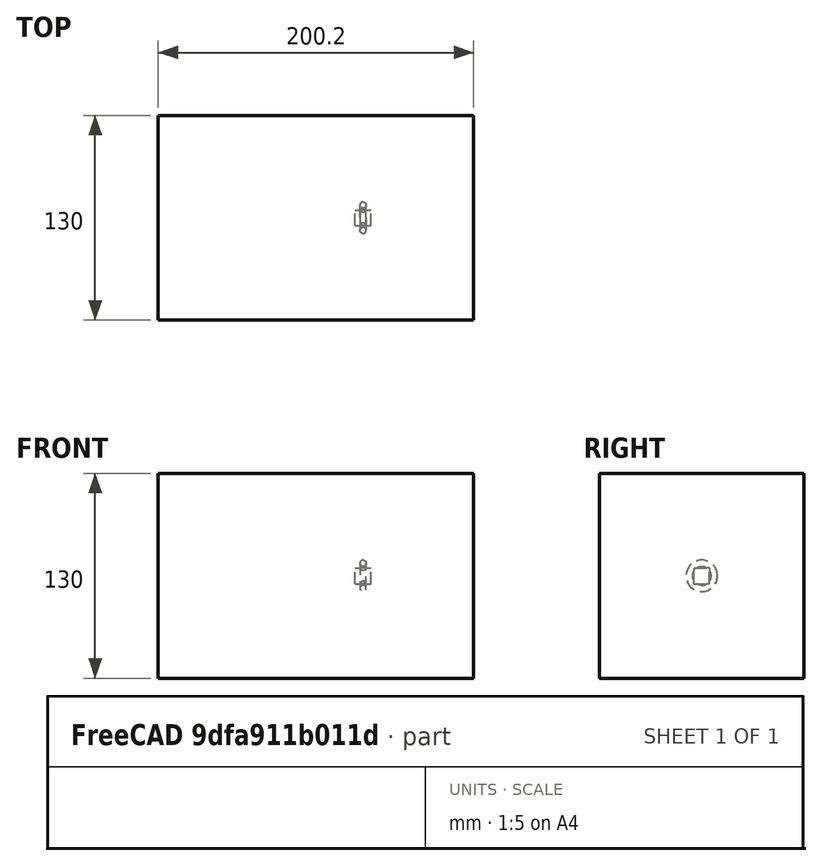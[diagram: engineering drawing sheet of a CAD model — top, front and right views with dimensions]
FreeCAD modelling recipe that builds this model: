
FCSTD DOCUMENT  (FreeCAD 1.0R39109 (Git))
Label: polarArray-7-array-rotated
License: All rights reserved
objects: App::DocumentObjectGroupPython×1251, Part::FeaturePython×4, App::Part×2, Part::MultiFuse×1
note: 4 computed .brp shape members not serialized (recipe doc carries the construction recipe); baked Part::Feature solids carry a one-line shape summary decoded from their .brp

FEATURE [App::DocumentObjectGroupPython] HALFPI  # scripted group (container) (typed FeaturePython)
  name = HALFPI
  value = pi/2.
FEATURE [App::DocumentObjectGroupPython] PI  # scripted group (container) (typed FeaturePython)
  name = PI
  value = 1.*pi
FEATURE [App::DocumentObjectGroupPython] TWOPI  # scripted group (container) (typed FeaturePython)
  name = TWOPI
  value = 2.*pi
FEATURE [App::DocumentObjectGroupPython] Constants  # scripted group (container) (typed FeaturePython)
  Group = -> [HALFPI,PI,TWOPI]
FEATURE [App::DocumentObjectGroupPython] Variables  # scripted group (container) (typed FeaturePython)
FEATURE [App::DocumentObjectGroupPython] Quantities  # scripted group (container) (typed FeaturePython)
FEATURE [App::DocumentObjectGroupPython] Isotopes  # scripted group (container) (typed FeaturePython)
FEATURE [App::DocumentObjectGroupPython] Elements  # scripted group (container) (typed FeaturePython)
FEATURE [App::DocumentObjectGroupPython] Matrix  # scripted group (container) (typed FeaturePython)
FEATURE [App::DocumentObjectGroupPython] Surfaces  # scripted group (container) (typed FeaturePython)
FEATURE [App::DocumentObjectGroupPython] Opticals  # scripted group (container) (typed FeaturePython)
  Group = -> [Matrix,Surfaces]
FEATURE [App::DocumentObjectGroupPython] G4Isotopes  # scripted group (container) (typed FeaturePython)
FEATURE [App::DocumentObjectGroupPython] H_element  # scripted group (container) (typed FeaturePython)
  Z = 1
  atom_value = 1.008
  formula = H
  name = H_element
FEATURE [App::DocumentObjectGroupPython] He_element  # scripted group (container) (typed FeaturePython)
  Z = 2
  atom_value = 4.0026
  formula = He
  name = He_element
FEATURE [App::DocumentObjectGroupPython] Li_element  # scripted group (container) (typed FeaturePython)
  Z = 3
  atom_value = 6.94
  formula = Li
  name = Li_element
FEATURE [App::DocumentObjectGroupPython] Be_element  # scripted group (container) (typed FeaturePython)
  Z = 4
  atom_value = 9.01218
  formula = Be
  name = Be_element
FEATURE [App::DocumentObjectGroupPython] B_element  # scripted group (container) (typed FeaturePython)
  Z = 5
  atom_value = 10.81
  formula = B
  name = B_element
FEATURE [App::DocumentObjectGroupPython] C_element  # scripted group (container) (typed FeaturePython)
  Z = 6
  atom_value = 12.011
  formula = C
  name = C_element
FEATURE [App::DocumentObjectGroupPython] N_element  # scripted group (container) (typed FeaturePython)
  Z = 7
  atom_value = 14.007
  formula = N
  name = N_element
FEATURE [App::DocumentObjectGroupPython] O_element  # scripted group (container) (typed FeaturePython)
  Z = 8
  atom_value = 15.999
  formula = O
  name = O_element
FEATURE [App::DocumentObjectGroupPython] F_element  # scripted group (container) (typed FeaturePython)
  Z = 9
  atom_value = 18.9984
  formula = F
  name = F_element
FEATURE [App::DocumentObjectGroupPython] Ne_element  # scripted group (container) (typed FeaturePython)
  Z = 10
  atom_value = 20.1797
  formula = Ne
  name = Ne_element
FEATURE [App::DocumentObjectGroupPython] Na_element  # scripted group (container) (typed FeaturePython)
  Z = 11
  atom_value = 22.9898
  formula = Na
  name = Na_element
FEATURE [App::DocumentObjectGroupPython] Mg_element  # scripted group (container) (typed FeaturePython)
  Z = 12
  atom_value = 24.305
  formula = Mg
  name = Mg_element
FEATURE [App::DocumentObjectGroupPython] Al_element  # scripted group (container) (typed FeaturePython)
  Z = 13
  atom_value = 26.9815
  formula = Al
  name = Al_element
FEATURE [App::DocumentObjectGroupPython] Si_element  # scripted group (container) (typed FeaturePython)
  Z = 14
  atom_value = 28.085
  formula = Si
  name = Si_element
FEATURE [App::DocumentObjectGroupPython] P_element  # scripted group (container) (typed FeaturePython)
  Z = 15
  atom_value = 30.9738
  formula = P
  name = P_element
FEATURE [App::DocumentObjectGroupPython] S_element  # scripted group (container) (typed FeaturePython)
  Z = 16
  atom_value = 32.06
  formula = S
  name = S_element
FEATURE [App::DocumentObjectGroupPython] Cl_element  # scripted group (container) (typed FeaturePython)
  Z = 17
  atom_value = 35.45
  formula = Cl
  name = Cl_element
FEATURE [App::DocumentObjectGroupPython] Ar_element  # scripted group (container) (typed FeaturePython)
  Z = 18
  atom_value = 39.95
  formula = Ar
  name = Ar_element
FEATURE [App::DocumentObjectGroupPython] K_element  # scripted group (container) (typed FeaturePython)
  Z = 19
  atom_value = 39.0983
  formula = K
  name = K_element
FEATURE [App::DocumentObjectGroupPython] Ca_element  # scripted group (container) (typed FeaturePython)
  Z = 20
  atom_value = 40.078
  formula = Ca
  name = Ca_element
FEATURE [App::DocumentObjectGroupPython] Sc_element  # scripted group (container) (typed FeaturePython)
  Z = 21
  atom_value = 44.9559
  formula = Sc
  name = Sc_element
FEATURE [App::DocumentObjectGroupPython] Ti_element  # scripted group (container) (typed FeaturePython)
  Z = 22
  atom_value = 47.867
  formula = Ti
  name = Ti_element
FEATURE [App::DocumentObjectGroupPython] V_element  # scripted group (container) (typed FeaturePython)
  Z = 23
  atom_value = 50.9415
  formula = V
  name = V_element
FEATURE [App::DocumentObjectGroupPython] Cr_element  # scripted group (container) (typed FeaturePython)
  Z = 24
  atom_value = 51.9961
  formula = Cr
  name = Cr_element
FEATURE [App::DocumentObjectGroupPython] Mn_element  # scripted group (container) (typed FeaturePython)
  Z = 25
  atom_value = 54.938
  formula = Mn
  name = Mn_element
FEATURE [App::DocumentObjectGroupPython] Fe_element  # scripted group (container) (typed FeaturePython)
  Z = 26
  atom_value = 55.845
  formula = Fe
  name = Fe_element
FEATURE [App::DocumentObjectGroupPython] Co_element  # scripted group (container) (typed FeaturePython)
  Z = 27
  atom_value = 58.9332
  formula = Co
  name = Co_element
FEATURE [App::DocumentObjectGroupPython] Ni_element  # scripted group (container) (typed FeaturePython)
  Z = 28
  atom_value = 58.6934
  formula = Ni
  name = Ni_element
FEATURE [App::DocumentObjectGroupPython] Cu_element  # scripted group (container) (typed FeaturePython)
  Z = 29
  atom_value = 63.546
  formula = Cu
  name = Cu_element
FEATURE [App::DocumentObjectGroupPython] Zn_element  # scripted group (container) (typed FeaturePython)
  Z = 30
  atom_value = 65.38
  formula = Zn
  name = Zn_element
FEATURE [App::DocumentObjectGroupPython] Ga_element  # scripted group (container) (typed FeaturePython)
  Z = 31
  atom_value = 69.723
  formula = Ga
  name = Ga_element
FEATURE [App::DocumentObjectGroupPython] Ge_element  # scripted group (container) (typed FeaturePython)
  Z = 32
  atom_value = 72.63
  formula = Ge
  name = Ge_element
FEATURE [App::DocumentObjectGroupPython] As_element  # scripted group (container) (typed FeaturePython)
  Z = 33
  atom_value = 74.9216
  formula = As
  name = As_element
FEATURE [App::DocumentObjectGroupPython] Se_element  # scripted group (container) (typed FeaturePython)
  Z = 34
  atom_value = 78.971
  formula = Se
  name = Se_element
FEATURE [App::DocumentObjectGroupPython] Br_element  # scripted group (container) (typed FeaturePython)
  Z = 35
  atom_value = 79.904
  formula = Br
  name = Br_element
FEATURE [App::DocumentObjectGroupPython] Kr_element  # scripted group (container) (typed FeaturePython)
  Z = 36
  atom_value = 83.798
  formula = Kr
  name = Kr_element
FEATURE [App::DocumentObjectGroupPython] Rb_element  # scripted group (container) (typed FeaturePython)
  Z = 37
  atom_value = 85.4678
  formula = Rb
  name = Rb_element
FEATURE [App::DocumentObjectGroupPython] Sr_element  # scripted group (container) (typed FeaturePython)
  Z = 38
  atom_value = 87.62
  formula = Sr
  name = Sr_element
FEATURE [App::DocumentObjectGroupPython] Y_element  # scripted group (container) (typed FeaturePython)
  Z = 39
  atom_value = 88.9058
  formula = Y
  name = Y_element
FEATURE [App::DocumentObjectGroupPython] Zr_element  # scripted group (container) (typed FeaturePython)
  Z = 40
  atom_value = 91.224
  formula = Zr
  name = Zr_element
FEATURE [App::DocumentObjectGroupPython] Nb_element  # scripted group (container) (typed FeaturePython)
  Z = 41
  atom_value = 92.9064
  formula = Nb
  name = Nb_element
FEATURE [App::DocumentObjectGroupPython] Mo_element  # scripted group (container) (typed FeaturePython)
  Z = 42
  atom_value = 95.95
  formula = Mo
  name = Mo_element
FEATURE [App::DocumentObjectGroupPython] Tc_element  # scripted group (container) (typed FeaturePython)
  Z = 43
  atom_value = 97
  formula = Tc
  name = Tc_element
FEATURE [App::DocumentObjectGroupPython] Ru_element  # scripted group (container) (typed FeaturePython)
  Z = 44
  atom_value = 101.07
  formula = Ru
  name = Ru_element
FEATURE [App::DocumentObjectGroupPython] Rh_element  # scripted group (container) (typed FeaturePython)
  Z = 45
  atom_value = 102.905
  formula = Rh
  name = Rh_element
FEATURE [App::DocumentObjectGroupPython] Pd_element  # scripted group (container) (typed FeaturePython)
  Z = 46
  atom_value = 106.42
  formula = Pd
  name = Pd_element
FEATURE [App::DocumentObjectGroupPython] Ag_element  # scripted group (container) (typed FeaturePython)
  Z = 47
  atom_value = 107.868
  formula = Ag
  name = Ag_element
FEATURE [App::DocumentObjectGroupPython] Cd_element  # scripted group (container) (typed FeaturePython)
  Z = 48
  atom_value = 112.414
  formula = Cd
  name = Cd_element
FEATURE [App::DocumentObjectGroupPython] In_element  # scripted group (container) (typed FeaturePython)
  Z = 49
  atom_value = 114.818
  formula = In
  name = In_element
FEATURE [App::DocumentObjectGroupPython] Sn_element  # scripted group (container) (typed FeaturePython)
  Z = 50
  atom_value = 118.71
  formula = Sn
  name = Sn_element
FEATURE [App::DocumentObjectGroupPython] Sb_element  # scripted group (container) (typed FeaturePython)
  Z = 51
  atom_value = 121.76
  formula = Sb
  name = Sb_element
FEATURE [App::DocumentObjectGroupPython] Te_element  # scripted group (container) (typed FeaturePython)
  Z = 52
  atom_value = 127.6
  formula = Te
  name = Te_element
FEATURE [App::DocumentObjectGroupPython] I_element  # scripted group (container) (typed FeaturePython)
  Z = 53
  atom_value = 126.904
  formula = I
  name = I_element
FEATURE [App::DocumentObjectGroupPython] Xe_element  # scripted group (container) (typed FeaturePython)
  Z = 54
  atom_value = 131.293
  formula = Xe
  name = Xe_element
FEATURE [App::DocumentObjectGroupPython] Cs_element  # scripted group (container) (typed FeaturePython)
  Z = 55
  atom_value = 132.905
  formula = Cs
  name = Cs_element
FEATURE [App::DocumentObjectGroupPython] Ba_element  # scripted group (container) (typed FeaturePython)
  Z = 56
  atom_value = 137.327
  formula = Ba
  name = Ba_element
FEATURE [App::DocumentObjectGroupPython] La_element  # scripted group (container) (typed FeaturePython)
  Z = 57
  atom_value = 138.905
  formula = La
  name = La_element
FEATURE [App::DocumentObjectGroupPython] Ce_element  # scripted group (container) (typed FeaturePython)
  Z = 58
  atom_value = 140.116
  formula = Ce
  name = Ce_element
FEATURE [App::DocumentObjectGroupPython] Pr_element  # scripted group (container) (typed FeaturePython)
  Z = 59
  atom_value = 140.908
  formula = Pr
  name = Pr_element
FEATURE [App::DocumentObjectGroupPython] Nd_element  # scripted group (container) (typed FeaturePython)
  Z = 60
  atom_value = 144.242
  formula = Nd
  name = Nd_element
FEATURE [App::DocumentObjectGroupPython] Pm_element  # scripted group (container) (typed FeaturePython)
  Z = 61
  atom_value = 145
  formula = Pm
  name = Pm_element
FEATURE [App::DocumentObjectGroupPython] Sm_element  # scripted group (container) (typed FeaturePython)
  Z = 62
  atom_value = 150.36
  formula = Sm
  name = Sm_element
FEATURE [App::DocumentObjectGroupPython] Eu_element  # scripted group (container) (typed FeaturePython)
  Z = 63
  atom_value = 151.964
  formula = Eu
  name = Eu_element
FEATURE [App::DocumentObjectGroupPython] Gd_element  # scripted group (container) (typed FeaturePython)
  Z = 64
  atom_value = 157.25
  formula = Gd
  name = Gd_element
FEATURE [App::DocumentObjectGroupPython] Tb_element  # scripted group (container) (typed FeaturePython)
  Z = 65
  atom_value = 158.925
  formula = Tb
  name = Tb_element
FEATURE [App::DocumentObjectGroupPython] Dy_element  # scripted group (container) (typed FeaturePython)
  Z = 66
  atom_value = 162.5
  formula = Dy
  name = Dy_element
FEATURE [App::DocumentObjectGroupPython] Ho_element  # scripted group (container) (typed FeaturePython)
  Z = 67
  atom_value = 164.93
  formula = Ho
  name = Ho_element
FEATURE [App::DocumentObjectGroupPython] Er_element  # scripted group (container) (typed FeaturePython)
  Z = 68
  atom_value = 167.259
  formula = Er
  name = Er_element
FEATURE [App::DocumentObjectGroupPython] Tm_element  # scripted group (container) (typed FeaturePython)
  Z = 69
  atom_value = 168.934
  formula = Tm
  name = Tm_element
FEATURE [App::DocumentObjectGroupPython] Yb_element  # scripted group (container) (typed FeaturePython)
  Z = 70
  atom_value = 173.045
  formula = Yb
  name = Yb_element
FEATURE [App::DocumentObjectGroupPython] Lu_element  # scripted group (container) (typed FeaturePython)
  Z = 71
  atom_value = 174.967
  formula = Lu
  name = Lu_element
FEATURE [App::DocumentObjectGroupPython] Hf_element  # scripted group (container) (typed FeaturePython)
  Z = 72
  atom_value = 178.49
  formula = Hf
  name = Hf_element
FEATURE [App::DocumentObjectGroupPython] Ta_element  # scripted group (container) (typed FeaturePython)
  Z = 73
  atom_value = 180.948
  formula = Ta
  name = Ta_element
FEATURE [App::DocumentObjectGroupPython] W_element  # scripted group (container) (typed FeaturePython)
  Z = 74
  atom_value = 183.84
  formula = W
  name = W_element
FEATURE [App::DocumentObjectGroupPython] Re_element  # scripted group (container) (typed FeaturePython)
  Z = 75
  atom_value = 186.207
  formula = Re
  name = Re_element
FEATURE [App::DocumentObjectGroupPython] Os_element  # scripted group (container) (typed FeaturePython)
  Z = 76
  atom_value = 190.23
  formula = Os
  name = Os_element
FEATURE [App::DocumentObjectGroupPython] Ir_element  # scripted group (container) (typed FeaturePython)
  Z = 77
  atom_value = 192.217
  formula = Ir
  name = Ir_element
FEATURE [App::DocumentObjectGroupPython] Pt_element  # scripted group (container) (typed FeaturePython)
  Z = 78
  atom_value = 195.084
  formula = Pt
  name = Pt_element
FEATURE [App::DocumentObjectGroupPython] Au_element  # scripted group (container) (typed FeaturePython)
  Z = 79
  atom_value = 196.967
  formula = Au
  name = Au_element
FEATURE [App::DocumentObjectGroupPython] Hg_element  # scripted group (container) (typed FeaturePython)
  Z = 80
  atom_value = 200.592
  formula = Hg
  name = Hg_element
FEATURE [App::DocumentObjectGroupPython] Tl_element  # scripted group (container) (typed FeaturePython)
  Z = 81
  atom_value = 204.38
  formula = Tl
  name = Tl_element
FEATURE [App::DocumentObjectGroupPython] Pb_element  # scripted group (container) (typed FeaturePython)
  Z = 82
  atom_value = 207.2
  formula = Pb
  name = Pb_element
FEATURE [App::DocumentObjectGroupPython] Bi_element  # scripted group (container) (typed FeaturePython)
  Z = 83
  atom_value = 208.98
  formula = Bi
  name = Bi_element
FEATURE [App::DocumentObjectGroupPython] Po_element  # scripted group (container) (typed FeaturePython)
  Z = 84
  atom_value = 209
  formula = Po
  name = Po_element
FEATURE [App::DocumentObjectGroupPython] At_element  # scripted group (container) (typed FeaturePython)
  Z = 85
  atom_value = 210
  formula = At
  name = At_element
FEATURE [App::DocumentObjectGroupPython] Rn_element  # scripted group (container) (typed FeaturePython)
  Z = 86
  atom_value = 222
  formula = Rn
  name = Rn_element
FEATURE [App::DocumentObjectGroupPython] Fr_element  # scripted group (container) (typed FeaturePython)
  Z = 87
  atom_value = 223
  formula = Fr
  name = Fr_element
FEATURE [App::DocumentObjectGroupPython] Ra_element  # scripted group (container) (typed FeaturePython)
  Z = 88
  atom_value = 226
  formula = Ra
  name = Ra_element
FEATURE [App::DocumentObjectGroupPython] Ac_element  # scripted group (container) (typed FeaturePython)
  Z = 89
  atom_value = 227
  formula = Ac
  name = Ac_element
FEATURE [App::DocumentObjectGroupPython] Th_element  # scripted group (container) (typed FeaturePython)
  Z = 90
  atom_value = 232.038
  formula = Th
  name = Th_element
FEATURE [App::DocumentObjectGroupPython] Pa_element  # scripted group (container) (typed FeaturePython)
  Z = 91
  atom_value = 231.036
  formula = Pa
  name = Pa_element
FEATURE [App::DocumentObjectGroupPython] U_element  # scripted group (container) (typed FeaturePython)
  Z = 92
  atom_value = 238.029
  formula = U
  name = U_element
FEATURE [App::DocumentObjectGroupPython] Np_element  # scripted group (container) (typed FeaturePython)
  Z = 93
  atom_value = 237
  formula = Np
  name = Np_element
FEATURE [App::DocumentObjectGroupPython] Pu_element  # scripted group (container) (typed FeaturePython)
  Z = 94
  atom_value = 244
  formula = Pu
  name = Pu_element
FEATURE [App::DocumentObjectGroupPython] Am_element  # scripted group (container) (typed FeaturePython)
  Z = 95
  atom_value = 243
  formula = Am
  name = Am_element
FEATURE [App::DocumentObjectGroupPython] Cm_element  # scripted group (container) (typed FeaturePython)
  Z = 96
  atom_value = 247
  formula = Cm
  name = Cm_element
FEATURE [App::DocumentObjectGroupPython] Bk_element  # scripted group (container) (typed FeaturePython)
  Z = 97
  atom_value = 247
  formula = Bk
  name = Bk_element
FEATURE [App::DocumentObjectGroupPython] Cf_element  # scripted group (container) (typed FeaturePython)
  Z = 98
  atom_value = 251
  formula = Cf
  name = Cf_element
FEATURE [App::DocumentObjectGroupPython] G4Elements  # scripted group (container) (typed FeaturePython)
  Group = -> [H_element,He_element,Li_element,Be_element,B_element,C_element,N_element,O_element,F_element,Ne_element,Na_element,Mg_element,Al_element,Si_element,P_element,S_element,Cl_element,Ar_element,K_element,Ca_element,Sc_element,Ti_element,V_element,Cr_element,Mn_element,Fe_element,Co_element,Ni_element,Cu_element,Zn_element,Ga_element,Ge_element,As_element,Se_element,Br_element,Kr_element,Rb_element,+61 more]
FEATURE [App::DocumentObjectGroupPython] H_element001  label="H_element : 0.101"  # scripted group (container) (typed FeaturePython)
  n = 0.101327
FEATURE [App::DocumentObjectGroupPython] C_element001  label="C_element : 0.775"  # scripted group (container) (typed FeaturePython)
  n = 0.7755
FEATURE [App::DocumentObjectGroupPython] N_element001  label="N_element : 0.035"  # scripted group (container) (typed FeaturePython)
  n = 0.035057
FEATURE [App::DocumentObjectGroupPython] O_element001  label="O_element : 0.052"  # scripted group (container) (typed FeaturePython)
  n = 0.0523159
FEATURE [App::DocumentObjectGroupPython] F_element001  label="F_element : 0.017"  # scripted group (container) (typed FeaturePython)
  n = 0.017422
FEATURE [App::DocumentObjectGroupPython] Ca_element001  label="Ca_element : 0.018"  # scripted group (container) (typed FeaturePython)
  n = 0.018378
FEATURE [App::DocumentObjectGroupPython] G4_A_150_TISSUE  label="G4_A-150_TISSUE"  # scripted group (container) (typed FeaturePython)
  Dunit = g/cm3
  Dvalue = 1.127
  Group = -> [H_element001,C_element001,N_element001,O_element001,F_element001,Ca_element001]
  conduct = 2
  density = 1
  expand = 3
  formula = G4_A-150_TISSUE
  name = G4_A-150_TISSUE
  specific = 4
FEATURE [App::DocumentObjectGroupPython] C_element002  label="C_element : 3"  # scripted group (container) (typed FeaturePython)
  n = 3
  ref = C_element
FEATURE [App::DocumentObjectGroupPython] H_element002  label="H_element : 6"  # scripted group (container) (typed FeaturePython)
  n = 6
  ref = H_element
FEATURE [App::DocumentObjectGroupPython] O_element002  label="O_element : 1"  # scripted group (container) (typed FeaturePython)
  n = 1
  ref = O_element
FEATURE [App::DocumentObjectGroupPython] G4_ACETONE  # scripted group (container) (typed FeaturePython)
  Dunit = g/cm3
  Dvalue = 0.7899
  Group = -> [C_element002,H_element002,O_element002]
  conduct = 2
  density = 1
  expand = 3
  formula = G4_ACETONE
  name = G4_ACETONE
  specific = 4
FEATURE [App::DocumentObjectGroupPython] C_element003  label="C_element : 2"  # scripted group (container) (typed FeaturePython)
  n = 2
  ref = C_element
FEATURE [App::DocumentObjectGroupPython] H_element003  label="H_element : 2"  # scripted group (container) (typed FeaturePython)
  n = 2
  ref = H_element
FEATURE [App::DocumentObjectGroupPython] G4_ACETYLENE  # scripted group (container) (typed FeaturePython)
  Dunit = g/cm3
  Dvalue = 0.0010967
  Group = -> [C_element003,H_element003]
  conduct = 2
  density = 1
  expand = 3
  formula = G4_ACETYLENE
  name = G4_ACETYLENE
  specific = 4
FEATURE [App::DocumentObjectGroupPython] C_element004  label="C_element : 5"  # scripted group (container) (typed FeaturePython)
  n = 5
  ref = C_element
FEATURE [App::DocumentObjectGroupPython] H_element004  label="H_element : 5"  # scripted group (container) (typed FeaturePython)
  n = 5
  ref = H_element
FEATURE [App::DocumentObjectGroupPython] N_element002  label="N_element : 5"  # scripted group (container) (typed FeaturePython)
  n = 5
  ref = N_element
FEATURE [App::DocumentObjectGroupPython] G4_ADENINE  # scripted group (container) (typed FeaturePython)
  Dunit = g/cm3
  Dvalue = 1.6
  Group = -> [C_element004,H_element004,N_element002]
  conduct = 2
  density = 1
  expand = 3
  formula = G4_ADENINE
  name = G4_ADENINE
  specific = 4
FEATURE [App::DocumentObjectGroupPython] H_element005  label="H_element : 0.114"  # scripted group (container) (typed FeaturePython)
  n = 0.114
FEATURE [App::DocumentObjectGroupPython] C_element005  label="C_element : 0.598"  # scripted group (container) (typed FeaturePython)
  n = 0.598
FEATURE [App::DocumentObjectGroupPython] N_element003  label="N_element : 0.007"  # scripted group (container) (typed FeaturePython)
  n = 0.007
FEATURE [App::DocumentObjectGroupPython] O_element003  label="O_element : 0.278"  # scripted group (container) (typed FeaturePython)
  n = 0.278
FEATURE [App::DocumentObjectGroupPython] Na_element001  label="Na_element : 0.001"  # scripted group (container) (typed FeaturePython)
  n = 0.001
FEATURE [App::DocumentObjectGroupPython] S_element001  label="S_element : 0.001"  # scripted group (container) (typed FeaturePython)
  n = 0.001
FEATURE [App::DocumentObjectGroupPython] Cl_element001  label="Cl_element : 0.001"  # scripted group (container) (typed FeaturePython)
  n = 0.001
FEATURE [App::DocumentObjectGroupPython] G4_ADIPOSE_TISSUE_ICRP  # scripted group (container) (typed FeaturePython)
  Dunit = g/cm3
  Dvalue = 0.95
  Group = -> [H_element005,C_element005,N_element003,O_element003,Na_element001,S_element001,Cl_element001]
  conduct = 2
  density = 1
  expand = 3
  formula = G4_ADIPOSE_TISSUE_ICRP
  name = G4_ADIPOSE_TISSUE_ICRP
  specific = 4
FEATURE [App::DocumentObjectGroupPython] C_element006  label="C_element : 0.000"  # scripted group (container) (typed FeaturePython)
  n = 0.000124
FEATURE [App::DocumentObjectGroupPython] N_element004  label="N_element : 0.755"  # scripted group (container) (typed FeaturePython)
  n = 0.755268
FEATURE [App::DocumentObjectGroupPython] O_element004  label="O_element : 0.232"  # scripted group (container) (typed FeaturePython)
  n = 0.231781
FEATURE [App::DocumentObjectGroupPython] Ar_element001  label="Ar_element : 0.013"  # scripted group (container) (typed FeaturePython)
  n = 0.012827
FEATURE [App::DocumentObjectGroupPython] G4_AIR  # scripted group (container) (typed FeaturePython)
  Dunit = g/cm3
  Dvalue = 0.00120479
  Group = -> [C_element006,N_element004,O_element004,Ar_element001]
  conduct = 2
  density = 1
  expand = 3
  formula = G4_AIR
  name = G4_AIR
  specific = 4
FEATURE [App::DocumentObjectGroupPython] C_element007  label="C_element : 006"  # scripted group (container) (typed FeaturePython)
  n = 3
  ref = C_element
FEATURE [App::DocumentObjectGroupPython] H_element006  label="H_element : 7"  # scripted group (container) (typed FeaturePython)
  n = 7
  ref = H_element
FEATURE [App::DocumentObjectGroupPython] N_element005  label="N_element : 1"  # scripted group (container) (typed FeaturePython)
  n = 1
  ref = N_element
FEATURE [App::DocumentObjectGroupPython] O_element005  label="O_element : 2"  # scripted group (container) (typed FeaturePython)
  n = 2
  ref = O_element
FEATURE [App::DocumentObjectGroupPython] G4_ALANINE  # scripted group (container) (typed FeaturePython)
  Dunit = g/cm3
  Dvalue = 1.42
  Group = -> [C_element007,H_element006,N_element005,O_element005]
  conduct = 2
  density = 1
  expand = 3
  formula = G4_ALANINE
  name = G4_ALANINE
  specific = 4
FEATURE [App::DocumentObjectGroupPython] Al_element001  label="Al_element : 2"  # scripted group (container) (typed FeaturePython)
  n = 2
  ref = Al_element
FEATURE [App::DocumentObjectGroupPython] O_element006  label="O_element : 3"  # scripted group (container) (typed FeaturePython)
  n = 3
  ref = O_element
FEATURE [App::DocumentObjectGroupPython] G4_ALUMINUM_OXIDE  # scripted group (container) (typed FeaturePython)
  Dunit = g/cm3
  Dvalue = 3.97
  Group = -> [Al_element001,O_element006]
  conduct = 2
  density = 1
  expand = 3
  formula = G4_ALUMINUM_OXIDE
  name = G4_ALUMINUM_OXIDE
  specific = 4
FEATURE [App::DocumentObjectGroupPython] H_element007  label="H_element : 0.106"  # scripted group (container) (typed FeaturePython)
  n = 0.10593
FEATURE [App::DocumentObjectGroupPython] C_element008  label="C_element : 0.789"  # scripted group (container) (typed FeaturePython)
  n = 0.788974
FEATURE [App::DocumentObjectGroupPython] O_element007  label="O_element : 0.105"  # scripted group (container) (typed FeaturePython)
  n = 0.105096
FEATURE [App::DocumentObjectGroupPython] G4_AMBER  # scripted group (container) (typed FeaturePython)
  Dunit = g/cm3
  Dvalue = 1.1
  Group = -> [H_element007,C_element008,O_element007]
  conduct = 2
  density = 1
  expand = 3
  formula = G4_AMBER
  name = G4_AMBER
  specific = 4
FEATURE [App::DocumentObjectGroupPython] N_element006  label="N_element : 006"  # scripted group (container) (typed FeaturePython)
  n = 1
  ref = N_element
FEATURE [App::DocumentObjectGroupPython] H_element008  label="H_element : 3"  # scripted group (container) (typed FeaturePython)
  n = 3
  ref = H_element
FEATURE [App::DocumentObjectGroupPython] G4_AMMONIA  # scripted group (container) (typed FeaturePython)
  Dunit = g/cm3
  Dvalue = 0.000826019
  Group = -> [N_element006,H_element008]
  conduct = 2
  density = 1
  expand = 3
  formula = G4_AMMONIA
  name = G4_AMMONIA
  specific = 4
FEATURE [App::DocumentObjectGroupPython] C_element009  label="C_element : 6"  # scripted group (container) (typed FeaturePython)
  n = 6
  ref = C_element
FEATURE [App::DocumentObjectGroupPython] H_element009  label="H_element : 008"  # scripted group (container) (typed FeaturePython)
  n = 7
  ref = H_element
FEATURE [App::DocumentObjectGroupPython] N_element007  label="N_element : 007"  # scripted group (container) (typed FeaturePython)
  n = 1
  ref = N_element
FEATURE [App::DocumentObjectGroupPython] G4_ANILINE  # scripted group (container) (typed FeaturePython)
  Dunit = g/cm3
  Dvalue = 1.0235
  Group = -> [C_element009,H_element009,N_element007]
  conduct = 2
  density = 1
  expand = 3
  formula = G4_ANILINE
  name = G4_ANILINE
  specific = 4
FEATURE [App::DocumentObjectGroupPython] C_element010  label="C_element : 14"  # scripted group (container) (typed FeaturePython)
  n = 14
  ref = C_element
FEATURE [App::DocumentObjectGroupPython] H_element010  label="H_element : 10"  # scripted group (container) (typed FeaturePython)
  n = 10
  ref = H_element
FEATURE [App::DocumentObjectGroupPython] G4_ANTHRACENE  # scripted group (container) (typed FeaturePython)
  Dunit = g/cm3
  Dvalue = 1.283
  Group = -> [C_element010,H_element010]
  conduct = 2
  density = 1
  expand = 3
  formula = G4_ANTHRACENE
  name = G4_ANTHRACENE
  specific = 4
FEATURE [App::DocumentObjectGroupPython] H_element011  label="H_element : 0.065"  # scripted group (container) (typed FeaturePython)
  n = 0.0654709
FEATURE [App::DocumentObjectGroupPython] C_element011  label="C_element : 0.537"  # scripted group (container) (typed FeaturePython)
  n = 0.536944
FEATURE [App::DocumentObjectGroupPython] N_element008  label="N_element : 0.021"  # scripted group (container) (typed FeaturePython)
  n = 0.0215
FEATURE [App::DocumentObjectGroupPython] O_element008  label="O_element : 0.032"  # scripted group (container) (typed FeaturePython)
  n = 0.032085
FEATURE [App::DocumentObjectGroupPython] F_element002  label="F_element : 0.167"  # scripted group (container) (typed FeaturePython)
  n = 0.167411
FEATURE [App::DocumentObjectGroupPython] Ca_element002  label="Ca_element : 0.177"  # scripted group (container) (typed FeaturePython)
  n = 0.176589
FEATURE [App::DocumentObjectGroupPython] G4_B_100_BONE  label="G4_B-100_BONE"  # scripted group (container) (typed FeaturePython)
  Dunit = g/cm3
  Dvalue = 1.45
  Group = -> [H_element011,C_element011,N_element008,O_element008,F_element002,Ca_element002]
  conduct = 2
  density = 1
  expand = 3
  formula = G4_B-100_BONE
  name = G4_B-100_BONE
  specific = 4
FEATURE [App::DocumentObjectGroupPython] H_element012  label="H_element : 0.057"  # scripted group (container) (typed FeaturePython)
  n = 0.057441
FEATURE [App::DocumentObjectGroupPython] C_element012  label="C_element : 0.790"  # scripted group (container) (typed FeaturePython)
  n = 0.774591
FEATURE [App::DocumentObjectGroupPython] O_element009  label="O_element : 0.168"  # scripted group (container) (typed FeaturePython)
  n = 0.167968
FEATURE [App::DocumentObjectGroupPython] G4_BAKELITE  # scripted group (container) (typed FeaturePython)
  Dunit = g/cm3
  Dvalue = 1.25
  Group = -> [H_element012,C_element012,O_element009]
  conduct = 2
  density = 1
  expand = 3
  formula = G4_BAKELITE
  name = G4_BAKELITE
  specific = 4
FEATURE [App::DocumentObjectGroupPython] Ba_element001  label="Ba_element : 1"  # scripted group (container) (typed FeaturePython)
  n = 1
  ref = Ba_element
FEATURE [App::DocumentObjectGroupPython] F_element003  label="F_element : 2"  # scripted group (container) (typed FeaturePython)
  n = 2
  ref = F_element
FEATURE [App::DocumentObjectGroupPython] G4_BARIUM_FLUORIDE  # scripted group (container) (typed FeaturePython)
  Dunit = g/cm3
  Dvalue = 4.89
  Group = -> [Ba_element001,F_element003]
  conduct = 2
  density = 1
  expand = 3
  formula = G4_BARIUM_FLUORIDE
  name = G4_BARIUM_FLUORIDE
  specific = 4
FEATURE [App::DocumentObjectGroupPython] Ba_element002  label="Ba_element : 002"  # scripted group (container) (typed FeaturePython)
  n = 1
  ref = Ba_element
FEATURE [App::DocumentObjectGroupPython] S_element002  label="S_element : 1"  # scripted group (container) (typed FeaturePython)
  n = 1
  ref = S_element
FEATURE [App::DocumentObjectGroupPython] O_element010  label="O_element : 4"  # scripted group (container) (typed FeaturePython)
  n = 4
  ref = O_element
FEATURE [App::DocumentObjectGroupPython] G4_BARIUM_SULFATE  # scripted group (container) (typed FeaturePython)
  Dunit = g/cm3
  Dvalue = 4.5
  Group = -> [Ba_element002,S_element002,O_element010]
  conduct = 2
  density = 1
  expand = 3
  formula = G4_BARIUM_SULFATE
  name = G4_BARIUM_SULFATE
  specific = 4
FEATURE [App::DocumentObjectGroupPython] C_element013  label="C_element : 007"  # scripted group (container) (typed FeaturePython)
  n = 6
  ref = C_element
FEATURE [App::DocumentObjectGroupPython] H_element013  label="H_element : 009"  # scripted group (container) (typed FeaturePython)
  n = 6
  ref = H_element
FEATURE [App::DocumentObjectGroupPython] G4_BENZENE  # scripted group (container) (typed FeaturePython)
  Dunit = g/cm3
  Dvalue = 0.87865
  Group = -> [C_element013,H_element013]
  conduct = 2
  density = 1
  expand = 3
  formula = G4_BENZENE
  name = G4_BENZENE
  specific = 4
FEATURE [App::DocumentObjectGroupPython] Be_element001  label="Be_element : 1"  # scripted group (container) (typed FeaturePython)
  n = 1
  ref = Be_element
FEATURE [App::DocumentObjectGroupPython] O_element011  label="O_element : 005"  # scripted group (container) (typed FeaturePython)
  n = 1
  ref = O_element
FEATURE [App::DocumentObjectGroupPython] G4_BERYLLIUM_OXIDE  # scripted group (container) (typed FeaturePython)
  Dunit = g/cm3
  Dvalue = 3.01
  Group = -> [Be_element001,O_element011]
  conduct = 2
  density = 1
  expand = 3
  formula = G4_BERYLLIUM_OXIDE
  name = G4_BERYLLIUM_OXIDE
  specific = 4
FEATURE [App::DocumentObjectGroupPython] Bi_element001  label="Bi_element : 4"  # scripted group (container) (typed FeaturePython)
  n = 4
  ref = Bi_element
FEATURE [App::DocumentObjectGroupPython] Ge_element001  label="Ge_element : 3"  # scripted group (container) (typed FeaturePython)
  n = 3
  ref = Ge_element
FEATURE [App::DocumentObjectGroupPython] O_element012  label="O_element : 12"  # scripted group (container) (typed FeaturePython)
  n = 12
  ref = O_element
FEATURE [App::DocumentObjectGroupPython] G4_BGO  # scripted group (container) (typed FeaturePython)
  Dunit = g/cm3
  Dvalue = 7.13
  Group = -> [Bi_element001,Ge_element001,O_element012]
  conduct = 2
  density = 1
  expand = 3
  formula = G4_BGO
  name = G4_BGO
  specific = 4
FEATURE [App::DocumentObjectGroupPython] H_element014  label="H_element : 0.102"  # scripted group (container) (typed FeaturePython)
  n = 0.102
FEATURE [App::DocumentObjectGroupPython] C_element014  label="C_element : 0.110"  # scripted group (container) (typed FeaturePython)
  n = 0.11
FEATURE [App::DocumentObjectGroupPython] N_element009  label="N_element : 0.033"  # scripted group (container) (typed FeaturePython)
  n = 0.033
FEATURE [App::DocumentObjectGroupPython] O_element013  label="O_element : 0.745"  # scripted group (container) (typed FeaturePython)
  n = 0.745
FEATURE [App::DocumentObjectGroupPython] Na_element002  label="Na_element : 0.002"  # scripted group (container) (typed FeaturePython)
  n = 0.001
FEATURE [App::DocumentObjectGroupPython] P_element001  label="P_element : 0.001"  # scripted group (container) (typed FeaturePython)
  n = 0.001
FEATURE [App::DocumentObjectGroupPython] S_element003  label="S_element : 0.002"  # scripted group (container) (typed FeaturePython)
  n = 0.002
FEATURE [App::DocumentObjectGroupPython] Cl_element002  label="Cl_element : 0.003"  # scripted group (container) (typed FeaturePython)
  n = 0.003
FEATURE [App::DocumentObjectGroupPython] K_element001  label="K_element : 0.002"  # scripted group (container) (typed FeaturePython)
  n = 0.002
FEATURE [App::DocumentObjectGroupPython] Fe_element001  label="Fe_element : 0.001"  # scripted group (container) (typed FeaturePython)
  n = 0.001
FEATURE [App::DocumentObjectGroupPython] G4_BLOOD_ICRP  # scripted group (container) (typed FeaturePython)
  Dunit = g/cm3
  Dvalue = 1.06
  Group = -> [H_element014,C_element014,N_element009,O_element013,Na_element002,P_element001,S_element003,Cl_element002,K_element001,Fe_element001]
  conduct = 2
  density = 1
  expand = 3
  formula = G4_BLOOD_ICRP
  name = G4_BLOOD_ICRP
  specific = 4
FEATURE [App::DocumentObjectGroupPython] H_element015  label="H_element : 0.064"  # scripted group (container) (typed FeaturePython)
  n = 0.064
FEATURE [App::DocumentObjectGroupPython] C_element015  label="C_element : 0.278"  # scripted group (container) (typed FeaturePython)
  n = 0.278
FEATURE [App::DocumentObjectGroupPython] N_element010  label="N_element : 0.027"  # scripted group (container) (typed FeaturePython)
  n = 0.027
FEATURE [App::DocumentObjectGroupPython] O_element014  label="O_element : 0.410"  # scripted group (container) (typed FeaturePython)
  n = 0.41
FEATURE [App::DocumentObjectGroupPython] Mg_element001  label="Mg_element : 0.002"  # scripted group (container) (typed FeaturePython)
  n = 0.002
FEATURE [App::DocumentObjectGroupPython] P_element002  label="P_element : 0.070"  # scripted group (container) (typed FeaturePython)
  n = 0.07
FEATURE [App::DocumentObjectGroupPython] S_element004  label="S_element : 0.003"  # scripted group (container) (typed FeaturePython)
  n = 0.002
FEATURE [App::DocumentObjectGroupPython] Ca_element003  label="Ca_element : 0.147"  # scripted group (container) (typed FeaturePython)
  n = 0.147
FEATURE [App::DocumentObjectGroupPython] G4_BONE_COMPACT_ICRU  # scripted group (container) (typed FeaturePython)
  Dunit = g/cm3
  Dvalue = 1.85
  Group = -> [H_element015,C_element015,N_element010,O_element014,Mg_element001,P_element002,S_element004,Ca_element003]
  conduct = 2
  density = 1
  expand = 3
  formula = G4_BONE_COMPACT_ICRU
  name = G4_BONE_COMPACT_ICRU
  specific = 4
FEATURE [App::DocumentObjectGroupPython] H_element016  label="H_element : 0.034"  # scripted group (container) (typed FeaturePython)
  n = 0.034
FEATURE [App::DocumentObjectGroupPython] C_element016  label="C_element : 0.155"  # scripted group (container) (typed FeaturePython)
  n = 0.155
FEATURE [App::DocumentObjectGroupPython] N_element011  label="N_element : 0.042"  # scripted group (container) (typed FeaturePython)
  n = 0.042
FEATURE [App::DocumentObjectGroupPython] O_element015  label="O_element : 0.435"  # scripted group (container) (typed FeaturePython)
  n = 0.435
FEATURE [App::DocumentObjectGroupPython] Na_element003  label="Na_element : 0.003"  # scripted group (container) (typed FeaturePython)
  n = 0.001
FEATURE [App::DocumentObjectGroupPython] Mg_element002  label="Mg_element : 0.003"  # scripted group (container) (typed FeaturePython)
  n = 0.002
FEATURE [App::DocumentObjectGroupPython] P_element003  label="P_element : 0.103"  # scripted group (container) (typed FeaturePython)
  n = 0.103
FEATURE [App::DocumentObjectGroupPython] S_element005  label="S_element : 0.004"  # scripted group (container) (typed FeaturePython)
  n = 0.003
FEATURE [App::DocumentObjectGroupPython] Ca_element004  label="Ca_element : 0.225"  # scripted group (container) (typed FeaturePython)
  n = 0.225
FEATURE [App::DocumentObjectGroupPython] G4_BONE_CORTICAL_ICRP  # scripted group (container) (typed FeaturePython)
  Dunit = g/cm3
  Dvalue = 1.92
  Group = -> [H_element016,C_element016,N_element011,O_element015,Na_element003,Mg_element002,P_element003,S_element005,Ca_element004]
  conduct = 2
  density = 1
  expand = 3
  formula = G4_BONE_CORTICAL_ICRP
  name = G4_BONE_CORTICAL_ICRP
  specific = 4
FEATURE [App::DocumentObjectGroupPython] B_element001  label="B_element : 4"  # scripted group (container) (typed FeaturePython)
  n = 4
  ref = B_element
FEATURE [App::DocumentObjectGroupPython] C_element017  label="C_element : 1"  # scripted group (container) (typed FeaturePython)
  n = 1
  ref = C_element
FEATURE [App::DocumentObjectGroupPython] G4_BORON_CARBIDE  # scripted group (container) (typed FeaturePython)
  Dunit = g/cm3
  Dvalue = 2.52
  Group = -> [B_element001,C_element017]
  conduct = 2
  density = 1
  expand = 3
  formula = G4_BORON_CARBIDE
  name = G4_BORON_CARBIDE
  specific = 4
FEATURE [App::DocumentObjectGroupPython] B_element002  label="B_element : 2"  # scripted group (container) (typed FeaturePython)
  n = 2
  ref = B_element
FEATURE [App::DocumentObjectGroupPython] O_element016  label="O_element : 006"  # scripted group (container) (typed FeaturePython)
  n = 3
  ref = O_element
FEATURE [App::DocumentObjectGroupPython] G4_BORON_OXIDE  # scripted group (container) (typed FeaturePython)
  Dunit = g/cm3
  Dvalue = 1.812
  Group = -> [B_element002,O_element016]
  conduct = 2
  density = 1
  expand = 3
  formula = G4_BORON_OXIDE
  name = G4_BORON_OXIDE
  specific = 4
FEATURE [App::DocumentObjectGroupPython] H_element017  label="H_element : 0.107"  # scripted group (container) (typed FeaturePython)
  n = 0.107
FEATURE [App::DocumentObjectGroupPython] C_element018  label="C_element : 0.145"  # scripted group (container) (typed FeaturePython)
  n = 0.145
FEATURE [App::DocumentObjectGroupPython] N_element012  label="N_element : 0.022"  # scripted group (container) (typed FeaturePython)
  n = 0.022
FEATURE [App::DocumentObjectGroupPython] O_element017  label="O_element : 0.712"  # scripted group (container) (typed FeaturePython)
  n = 0.712
FEATURE [App::DocumentObjectGroupPython] Na_element004  label="Na_element : 0.004"  # scripted group (container) (typed FeaturePython)
  n = 0.002
FEATURE [App::DocumentObjectGroupPython] P_element004  label="P_element : 0.004"  # scripted group (container) (typed FeaturePython)
  n = 0.004
FEATURE [App::DocumentObjectGroupPython] S_element006  label="S_element : 0.005"  # scripted group (container) (typed FeaturePython)
  n = 0.002
FEATURE [App::DocumentObjectGroupPython] Cl_element003  label="Cl_element : 0.004"  # scripted group (container) (typed FeaturePython)
  n = 0.003
FEATURE [App::DocumentObjectGroupPython] K_element002  label="K_element : 0.003"  # scripted group (container) (typed FeaturePython)
  n = 0.003
FEATURE [App::DocumentObjectGroupPython] G4_BRAIN_ICRP  # scripted group (container) (typed FeaturePython)
  Dunit = g/cm3
  Dvalue = 1.04
  Group = -> [H_element017,C_element018,N_element012,O_element017,Na_element004,P_element004,S_element006,Cl_element003,K_element002]
  conduct = 2
  density = 1
  expand = 3
  formula = G4_BRAIN_ICRP
  name = G4_BRAIN_ICRP
  specific = 4
FEATURE [App::DocumentObjectGroupPython] C_element019  label="C_element : 4"  # scripted group (container) (typed FeaturePython)
  n = 4
  ref = C_element
FEATURE [App::DocumentObjectGroupPython] H_element018  label="H_element : 010"  # scripted group (container) (typed FeaturePython)
  n = 10
  ref = H_element
FEATURE [App::DocumentObjectGroupPython] G4_BUTANE  # scripted group (container) (typed FeaturePython)
  Dunit = g/cm3
  Dvalue = 0.00249343
  Group = -> [C_element019,H_element018]
  conduct = 2
  density = 1
  expand = 3
  formula = G4_BUTANE
  name = G4_BUTANE
  specific = 4
FEATURE [App::DocumentObjectGroupPython] C_element020  label="C_element : 008"  # scripted group (container) (typed FeaturePython)
  n = 4
  ref = C_element
FEATURE [App::DocumentObjectGroupPython] H_element019  label="H_element : 011"  # scripted group (container) (typed FeaturePython)
  n = 10
  ref = H_element
FEATURE [App::DocumentObjectGroupPython] O_element018  label="O_element : 007"  # scripted group (container) (typed FeaturePython)
  n = 1
  ref = O_element
FEATURE [App::DocumentObjectGroupPython] G4_N_BUTYL_ALCOHOL  label="G4_N-BUTYL_ALCOHOL"  # scripted group (container) (typed FeaturePython)
  Dunit = g/cm3
  Dvalue = 0.8098
  Group = -> [C_element020,H_element019,O_element018]
  conduct = 2
  density = 1
  expand = 3
  formula = G4_N-BUTYL_ALCOHOL
  name = G4_N-BUTYL_ALCOHOL
  specific = 4
FEATURE [App::DocumentObjectGroupPython] H_element020  label="H_element : 0.025"  # scripted group (container) (typed FeaturePython)
  n = 0.02468
FEATURE [App::DocumentObjectGroupPython] C_element021  label="C_element : 0.502"  # scripted group (container) (typed FeaturePython)
  n = 0.501611
FEATURE [App::DocumentObjectGroupPython] O_element019  label="O_element : 0.005"  # scripted group (container) (typed FeaturePython)
  n = 0.004527
FEATURE [App::DocumentObjectGroupPython] F_element004  label="F_element : 0.465"  # scripted group (container) (typed FeaturePython)
  n = 0.465209
FEATURE [App::DocumentObjectGroupPython] Si_element001  label="Si_element : 0.004"  # scripted group (container) (typed FeaturePython)
  n = 0.003973
FEATURE [App::DocumentObjectGroupPython] G4_C_552  label="G4_C-552"  # scripted group (container) (typed FeaturePython)
  Dunit = g/cm3
  Dvalue = 1.76
  Group = -> [H_element020,C_element021,O_element019,F_element004,Si_element001]
  conduct = 2
  density = 1
  expand = 3
  formula = G4_C-552
  name = G4_C-552
  specific = 4
FEATURE [App::DocumentObjectGroupPython] Cd_element001  label="Cd_element : 1"  # scripted group (container) (typed FeaturePython)
  n = 1
  ref = Cd_element
FEATURE [App::DocumentObjectGroupPython] Te_element001  label="Te_element : 1"  # scripted group (container) (typed FeaturePython)
  n = 1
  ref = Te_element
FEATURE [App::DocumentObjectGroupPython] G4_CADMIUM_TELLURIDE  # scripted group (container) (typed FeaturePython)
  Dunit = g/cm3
  Dvalue = 6.2
  Group = -> [Cd_element001,Te_element001]
  conduct = 2
  density = 1
  expand = 3
  formula = G4_CADMIUM_TELLURIDE
  name = G4_CADMIUM_TELLURIDE
  specific = 4
FEATURE [App::DocumentObjectGroupPython] Cd_element002  label="Cd_element : 002"  # scripted group (container) (typed FeaturePython)
  n = 1
  ref = Cd_element
FEATURE [App::DocumentObjectGroupPython] W_element001  label="W_element : 1"  # scripted group (container) (typed FeaturePython)
  n = 1
  ref = W_element
FEATURE [App::DocumentObjectGroupPython] O_element020  label="O_element : 008"  # scripted group (container) (typed FeaturePython)
  n = 4
  ref = O_element
FEATURE [App::DocumentObjectGroupPython] G4_CADMIUM_TUNGSTATE  # scripted group (container) (typed FeaturePython)
  Dunit = g/cm3
  Dvalue = 7.9
  Group = -> [Cd_element002,W_element001,O_element020]
  conduct = 2
  density = 1
  expand = 3
  formula = G4_CADMIUM_TUNGSTATE
  name = G4_CADMIUM_TUNGSTATE
  specific = 4
FEATURE [App::DocumentObjectGroupPython] Ca_element005  label="Ca_element : 1"  # scripted group (container) (typed FeaturePython)
  n = 1
  ref = Ca_element
FEATURE [App::DocumentObjectGroupPython] C_element022  label="C_element : 009"  # scripted group (container) (typed FeaturePython)
  n = 1
  ref = C_element
FEATURE [App::DocumentObjectGroupPython] O_element021  label="O_element : 009"  # scripted group (container) (typed FeaturePython)
  n = 3
  ref = O_element
FEATURE [App::DocumentObjectGroupPython] G4_CALCIUM_CARBONATE  # scripted group (container) (typed FeaturePython)
  Dunit = g/cm3
  Dvalue = 2.8
  Group = -> [Ca_element005,C_element022,O_element021]
  conduct = 2
  density = 1
  expand = 3
  formula = G4_CALCIUM_CARBONATE
  name = G4_CALCIUM_CARBONATE
  specific = 4
FEATURE [App::DocumentObjectGroupPython] Ca_element006  label="Ca_element : 002"  # scripted group (container) (typed FeaturePython)
  n = 1
  ref = Ca_element
FEATURE [App::DocumentObjectGroupPython] F_element005  label="F_element : 003"  # scripted group (container) (typed FeaturePython)
  n = 2
  ref = F_element
FEATURE [App::DocumentObjectGroupPython] G4_CALCIUM_FLUORIDE  # scripted group (container) (typed FeaturePython)
  Dunit = g/cm3
  Dvalue = 3.18
  Group = -> [Ca_element006,F_element005]
  conduct = 2
  density = 1
  expand = 3
  formula = G4_CALCIUM_FLUORIDE
  name = G4_CALCIUM_FLUORIDE
  specific = 4
FEATURE [App::DocumentObjectGroupPython] Ca_element007  label="Ca_element : 003"  # scripted group (container) (typed FeaturePython)
  n = 1
  ref = Ca_element
FEATURE [App::DocumentObjectGroupPython] O_element022  label="O_element : 010"  # scripted group (container) (typed FeaturePython)
  n = 1
  ref = O_element
FEATURE [App::DocumentObjectGroupPython] G4_CALCIUM_OXIDE  # scripted group (container) (typed FeaturePython)
  Dunit = g/cm3
  Dvalue = 3.3
  Group = -> [Ca_element007,O_element022]
  conduct = 2
  density = 1
  expand = 3
  formula = G4_CALCIUM_OXIDE
  name = G4_CALCIUM_OXIDE
  specific = 4
FEATURE [App::DocumentObjectGroupPython] Ca_element008  label="Ca_element : 004"  # scripted group (container) (typed FeaturePython)
  n = 1
  ref = Ca_element
FEATURE [App::DocumentObjectGroupPython] S_element007  label="S_element : 002"  # scripted group (container) (typed FeaturePython)
  n = 1
  ref = S_element
FEATURE [App::DocumentObjectGroupPython] O_element023  label="O_element : 011"  # scripted group (container) (typed FeaturePython)
  n = 4
  ref = O_element
FEATURE [App::DocumentObjectGroupPython] G4_CALCIUM_SULFATE  # scripted group (container) (typed FeaturePython)
  Dunit = g/cm3
  Dvalue = 2.96
  Group = -> [Ca_element008,S_element007,O_element023]
  conduct = 2
  density = 1
  expand = 3
  formula = G4_CALCIUM_SULFATE
  name = G4_CALCIUM_SULFATE
  specific = 4
FEATURE [App::DocumentObjectGroupPython] Ca_element009  label="Ca_element : 005"  # scripted group (container) (typed FeaturePython)
  n = 1
  ref = Ca_element
FEATURE [App::DocumentObjectGroupPython] W_element002  label="W_element : 002"  # scripted group (container) (typed FeaturePython)
  n = 1
  ref = W_element
FEATURE [App::DocumentObjectGroupPython] O_element024  label="O_element : 012"  # scripted group (container) (typed FeaturePython)
  n = 4
  ref = O_element
FEATURE [App::DocumentObjectGroupPython] G4_CALCIUM_TUNGSTATE  # scripted group (container) (typed FeaturePython)
  Dunit = g/cm3
  Dvalue = 6.062
  Group = -> [Ca_element009,W_element002,O_element024]
  conduct = 2
  density = 1
  expand = 3
  formula = G4_CALCIUM_TUNGSTATE
  name = G4_CALCIUM_TUNGSTATE
  specific = 4
FEATURE [App::DocumentObjectGroupPython] C_element023  label="C_element : 010"  # scripted group (container) (typed FeaturePython)
  n = 1
  ref = C_element
FEATURE [App::DocumentObjectGroupPython] O_element025  label="O_element : 013"  # scripted group (container) (typed FeaturePython)
  n = 2
  ref = O_element
FEATURE [App::DocumentObjectGroupPython] G4_CARBON_DIOXIDE  # scripted group (container) (typed FeaturePython)
  Dunit = g/cm3
  Dvalue = 0.00184212
  Group = -> [C_element023,O_element025]
  conduct = 2
  density = 1
  expand = 3
  formula = G4_CARBON_DIOXIDE
  name = G4_CARBON_DIOXIDE
  specific = 4
FEATURE [App::DocumentObjectGroupPython] C_element024  label="C_element : 011"  # scripted group (container) (typed FeaturePython)
  n = 1
  ref = C_element
FEATURE [App::DocumentObjectGroupPython] Cl_element004  label="Cl_element : 4"  # scripted group (container) (typed FeaturePython)
  n = 4
  ref = Cl_element
FEATURE [App::DocumentObjectGroupPython] G4_CARBON_TETRACHLORIDE  # scripted group (container) (typed FeaturePython)
  Dunit = g/cm3
  Dvalue = 1.594
  Group = -> [C_element024,Cl_element004]
  conduct = 2
  density = 1
  expand = 3
  formula = G4_CARBON_TETRACHLORIDE
  name = G4_CARBON_TETRACHLORIDE
  specific = 4
FEATURE [App::DocumentObjectGroupPython] C_element025  label="C_element : 012"  # scripted group (container) (typed FeaturePython)
  n = 6
  ref = C_element
FEATURE [App::DocumentObjectGroupPython] H_element021  label="H_element : 012"  # scripted group (container) (typed FeaturePython)
  n = 10
  ref = H_element
FEATURE [App::DocumentObjectGroupPython] O_element026  label="O_element : 5"  # scripted group (container) (typed FeaturePython)
  n = 5
  ref = O_element
FEATURE [App::DocumentObjectGroupPython] G4_CELLULOSE_CELLOPHANE  # scripted group (container) (typed FeaturePython)
  Dunit = g/cm3
  Dvalue = 1.42
  Group = -> [C_element025,H_element021,O_element026]
  conduct = 2
  density = 1
  expand = 3
  formula = G4_CELLULOSE_CELLOPHANE
  name = G4_CELLULOSE_CELLOPHANE
  specific = 4
FEATURE [App::DocumentObjectGroupPython] H_element022  label="H_element : 0.067"  # scripted group (container) (typed FeaturePython)
  n = 0.067125
FEATURE [App::DocumentObjectGroupPython] C_element026  label="C_element : 0.545"  # scripted group (container) (typed FeaturePython)
  n = 0.545403
FEATURE [App::DocumentObjectGroupPython] O_element027  label="O_element : 0.387"  # scripted group (container) (typed FeaturePython)
  n = 0.387472
FEATURE [App::DocumentObjectGroupPython] G4_CELLULOSE_BUTYRATE  # scripted group (container) (typed FeaturePython)
  Dunit = g/cm3
  Dvalue = 1.2
  Group = -> [H_element022,C_element026,O_element027]
  conduct = 2
  density = 1
  expand = 3
  formula = G4_CELLULOSE_BUTYRATE
  name = G4_CELLULOSE_BUTYRATE
  specific = 4
FEATURE [App::DocumentObjectGroupPython] H_element023  label="H_element : 0.029"  # scripted group (container) (typed FeaturePython)
  n = 0.029216
FEATURE [App::DocumentObjectGroupPython] C_element027  label="C_element : 0.271"  # scripted group (container) (typed FeaturePython)
  n = 0.271296
FEATURE [App::DocumentObjectGroupPython] N_element013  label="N_element : 0.121"  # scripted group (container) (typed FeaturePython)
  n = 0.121276
FEATURE [App::DocumentObjectGroupPython] O_element028  label="O_element : 0.578"  # scripted group (container) (typed FeaturePython)
  n = 0.578212
FEATURE [App::DocumentObjectGroupPython] G4_CELLULOSE_NITRATE  # scripted group (container) (typed FeaturePython)
  Dunit = g/cm3
  Dvalue = 1.49
  Group = -> [H_element023,C_element027,N_element013,O_element028]
  conduct = 2
  density = 1
  expand = 3
  formula = G4_CELLULOSE_NITRATE
  name = G4_CELLULOSE_NITRATE
  specific = 4
FEATURE [App::DocumentObjectGroupPython] H_element024  label="H_element : 0.108"  # scripted group (container) (typed FeaturePython)
  n = 0.107596
FEATURE [App::DocumentObjectGroupPython] N_element014  label="N_element : 0.001"  # scripted group (container) (typed FeaturePython)
  n = 0.0008
FEATURE [App::DocumentObjectGroupPython] O_element029  label="O_element : 0.875"  # scripted group (container) (typed FeaturePython)
  n = 0.874976
FEATURE [App::DocumentObjectGroupPython] S_element008  label="S_element : 0.015"  # scripted group (container) (typed FeaturePython)
  n = 0.014627
FEATURE [App::DocumentObjectGroupPython] Ce_element001  label="Ce_element : 0.002"  # scripted group (container) (typed FeaturePython)
  n = 0.002001
FEATURE [App::DocumentObjectGroupPython] G4_CERIC_SULFATE  # scripted group (container) (typed FeaturePython)
  Dunit = g/cm3
  Dvalue = 1.03
  Group = -> [H_element024,N_element014,O_element029,S_element008,Ce_element001]
  conduct = 2
  density = 1
  expand = 3
  formula = G4_CERIC_SULFATE
  name = G4_CERIC_SULFATE
  specific = 4
FEATURE [App::DocumentObjectGroupPython] Cs_element001  label="Cs_element : 1"  # scripted group (container) (typed FeaturePython)
  n = 1
  ref = Cs_element
FEATURE [App::DocumentObjectGroupPython] F_element006  label="F_element : 1"  # scripted group (container) (typed FeaturePython)
  n = 1
  ref = F_element
FEATURE [App::DocumentObjectGroupPython] G4_CESIUM_FLUORIDE  # scripted group (container) (typed FeaturePython)
  Dunit = g/cm3
  Dvalue = 4.115
  Group = -> [Cs_element001,F_element006]
  conduct = 2
  density = 1
  expand = 3
  formula = G4_CESIUM_FLUORIDE
  name = G4_CESIUM_FLUORIDE
  specific = 4
FEATURE [App::DocumentObjectGroupPython] Cs_element002  label="Cs_element : 002"  # scripted group (container) (typed FeaturePython)
  n = 1
  ref = Cs_element
FEATURE [App::DocumentObjectGroupPython] I_element001  label="I_element : 1"  # scripted group (container) (typed FeaturePython)
  n = 1
  ref = I_element
FEATURE [App::DocumentObjectGroupPython] G4_CESIUM_IODIDE  # scripted group (container) (typed FeaturePython)
  Dunit = g/cm3
  Dvalue = 4.51
  Group = -> [Cs_element002,I_element001]
  conduct = 2
  density = 1
  expand = 3
  formula = G4_CESIUM_IODIDE
  name = G4_CESIUM_IODIDE
  specific = 4
FEATURE [App::DocumentObjectGroupPython] C_element028  label="C_element : 013"  # scripted group (container) (typed FeaturePython)
  n = 6
  ref = C_element
FEATURE [App::DocumentObjectGroupPython] H_element025  label="H_element : 013"  # scripted group (container) (typed FeaturePython)
  n = 5
  ref = H_element
FEATURE [App::DocumentObjectGroupPython] Cl_element005  label="Cl_element : 1"  # scripted group (container) (typed FeaturePython)
  n = 1
  ref = Cl_element
FEATURE [App::DocumentObjectGroupPython] G4_CHLOROBENZENE  # scripted group (container) (typed FeaturePython)
  Dunit = g/cm3
  Dvalue = 1.1058
  Group = -> [C_element028,H_element025,Cl_element005]
  conduct = 2
  density = 1
  expand = 3
  formula = G4_CHLOROBENZENE
  name = G4_CHLOROBENZENE
  specific = 4
FEATURE [App::DocumentObjectGroupPython] C_element029  label="C_element : 014"  # scripted group (container) (typed FeaturePython)
  n = 1
  ref = C_element
FEATURE [App::DocumentObjectGroupPython] H_element026  label="H_element : 1"  # scripted group (container) (typed FeaturePython)
  n = 1
  ref = H_element
FEATURE [App::DocumentObjectGroupPython] Cl_element006  label="Cl_element : 3"  # scripted group (container) (typed FeaturePython)
  n = 3
  ref = Cl_element
FEATURE [App::DocumentObjectGroupPython] G4_CHLOROFORM  # scripted group (container) (typed FeaturePython)
  Dunit = g/cm3
  Dvalue = 1.4832
  Group = -> [C_element029,H_element026,Cl_element006]
  conduct = 2
  density = 1
  expand = 3
  formula = G4_CHLOROFORM
  name = G4_CHLOROFORM
  specific = 4
FEATURE [App::DocumentObjectGroupPython] H_element027  label="H_element : 0.010"  # scripted group (container) (typed FeaturePython)
  n = 0.01
FEATURE [App::DocumentObjectGroupPython] C_element030  label="C_element : 0.001"  # scripted group (container) (typed FeaturePython)
  n = 0.001
FEATURE [App::DocumentObjectGroupPython] O_element030  label="O_element : 0.529"  # scripted group (container) (typed FeaturePython)
  n = 0.529107
FEATURE [App::DocumentObjectGroupPython] Na_element005  label="Na_element : 0.016"  # scripted group (container) (typed FeaturePython)
  n = 0.016
FEATURE [App::DocumentObjectGroupPython] Mg_element003  label="Mg_element : 0.004"  # scripted group (container) (typed FeaturePython)
  n = 0.002
FEATURE [App::DocumentObjectGroupPython] Al_element002  label="Al_element : 0.034"  # scripted group (container) (typed FeaturePython)
  n = 0.033872
FEATURE [App::DocumentObjectGroupPython] Si_element002  label="Si_element : 0.337"  # scripted group (container) (typed FeaturePython)
  n = 0.337021
FEATURE [App::DocumentObjectGroupPython] K_element003  label="K_element : 0.013"  # scripted group (container) (typed FeaturePython)
  n = 0.013
FEATURE [App::DocumentObjectGroupPython] Ca_element010  label="Ca_element : 0.044"  # scripted group (container) (typed FeaturePython)
  n = 0.044
FEATURE [App::DocumentObjectGroupPython] Fe_element002  label="Fe_element : 0.014"  # scripted group (container) (typed FeaturePython)
  n = 0.014
FEATURE [App::DocumentObjectGroupPython] G4_CONCRETE  # scripted group (container) (typed FeaturePython)
  Dunit = g/cm3
  Dvalue = 2.3
  Group = -> [H_element027,C_element030,O_element030,Na_element005,Mg_element003,Al_element002,Si_element002,K_element003,Ca_element010,Fe_element002]
  conduct = 2
  density = 1
  expand = 3
  formula = G4_CONCRETE
  name = G4_CONCRETE
  specific = 4
FEATURE [App::DocumentObjectGroupPython] C_element031  label="C_element : 015"  # scripted group (container) (typed FeaturePython)
  n = 6
  ref = C_element
FEATURE [App::DocumentObjectGroupPython] H_element028  label="H_element : 12"  # scripted group (container) (typed FeaturePython)
  n = 12
  ref = H_element
FEATURE [App::DocumentObjectGroupPython] G4_CYCLOHEXANE  # scripted group (container) (typed FeaturePython)
  Dunit = g/cm3
  Dvalue = 0.779
  Group = -> [C_element031,H_element028]
  conduct = 2
  density = 1
  expand = 3
  formula = G4_CYCLOHEXANE
  name = G4_CYCLOHEXANE
  specific = 4
FEATURE [App::DocumentObjectGroupPython] C_element032  label="C_element : 016"  # scripted group (container) (typed FeaturePython)
  n = 6
  ref = C_element
FEATURE [App::DocumentObjectGroupPython] H_element029  label="H_element : 4"  # scripted group (container) (typed FeaturePython)
  n = 4
  ref = H_element
FEATURE [App::DocumentObjectGroupPython] Cl_element007  label="Cl_element : 2"  # scripted group (container) (typed FeaturePython)
  n = 2
  ref = Cl_element
FEATURE [App::DocumentObjectGroupPython] G4_1_2_DICHLOROBENZENE  label="G4_1.2-DICHLOROBENZENE"  # scripted group (container) (typed FeaturePython)
  Dunit = g/cm3
  Dvalue = 1.3048
  Group = -> [C_element032,H_element029,Cl_element007]
  conduct = 2
  density = 1
  expand = 3
  formula = G4_1.2-DICHLOROBENZENE
  name = G4_1.2-DICHLOROBENZENE
  specific = 4
FEATURE [App::DocumentObjectGroupPython] C_element033  label="C_element : 017"  # scripted group (container) (typed FeaturePython)
  n = 4
  ref = C_element
FEATURE [App::DocumentObjectGroupPython] H_element030  label="H_element : 8"  # scripted group (container) (typed FeaturePython)
  n = 8
  ref = H_element
FEATURE [App::DocumentObjectGroupPython] O_element031  label="O_element : 014"  # scripted group (container) (typed FeaturePython)
  n = 1
  ref = O_element
FEATURE [App::DocumentObjectGroupPython] Cl_element008  label="Cl_element : 005"  # scripted group (container) (typed FeaturePython)
  n = 2
  ref = Cl_element
FEATURE [App::DocumentObjectGroupPython] G4_DICHLORODIETHYL_ETHER  # scripted group (container) (typed FeaturePython)
  Dunit = g/cm3
  Dvalue = 1.2199
  Group = -> [C_element033,H_element030,O_element031,Cl_element008]
  conduct = 2
  density = 1
  expand = 3
  formula = G4_DICHLORODIETHYL_ETHER
  name = G4_DICHLORODIETHYL_ETHER
  specific = 4
FEATURE [App::DocumentObjectGroupPython] C_element034  label="C_element : 018"  # scripted group (container) (typed FeaturePython)
  n = 2
  ref = C_element
FEATURE [App::DocumentObjectGroupPython] H_element031  label="H_element : 014"  # scripted group (container) (typed FeaturePython)
  n = 4
  ref = H_element
FEATURE [App::DocumentObjectGroupPython] Cl_element009  label="Cl_element : 006"  # scripted group (container) (typed FeaturePython)
  n = 2
  ref = Cl_element
FEATURE [App::DocumentObjectGroupPython] G4_1_2_DICHLOROETHANE  label="G4_1.2-DICHLOROETHANE"  # scripted group (container) (typed FeaturePython)
  Dunit = g/cm3
  Dvalue = 1.2351
  Group = -> [C_element034,H_element031,Cl_element009]
  conduct = 2
  density = 1
  expand = 3
  formula = G4_1.2-DICHLOROETHANE
  name = G4_1.2-DICHLOROETHANE
  specific = 4
FEATURE [App::DocumentObjectGroupPython] C_element035  label="C_element : 019"  # scripted group (container) (typed FeaturePython)
  n = 4
  ref = C_element
FEATURE [App::DocumentObjectGroupPython] H_element032  label="H_element : 015"  # scripted group (container) (typed FeaturePython)
  n = 10
  ref = H_element
FEATURE [App::DocumentObjectGroupPython] O_element032  label="O_element : 015"  # scripted group (container) (typed FeaturePython)
  n = 1
  ref = O_element
FEATURE [App::DocumentObjectGroupPython] G4_DIETHYL_ETHER  # scripted group (container) (typed FeaturePython)
  Dunit = g/cm3
  Dvalue = 0.71378
  Group = -> [C_element035,H_element032,O_element032]
  conduct = 2
  density = 1
  expand = 3
  formula = G4_DIETHYL_ETHER
  name = G4_DIETHYL_ETHER
  specific = 4
FEATURE [App::DocumentObjectGroupPython] C_element036  label="C_element : 020"  # scripted group (container) (typed FeaturePython)
  n = 3
  ref = C_element
FEATURE [App::DocumentObjectGroupPython] H_element033  label="H_element : 016"  # scripted group (container) (typed FeaturePython)
  n = 7
  ref = H_element
FEATURE [App::DocumentObjectGroupPython] N_element015  label="N_element : 008"  # scripted group (container) (typed FeaturePython)
  n = 1
  ref = N_element
FEATURE [App::DocumentObjectGroupPython] O_element033  label="O_element : 016"  # scripted group (container) (typed FeaturePython)
  n = 1
  ref = O_element
FEATURE [App::DocumentObjectGroupPython] G4_N_N_DIMETHYL_FORMAMIDE  label="G4_N.N-DIMETHYL_FORMAMIDE"  # scripted group (container) (typed FeaturePython)
  Dunit = g/cm3
  Dvalue = 0.9487
  Group = -> [C_element036,H_element033,N_element015,O_element033]
  conduct = 2
  density = 1
  expand = 3
  formula = G4_N.N-DIMETHYL_FORMAMIDE
  name = G4_N.N-DIMETHYL_FORMAMIDE
  specific = 4
FEATURE [App::DocumentObjectGroupPython] C_element037  label="C_element : 021"  # scripted group (container) (typed FeaturePython)
  n = 2
  ref = C_element
FEATURE [App::DocumentObjectGroupPython] H_element034  label="H_element : 017"  # scripted group (container) (typed FeaturePython)
  n = 6
  ref = H_element
FEATURE [App::DocumentObjectGroupPython] O_element034  label="O_element : 017"  # scripted group (container) (typed FeaturePython)
  n = 1
  ref = O_element
FEATURE [App::DocumentObjectGroupPython] S_element009  label="S_element : 003"  # scripted group (container) (typed FeaturePython)
  n = 1
  ref = S_element
FEATURE [App::DocumentObjectGroupPython] G4_DIMETHYL_SULFOXIDE  # scripted group (container) (typed FeaturePython)
  Dunit = g/cm3
  Dvalue = 1.1014
  Group = -> [C_element037,H_element034,O_element034,S_element009]
  conduct = 2
  density = 1
  expand = 3
  formula = G4_DIMETHYL_SULFOXIDE
  name = G4_DIMETHYL_SULFOXIDE
  specific = 4
FEATURE [App::DocumentObjectGroupPython] C_element038  label="C_element : 022"  # scripted group (container) (typed FeaturePython)
  n = 2
  ref = C_element
FEATURE [App::DocumentObjectGroupPython] H_element035  label="H_element : 018"  # scripted group (container) (typed FeaturePython)
  n = 6
  ref = H_element
FEATURE [App::DocumentObjectGroupPython] G4_ETHANE  # scripted group (container) (typed FeaturePython)
  Dunit = g/cm3
  Dvalue = 0.00125324
  Group = -> [C_element038,H_element035]
  conduct = 2
  density = 1
  expand = 3
  formula = G4_ETHANE
  name = G4_ETHANE
  specific = 4
FEATURE [App::DocumentObjectGroupPython] C_element039  label="C_element : 023"  # scripted group (container) (typed FeaturePython)
  n = 2
  ref = C_element
FEATURE [App::DocumentObjectGroupPython] H_element036  label="H_element : 019"  # scripted group (container) (typed FeaturePython)
  n = 6
  ref = H_element
FEATURE [App::DocumentObjectGroupPython] O_element035  label="O_element : 018"  # scripted group (container) (typed FeaturePython)
  n = 1
  ref = O_element
FEATURE [App::DocumentObjectGroupPython] G4_ETHYL_ALCOHOL  # scripted group (container) (typed FeaturePython)
  Dunit = g/cm3
  Dvalue = 0.7893
  Group = -> [C_element039,H_element036,O_element035]
  conduct = 2
  density = 1
  expand = 3
  formula = G4_ETHYL_ALCOHOL
  name = G4_ETHYL_ALCOHOL
  specific = 4
FEATURE [App::DocumentObjectGroupPython] H_element037  label="H_element : 0.090"  # scripted group (container) (typed FeaturePython)
  n = 0.090027
FEATURE [App::DocumentObjectGroupPython] C_element040  label="C_element : 0.585"  # scripted group (container) (typed FeaturePython)
  n = 0.585182
FEATURE [App::DocumentObjectGroupPython] O_element036  label="O_element : 0.325"  # scripted group (container) (typed FeaturePython)
  n = 0.324791
FEATURE [App::DocumentObjectGroupPython] G4_ETHYL_CELLULOSE  # scripted group (container) (typed FeaturePython)
  Dunit = g/cm3
  Dvalue = 1.13
  Group = -> [H_element037,C_element040,O_element036]
  conduct = 2
  density = 1
  expand = 3
  formula = G4_ETHYL_CELLULOSE
  name = G4_ETHYL_CELLULOSE
  specific = 4
FEATURE [App::DocumentObjectGroupPython] C_element041  label="C_element : 024"  # scripted group (container) (typed FeaturePython)
  n = 2
  ref = C_element
FEATURE [App::DocumentObjectGroupPython] H_element038  label="H_element : 020"  # scripted group (container) (typed FeaturePython)
  n = 4
  ref = H_element
FEATURE [App::DocumentObjectGroupPython] G4_ETHYLENE  # scripted group (container) (typed FeaturePython)
  Dunit = g/cm3
  Dvalue = 0.00117497
  Group = -> [C_element041,H_element038]
  conduct = 2
  density = 1
  expand = 3
  formula = G4_ETHYLENE
  name = G4_ETHYLENE
  specific = 4
FEATURE [App::DocumentObjectGroupPython] H_element039  label="H_element : 0.096"  # scripted group (container) (typed FeaturePython)
  n = 0.096
FEATURE [App::DocumentObjectGroupPython] C_element042  label="C_element : 0.195"  # scripted group (container) (typed FeaturePython)
  n = 0.195
FEATURE [App::DocumentObjectGroupPython] N_element016  label="N_element : 0.057"  # scripted group (container) (typed FeaturePython)
  n = 0.057
FEATURE [App::DocumentObjectGroupPython] O_element037  label="O_element : 0.646"  # scripted group (container) (typed FeaturePython)
  n = 0.646
FEATURE [App::DocumentObjectGroupPython] Na_element006  label="Na_element : 0.017"  # scripted group (container) (typed FeaturePython)
  n = 0.001
FEATURE [App::DocumentObjectGroupPython] P_element005  label="P_element : 0.104"  # scripted group (container) (typed FeaturePython)
  n = 0.001
FEATURE [App::DocumentObjectGroupPython] S_element010  label="S_element : 0.016"  # scripted group (container) (typed FeaturePython)
  n = 0.003
FEATURE [App::DocumentObjectGroupPython] Cl_element010  label="Cl_element : 0.005"  # scripted group (container) (typed FeaturePython)
  n = 0.001
FEATURE [App::DocumentObjectGroupPython] G4_EYE_LENS_ICRP  # scripted group (container) (typed FeaturePython)
  Dunit = g/cm3
  Dvalue = 1.07
  Group = -> [H_element039,C_element042,N_element016,O_element037,Na_element006,P_element005,S_element010,Cl_element010]
  conduct = 2
  density = 1
  expand = 3
  formula = G4_EYE_LENS_ICRP
  name = G4_EYE_LENS_ICRP
  specific = 4
FEATURE [App::DocumentObjectGroupPython] Fe_element003  label="Fe_element : 2"  # scripted group (container) (typed FeaturePython)
  n = 2
  ref = Fe_element
FEATURE [App::DocumentObjectGroupPython] O_element038  label="O_element : 019"  # scripted group (container) (typed FeaturePython)
  n = 3
  ref = O_element
FEATURE [App::DocumentObjectGroupPython] G4_FERRIC_OXIDE  # scripted group (container) (typed FeaturePython)
  Dunit = g/cm3
  Dvalue = 5.2
  Group = -> [Fe_element003,O_element038]
  conduct = 2
  density = 1
  expand = 3
  formula = G4_FERRIC_OXIDE
  name = G4_FERRIC_OXIDE
  specific = 4
FEATURE [App::DocumentObjectGroupPython] Fe_element004  label="Fe_element : 1"  # scripted group (container) (typed FeaturePython)
  n = 1
  ref = Fe_element
FEATURE [App::DocumentObjectGroupPython] B_element003  label="B_element : 1"  # scripted group (container) (typed FeaturePython)
  n = 1
  ref = B_element
FEATURE [App::DocumentObjectGroupPython] G4_FERROBORIDE  # scripted group (container) (typed FeaturePython)
  Dunit = g/cm3
  Dvalue = 7.15
  Group = -> [Fe_element004,B_element003]
  conduct = 2
  density = 1
  expand = 3
  formula = G4_FERROBORIDE
  name = G4_FERROBORIDE
  specific = 4
FEATURE [App::DocumentObjectGroupPython] Fe_element005  label="Fe_element : 003"  # scripted group (container) (typed FeaturePython)
  n = 1
  ref = Fe_element
FEATURE [App::DocumentObjectGroupPython] O_element039  label="O_element : 020"  # scripted group (container) (typed FeaturePython)
  n = 1
  ref = O_element
FEATURE [App::DocumentObjectGroupPython] G4_FERROUS_OXIDE  # scripted group (container) (typed FeaturePython)
  Dunit = g/cm3
  Dvalue = 5.7
  Group = -> [Fe_element005,O_element039]
  conduct = 2
  density = 1
  expand = 3
  formula = G4_FERROUS_OXIDE
  name = G4_FERROUS_OXIDE
  specific = 4
FEATURE [App::DocumentObjectGroupPython] H_element040  label="H_element : 0.115"  # scripted group (container) (typed FeaturePython)
  n = 0.108259
FEATURE [App::DocumentObjectGroupPython] N_element017  label="N_element : 0.000"  # scripted group (container) (typed FeaturePython)
  n = 2.7e-05
FEATURE [App::DocumentObjectGroupPython] O_element040  label="O_element : 0.879"  # scripted group (container) (typed FeaturePython)
  n = 0.878636
FEATURE [App::DocumentObjectGroupPython] Na_element007  label="Na_element : 0.000"  # scripted group (container) (typed FeaturePython)
  n = 2.2e-05
FEATURE [App::DocumentObjectGroupPython] S_element011  label="S_element : 0.013"  # scripted group (container) (typed FeaturePython)
  n = 0.012968
FEATURE [App::DocumentObjectGroupPython] Cl_element011  label="Cl_element : 0.000"  # scripted group (container) (typed FeaturePython)
  n = 3.4e-05
FEATURE [App::DocumentObjectGroupPython] Fe_element006  label="Fe_element : 0.000"  # scripted group (container) (typed FeaturePython)
  n = 5.4e-05
FEATURE [App::DocumentObjectGroupPython] G4_FERROUS_SULFATE  # scripted group (container) (typed FeaturePython)
  Dunit = g/cm3
  Dvalue = 1.024
  Group = -> [H_element040,N_element017,O_element040,Na_element007,S_element011,Cl_element011,Fe_element006]
  conduct = 2
  density = 1
  expand = 3
  formula = G4_FERROUS_SULFATE
  name = G4_FERROUS_SULFATE
  specific = 4
FEATURE [App::DocumentObjectGroupPython] C_element043  label="C_element : 0.099"  # scripted group (container) (typed FeaturePython)
  n = 0.099335
FEATURE [App::DocumentObjectGroupPython] F_element007  label="F_element : 0.314"  # scripted group (container) (typed FeaturePython)
  n = 0.314247
FEATURE [App::DocumentObjectGroupPython] Cl_element012  label="Cl_element : 0.586"  # scripted group (container) (typed FeaturePython)
  n = 0.586418
FEATURE [App::DocumentObjectGroupPython] G4_FREON_12  label="G4_FREON-12"  # scripted group (container) (typed FeaturePython)
  Dunit = g/cm3
  Dvalue = 1.12
  Group = -> [C_element043,F_element007,Cl_element012]
  conduct = 2
  density = 1
  expand = 3
  formula = G4_FREON-12
  name = G4_FREON-12
  specific = 4
FEATURE [App::DocumentObjectGroupPython] C_element044  label="C_element : 0.057"  # scripted group (container) (typed FeaturePython)
  n = 0.057245
FEATURE [App::DocumentObjectGroupPython] F_element008  label="F_element : 0.181"  # scripted group (container) (typed FeaturePython)
  n = 0.181096
FEATURE [App::DocumentObjectGroupPython] Br_element001  label="Br_element : 0.762"  # scripted group (container) (typed FeaturePython)
  n = 0.761659
FEATURE [App::DocumentObjectGroupPython] G4_FREON_12B2  label="G4_FREON-12B2"  # scripted group (container) (typed FeaturePython)
  Dunit = g/cm3
  Dvalue = 1.8
  Group = -> [C_element044,F_element008,Br_element001]
  conduct = 2
  density = 1
  expand = 3
  formula = G4_FREON-12B2
  name = G4_FREON-12B2
  specific = 4
FEATURE [App::DocumentObjectGroupPython] C_element045  label="C_element : 0.115"  # scripted group (container) (typed FeaturePython)
  n = 0.114983
FEATURE [App::DocumentObjectGroupPython] F_element009  label="F_element : 0.546"  # scripted group (container) (typed FeaturePython)
  n = 0.545621
FEATURE [App::DocumentObjectGroupPython] Cl_element013  label="Cl_element : 0.339"  # scripted group (container) (typed FeaturePython)
  n = 0.339396
FEATURE [App::DocumentObjectGroupPython] G4_FREON_13  label="G4_FREON-13"  # scripted group (container) (typed FeaturePython)
  Dunit = g/cm3
  Dvalue = 0.95
  Group = -> [C_element045,F_element009,Cl_element013]
  conduct = 2
  density = 1
  expand = 3
  formula = G4_FREON-13
  name = G4_FREON-13
  specific = 4
FEATURE [App::DocumentObjectGroupPython] C_element046  label="C_element : 025"  # scripted group (container) (typed FeaturePython)
  n = 1
  ref = C_element
FEATURE [App::DocumentObjectGroupPython] F_element010  label="F_element : 3"  # scripted group (container) (typed FeaturePython)
  n = 3
  ref = F_element
FEATURE [App::DocumentObjectGroupPython] Br_element002  label="Br_element : 1"  # scripted group (container) (typed FeaturePython)
  n = 1
  ref = Br_element
FEATURE [App::DocumentObjectGroupPython] G4_FREON_13B1  label="G4_FREON-13B1"  # scripted group (container) (typed FeaturePython)
  Dunit = g/cm3
  Dvalue = 1.5
  Group = -> [C_element046,F_element010,Br_element002]
  conduct = 2
  density = 1
  expand = 3
  formula = G4_FREON-13B1
  name = G4_FREON-13B1
  specific = 4
FEATURE [App::DocumentObjectGroupPython] C_element047  label="C_element : 0.061"  # scripted group (container) (typed FeaturePython)
  n = 0.061309
FEATURE [App::DocumentObjectGroupPython] F_element011  label="F_element : 0.291"  # scripted group (container) (typed FeaturePython)
  n = 0.290924
FEATURE [App::DocumentObjectGroupPython] I_element002  label="I_element : 0.648"  # scripted group (container) (typed FeaturePython)
  n = 0.647767
FEATURE [App::DocumentObjectGroupPython] G4_FREON_13I1  label="G4_FREON-13I1"  # scripted group (container) (typed FeaturePython)
  Dunit = g/cm3
  Dvalue = 1.8
  Group = -> [C_element047,F_element011,I_element002]
  conduct = 2
  density = 1
  expand = 3
  formula = G4_FREON-13I1
  name = G4_FREON-13I1
  specific = 4
FEATURE [App::DocumentObjectGroupPython] Gd_element001  label="Gd_element : 2"  # scripted group (container) (typed FeaturePython)
  n = 2
  ref = Gd_element
FEATURE [App::DocumentObjectGroupPython] O_element041  label="O_element : 021"  # scripted group (container) (typed FeaturePython)
  n = 2
  ref = O_element
FEATURE [App::DocumentObjectGroupPython] S_element012  label="S_element : 004"  # scripted group (container) (typed FeaturePython)
  n = 1
  ref = S_element
FEATURE [App::DocumentObjectGroupPython] G4_GADOLINIUM_OXYSULFIDE  # scripted group (container) (typed FeaturePython)
  Dunit = g/cm3
  Dvalue = 7.44
  Group = -> [Gd_element001,O_element041,S_element012]
  conduct = 2
  density = 1
  expand = 3
  formula = G4_GADOLINIUM_OXYSULFIDE
  name = G4_GADOLINIUM_OXYSULFIDE
  specific = 4
FEATURE [App::DocumentObjectGroupPython] Ga_element001  label="Ga_element : 1"  # scripted group (container) (typed FeaturePython)
  n = 1
  ref = Ga_element
FEATURE [App::DocumentObjectGroupPython] As_element001  label="As_element : 1"  # scripted group (container) (typed FeaturePython)
  n = 1
  ref = As_element
FEATURE [App::DocumentObjectGroupPython] G4_GALLIUM_ARSENIDE  # scripted group (container) (typed FeaturePython)
  Dunit = g/cm3
  Dvalue = 5.31
  Group = -> [Ga_element001,As_element001]
  conduct = 2
  density = 1
  expand = 3
  formula = G4_GALLIUM_ARSENIDE
  name = G4_GALLIUM_ARSENIDE
  specific = 4
FEATURE [App::DocumentObjectGroupPython] H_element041  label="H_element : 0.081"  # scripted group (container) (typed FeaturePython)
  n = 0.08118
FEATURE [App::DocumentObjectGroupPython] C_element048  label="C_element : 0.416"  # scripted group (container) (typed FeaturePython)
  n = 0.41606
FEATURE [App::DocumentObjectGroupPython] N_element018  label="N_element : 0.111"  # scripted group (container) (typed FeaturePython)
  n = 0.11124
FEATURE [App::DocumentObjectGroupPython] O_element042  label="O_element : 0.381"  # scripted group (container) (typed FeaturePython)
  n = 0.38064
FEATURE [App::DocumentObjectGroupPython] S_element013  label="S_element : 0.011"  # scripted group (container) (typed FeaturePython)
  n = 0.01088
FEATURE [App::DocumentObjectGroupPython] G4_GEL_PHOTO_EMULSION  # scripted group (container) (typed FeaturePython)
  Dunit = g/cm3
  Dvalue = 1.2914
  Group = -> [H_element041,C_element048,N_element018,O_element042,S_element013]
  conduct = 2
  density = 1
  expand = 3
  formula = G4_GEL_PHOTO_EMULSION
  name = G4_GEL_PHOTO_EMULSION
  specific = 4
FEATURE [App::DocumentObjectGroupPython] B_element004  label="B_element : 0.040"  # scripted group (container) (typed FeaturePython)
  n = 0.0400639
FEATURE [App::DocumentObjectGroupPython] O_element043  label="O_element : 0.540"  # scripted group (container) (typed FeaturePython)
  n = 0.539561
FEATURE [App::DocumentObjectGroupPython] Na_element008  label="Na_element : 0.028"  # scripted group (container) (typed FeaturePython)
  n = 0.0281909
FEATURE [App::DocumentObjectGroupPython] Al_element003  label="Al_element : 0.012"  # scripted group (container) (typed FeaturePython)
  n = 0.011644
FEATURE [App::DocumentObjectGroupPython] Si_element003  label="Si_element : 0.377"  # scripted group (container) (typed FeaturePython)
  n = 0.377219
FEATURE [App::DocumentObjectGroupPython] K_element004  label="K_element : 0.014"  # scripted group (container) (typed FeaturePython)
  n = 0.00332099
FEATURE [App::DocumentObjectGroupPython] G4_Pyrex_Glass  # scripted group (container) (typed FeaturePython)
  Dunit = g/cm3
  Dvalue = 2.23
  Group = -> [B_element004,O_element043,Na_element008,Al_element003,Si_element003,K_element004]
  conduct = 2
  density = 1
  expand = 3
  formula = G4_Pyrex_Glass
  name = G4_Pyrex_Glass
  specific = 4
FEATURE [App::DocumentObjectGroupPython] O_element044  label="O_element : 0.156"  # scripted group (container) (typed FeaturePython)
  n = 0.156453
FEATURE [App::DocumentObjectGroupPython] Si_element004  label="Si_element : 0.081"  # scripted group (container) (typed FeaturePython)
  n = 0.080866
FEATURE [App::DocumentObjectGroupPython] Ti_element001  label="Ti_element : 0.008"  # scripted group (container) (typed FeaturePython)
  n = 0.008092
FEATURE [App::DocumentObjectGroupPython] As_element002  label="As_element : 0.003"  # scripted group (container) (typed FeaturePython)
  n = 0.002651
FEATURE [App::DocumentObjectGroupPython] Pb_element001  label="Pb_element : 0.752"  # scripted group (container) (typed FeaturePython)
  n = 0.751938
FEATURE [App::DocumentObjectGroupPython] G4_GLASS_LEAD  # scripted group (container) (typed FeaturePython)
  Dunit = g/cm3
  Dvalue = 6.22
  Group = -> [O_element044,Si_element004,Ti_element001,As_element002,Pb_element001]
  conduct = 2
  density = 1
  expand = 3
  formula = G4_GLASS_LEAD
  name = G4_GLASS_LEAD
  specific = 4
FEATURE [App::DocumentObjectGroupPython] O_element045  label="O_element : 0.460"  # scripted group (container) (typed FeaturePython)
  n = 0.4598
FEATURE [App::DocumentObjectGroupPython] Na_element009  label="Na_element : 0.096"  # scripted group (container) (typed FeaturePython)
  n = 0.0964411
FEATURE [App::DocumentObjectGroupPython] Si_element005  label="Si_element : 0.378"  # scripted group (container) (typed FeaturePython)
  n = 0.336553
FEATURE [App::DocumentObjectGroupPython] Ca_element011  label="Ca_element : 0.107"  # scripted group (container) (typed FeaturePython)
  n = 0.107205
FEATURE [App::DocumentObjectGroupPython] G4_GLASS_PLATE  # scripted group (container) (typed FeaturePython)
  Dunit = g/cm3
  Dvalue = 2.4
  Group = -> [O_element045,Na_element009,Si_element005,Ca_element011]
  conduct = 2
  density = 1
  expand = 3
  formula = G4_GLASS_PLATE
  name = G4_GLASS_PLATE
  specific = 4
FEATURE [App::DocumentObjectGroupPython] C_element049  label="C_element : 026"  # scripted group (container) (typed FeaturePython)
  n = 5
  ref = C_element
FEATURE [App::DocumentObjectGroupPython] H_element042  label="H_element : 021"  # scripted group (container) (typed FeaturePython)
  n = 10
  ref = H_element
FEATURE [App::DocumentObjectGroupPython] N_element019  label="N_element : 2"  # scripted group (container) (typed FeaturePython)
  n = 2
  ref = N_element
FEATURE [App::DocumentObjectGroupPython] O_element046  label="O_element : 022"  # scripted group (container) (typed FeaturePython)
  n = 3
  ref = O_element
FEATURE [App::DocumentObjectGroupPython] G4_GLUTAMINE  # scripted group (container) (typed FeaturePython)
  Dunit = g/cm3
  Dvalue = 1.46
  Group = -> [C_element049,H_element042,N_element019,O_element046]
  conduct = 2
  density = 1
  expand = 3
  formula = G4_GLUTAMINE
  name = G4_GLUTAMINE
  specific = 4
FEATURE [App::DocumentObjectGroupPython] C_element050  label="C_element : 027"  # scripted group (container) (typed FeaturePython)
  n = 3
  ref = C_element
FEATURE [App::DocumentObjectGroupPython] H_element043  label="H_element : 022"  # scripted group (container) (typed FeaturePython)
  n = 8
  ref = H_element
FEATURE [App::DocumentObjectGroupPython] O_element047  label="O_element : 023"  # scripted group (container) (typed FeaturePython)
  n = 3
  ref = O_element
FEATURE [App::DocumentObjectGroupPython] G4_GLYCEROL  # scripted group (container) (typed FeaturePython)
  Dunit = g/cm3
  Dvalue = 1.2613
  Group = -> [C_element050,H_element043,O_element047]
  conduct = 2
  density = 1
  expand = 3
  formula = G4_GLYCEROL
  name = G4_GLYCEROL
  specific = 4
FEATURE [App::DocumentObjectGroupPython] C_element051  label="C_element : 028"  # scripted group (container) (typed FeaturePython)
  n = 5
  ref = C_element
FEATURE [App::DocumentObjectGroupPython] H_element044  label="H_element : 023"  # scripted group (container) (typed FeaturePython)
  n = 5
  ref = H_element
FEATURE [App::DocumentObjectGroupPython] N_element020  label="N_element : 009"  # scripted group (container) (typed FeaturePython)
  n = 5
  ref = N_element
FEATURE [App::DocumentObjectGroupPython] O_element048  label="O_element : 024"  # scripted group (container) (typed FeaturePython)
  n = 1
  ref = O_element
FEATURE [App::DocumentObjectGroupPython] G4_GUANINE  # scripted group (container) (typed FeaturePython)
  Dunit = g/cm3
  Dvalue = 2.2
  Group = -> [C_element051,H_element044,N_element020,O_element048]
  conduct = 2
  density = 1
  expand = 3
  formula = G4_GUANINE
  name = G4_GUANINE
  specific = 4
FEATURE [App::DocumentObjectGroupPython] Ca_element012  label="Ca_element : 006"  # scripted group (container) (typed FeaturePython)
  n = 1
  ref = Ca_element
FEATURE [App::DocumentObjectGroupPython] S_element014  label="S_element : 005"  # scripted group (container) (typed FeaturePython)
  n = 1
  ref = S_element
FEATURE [App::DocumentObjectGroupPython] O_element049  label="O_element : 6"  # scripted group (container) (typed FeaturePython)
  n = 6
  ref = O_element
FEATURE [App::DocumentObjectGroupPython] H_element045  label="H_element : 024"  # scripted group (container) (typed FeaturePython)
  n = 4
  ref = H_element
FEATURE [App::DocumentObjectGroupPython] G4_GYPSUM  # scripted group (container) (typed FeaturePython)
  Dunit = g/cm3
  Dvalue = 2.32
  Group = -> [Ca_element012,S_element014,O_element049,H_element045]
  conduct = 2
  density = 1
  expand = 3
  formula = G4_GYPSUM
  name = G4_GYPSUM
  specific = 4
FEATURE [App::DocumentObjectGroupPython] C_element052  label="C_element : 7"  # scripted group (container) (typed FeaturePython)
  n = 7
  ref = C_element
FEATURE [App::DocumentObjectGroupPython] H_element046  label="H_element : 16"  # scripted group (container) (typed FeaturePython)
  n = 16
  ref = H_element
FEATURE [App::DocumentObjectGroupPython] G4_N_HEPTANE  label="G4_N-HEPTANE"  # scripted group (container) (typed FeaturePython)
  Dunit = g/cm3
  Dvalue = 0.68376
  Group = -> [C_element052,H_element046]
  conduct = 2
  density = 1
  expand = 3
  formula = G4_N-HEPTANE
  name = G4_N-HEPTANE
  specific = 4
FEATURE [App::DocumentObjectGroupPython] C_element053  label="C_element : 029"  # scripted group (container) (typed FeaturePython)
  n = 6
  ref = C_element
FEATURE [App::DocumentObjectGroupPython] H_element047  label="H_element : 14"  # scripted group (container) (typed FeaturePython)
  n = 14
  ref = H_element
FEATURE [App::DocumentObjectGroupPython] G4_N_HEXANE  label="G4_N-HEXANE"  # scripted group (container) (typed FeaturePython)
  Dunit = g/cm3
  Dvalue = 0.6603
  Group = -> [C_element053,H_element047]
  conduct = 2
  density = 1
  expand = 3
  formula = G4_N-HEXANE
  name = G4_N-HEXANE
  specific = 4
FEATURE [App::DocumentObjectGroupPython] C_element054  label="C_element : 22"  # scripted group (container) (typed FeaturePython)
  n = 22
  ref = C_element
FEATURE [App::DocumentObjectGroupPython] H_element048  label="H_element : 025"  # scripted group (container) (typed FeaturePython)
  n = 10
  ref = H_element
FEATURE [App::DocumentObjectGroupPython] N_element021  label="N_element : 010"  # scripted group (container) (typed FeaturePython)
  n = 2
  ref = N_element
FEATURE [App::DocumentObjectGroupPython] O_element050  label="O_element : 025"  # scripted group (container) (typed FeaturePython)
  n = 5
  ref = O_element
FEATURE [App::DocumentObjectGroupPython] G4_KAPTON  # scripted group (container) (typed FeaturePython)
  Dunit = g/cm3
  Dvalue = 1.42
  Group = -> [C_element054,H_element048,N_element021,O_element050]
  conduct = 2
  density = 1
  expand = 3
  formula = G4_KAPTON
  name = G4_KAPTON
  specific = 4
FEATURE [App::DocumentObjectGroupPython] La_element001  label="La_element : 1"  # scripted group (container) (typed FeaturePython)
  n = 1
  ref = La_element
FEATURE [App::DocumentObjectGroupPython] Br_element003  label="Br_element : 002"  # scripted group (container) (typed FeaturePython)
  n = 1
  ref = Br_element
FEATURE [App::DocumentObjectGroupPython] O_element051  label="O_element : 026"  # scripted group (container) (typed FeaturePython)
  n = 1
  ref = O_element
FEATURE [App::DocumentObjectGroupPython] G4_LANTHANUM_OXYBROMIDE  # scripted group (container) (typed FeaturePython)
  Dunit = g/cm3
  Dvalue = 6.28
  Group = -> [La_element001,Br_element003,O_element051]
  conduct = 2
  density = 1
  expand = 3
  formula = G4_LANTHANUM_OXYBROMIDE
  name = G4_LANTHANUM_OXYBROMIDE
  specific = 4
FEATURE [App::DocumentObjectGroupPython] La_element002  label="La_element : 2"  # scripted group (container) (typed FeaturePython)
  n = 2
  ref = La_element
FEATURE [App::DocumentObjectGroupPython] O_element052  label="O_element : 027"  # scripted group (container) (typed FeaturePython)
  n = 2
  ref = O_element
FEATURE [App::DocumentObjectGroupPython] S_element015  label="S_element : 006"  # scripted group (container) (typed FeaturePython)
  n = 1
  ref = S_element
FEATURE [App::DocumentObjectGroupPython] G4_LANTHANUM_OXYSULFIDE  # scripted group (container) (typed FeaturePython)
  Dunit = g/cm3
  Dvalue = 5.86
  Group = -> [La_element002,O_element052,S_element015]
  conduct = 2
  density = 1
  expand = 3
  formula = G4_LANTHANUM_OXYSULFIDE
  name = G4_LANTHANUM_OXYSULFIDE
  specific = 4
FEATURE [App::DocumentObjectGroupPython] O_element053  label="O_element : 0.072"  # scripted group (container) (typed FeaturePython)
  n = 0.071682
FEATURE [App::DocumentObjectGroupPython] Pb_element002  label="Pb_element : 0.928"  # scripted group (container) (typed FeaturePython)
  n = 0.928318
FEATURE [App::DocumentObjectGroupPython] G4_LEAD_OXIDE  # scripted group (container) (typed FeaturePython)
  Dunit = g/cm3
  Dvalue = 9.53
  Group = -> [O_element053,Pb_element002]
  conduct = 2
  density = 1
  expand = 3
  formula = G4_LEAD_OXIDE
  name = G4_LEAD_OXIDE
  specific = 4
FEATURE [App::DocumentObjectGroupPython] Li_element001  label="Li_element : 1"  # scripted group (container) (typed FeaturePython)
  n = 1
  ref = Li_element
FEATURE [App::DocumentObjectGroupPython] N_element022  label="N_element : 011"  # scripted group (container) (typed FeaturePython)
  n = 1
  ref = N_element
FEATURE [App::DocumentObjectGroupPython] H_element049  label="H_element : 026"  # scripted group (container) (typed FeaturePython)
  n = 2
  ref = H_element
FEATURE [App::DocumentObjectGroupPython] G4_LITHIUM_AMIDE  # scripted group (container) (typed FeaturePython)
  Dunit = g/cm3
  Dvalue = 1.178
  Group = -> [Li_element001,N_element022,H_element049]
  conduct = 2
  density = 1
  expand = 3
  formula = G4_LITHIUM_AMIDE
  name = G4_LITHIUM_AMIDE
  specific = 4
FEATURE [App::DocumentObjectGroupPython] Li_element002  label="Li_element : 2"  # scripted group (container) (typed FeaturePython)
  n = 2
  ref = Li_element
FEATURE [App::DocumentObjectGroupPython] C_element055  label="C_element : 030"  # scripted group (container) (typed FeaturePython)
  n = 1
  ref = C_element
FEATURE [App::DocumentObjectGroupPython] O_element054  label="O_element : 028"  # scripted group (container) (typed FeaturePython)
  n = 3
  ref = O_element
FEATURE [App::DocumentObjectGroupPython] G4_LITHIUM_CARBONATE  # scripted group (container) (typed FeaturePython)
  Dunit = g/cm3
  Dvalue = 2.11
  Group = -> [Li_element002,C_element055,O_element054]
  conduct = 2
  density = 1
  expand = 3
  formula = G4_LITHIUM_CARBONATE
  name = G4_LITHIUM_CARBONATE
  specific = 4
FEATURE [App::DocumentObjectGroupPython] Li_element003  label="Li_element : 003"  # scripted group (container) (typed FeaturePython)
  n = 1
  ref = Li_element
FEATURE [App::DocumentObjectGroupPython] F_element012  label="F_element : 004"  # scripted group (container) (typed FeaturePython)
  n = 1
  ref = F_element
FEATURE [App::DocumentObjectGroupPython] G4_LITHIUM_FLUORIDE  # scripted group (container) (typed FeaturePython)
  Dunit = g/cm3
  Dvalue = 2.635
  Group = -> [Li_element003,F_element012]
  conduct = 2
  density = 1
  expand = 3
  formula = G4_LITHIUM_FLUORIDE
  name = G4_LITHIUM_FLUORIDE
  specific = 4
FEATURE [App::DocumentObjectGroupPython] Li_element004  label="Li_element : 004"  # scripted group (container) (typed FeaturePython)
  n = 1
  ref = Li_element
FEATURE [App::DocumentObjectGroupPython] H_element050  label="H_element : 027"  # scripted group (container) (typed FeaturePython)
  n = 1
  ref = H_element
FEATURE [App::DocumentObjectGroupPython] G4_LITHIUM_HYDRIDE  # scripted group (container) (typed FeaturePython)
  Dunit = g/cm3
  Dvalue = 0.82
  Group = -> [Li_element004,H_element050]
  conduct = 2
  density = 1
  expand = 3
  formula = G4_LITHIUM_HYDRIDE
  name = G4_LITHIUM_HYDRIDE
  specific = 4
FEATURE [App::DocumentObjectGroupPython] Li_element005  label="Li_element : 005"  # scripted group (container) (typed FeaturePython)
  n = 1
  ref = Li_element
FEATURE [App::DocumentObjectGroupPython] I_element003  label="I_element : 002"  # scripted group (container) (typed FeaturePython)
  n = 1
  ref = I_element
FEATURE [App::DocumentObjectGroupPython] G4_LITHIUM_IODIDE  # scripted group (container) (typed FeaturePython)
  Dunit = g/cm3
  Dvalue = 3.494
  Group = -> [Li_element005,I_element003]
  conduct = 2
  density = 1
  expand = 3
  formula = G4_LITHIUM_IODIDE
  name = G4_LITHIUM_IODIDE
  specific = 4
FEATURE [App::DocumentObjectGroupPython] Li_element006  label="Li_element : 006"  # scripted group (container) (typed FeaturePython)
  n = 2
  ref = Li_element
FEATURE [App::DocumentObjectGroupPython] O_element055  label="O_element : 029"  # scripted group (container) (typed FeaturePython)
  n = 1
  ref = O_element
FEATURE [App::DocumentObjectGroupPython] G4_LITHIUM_OXIDE  # scripted group (container) (typed FeaturePython)
  Dunit = g/cm3
  Dvalue = 2.013
  Group = -> [Li_element006,O_element055]
  conduct = 2
  density = 1
  expand = 3
  formula = G4_LITHIUM_OXIDE
  name = G4_LITHIUM_OXIDE
  specific = 4
FEATURE [App::DocumentObjectGroupPython] Li_element007  label="Li_element : 007"  # scripted group (container) (typed FeaturePython)
  n = 2
  ref = Li_element
FEATURE [App::DocumentObjectGroupPython] B_element005  label="B_element : 005"  # scripted group (container) (typed FeaturePython)
  n = 4
  ref = B_element
FEATURE [App::DocumentObjectGroupPython] O_element056  label="O_element : 7"  # scripted group (container) (typed FeaturePython)
  n = 7
  ref = O_element
FEATURE [App::DocumentObjectGroupPython] G4_LITHIUM_TETRABORATE  # scripted group (container) (typed FeaturePython)
  Dunit = g/cm3
  Dvalue = 2.44
  Group = -> [Li_element007,B_element005,O_element056]
  conduct = 2
  density = 1
  expand = 3
  formula = G4_LITHIUM_TETRABORATE
  name = G4_LITHIUM_TETRABORATE
  specific = 4
FEATURE [App::DocumentObjectGroupPython] H_element051  label="H_element : 0.105"  # scripted group (container) (typed FeaturePython)
  n = 0.105
FEATURE [App::DocumentObjectGroupPython] C_element056  label="C_element : 0.083"  # scripted group (container) (typed FeaturePython)
  n = 0.083
FEATURE [App::DocumentObjectGroupPython] N_element023  label="N_element : 0.023"  # scripted group (container) (typed FeaturePython)
  n = 0.023
FEATURE [App::DocumentObjectGroupPython] O_element057  label="O_element : 0.779"  # scripted group (container) (typed FeaturePython)
  n = 0.779
FEATURE [App::DocumentObjectGroupPython] Na_element010  label="Na_element : 0.097"  # scripted group (container) (typed FeaturePython)
  n = 0.002
FEATURE [App::DocumentObjectGroupPython] P_element006  label="P_element : 0.105"  # scripted group (container) (typed FeaturePython)
  n = 0.001
FEATURE [App::DocumentObjectGroupPython] S_element016  label="S_element : 0.017"  # scripted group (container) (typed FeaturePython)
  n = 0.002
FEATURE [App::DocumentObjectGroupPython] Cl_element014  label="Cl_element : 0.587"  # scripted group (container) (typed FeaturePython)
  n = 0.003
FEATURE [App::DocumentObjectGroupPython] K_element005  label="K_element : 0.015"  # scripted group (container) (typed FeaturePython)
  n = 0.002
FEATURE [App::DocumentObjectGroupPython] G4_LUNG_ICRP  # scripted group (container) (typed FeaturePython)
  Dunit = g/cm3
  Dvalue = 1.04
  Group = -> [H_element051,C_element056,N_element023,O_element057,Na_element010,P_element006,S_element016,Cl_element014,K_element005]
  conduct = 2
  density = 1
  expand = 3
  formula = G4_LUNG_ICRP
  name = G4_LUNG_ICRP
  specific = 4
FEATURE [App::DocumentObjectGroupPython] H_element052  label="H_element : 0.116"  # scripted group (container) (typed FeaturePython)
  n = 0.114318
FEATURE [App::DocumentObjectGroupPython] C_element057  label="C_element : 0.656"  # scripted group (container) (typed FeaturePython)
  n = 0.655824
FEATURE [App::DocumentObjectGroupPython] O_element058  label="O_element : 0.092"  # scripted group (container) (typed FeaturePython)
  n = 0.0921831
FEATURE [App::DocumentObjectGroupPython] Mg_element004  label="Mg_element : 0.135"  # scripted group (container) (typed FeaturePython)
  n = 0.134792
FEATURE [App::DocumentObjectGroupPython] Ca_element013  label="Ca_element : 0.003"  # scripted group (container) (typed FeaturePython)
  n = 0.002883
FEATURE [App::DocumentObjectGroupPython] G4_M3_WAX  # scripted group (container) (typed FeaturePython)
  Dunit = g/cm3
  Dvalue = 1.05
  Group = -> [H_element052,C_element057,O_element058,Mg_element004,Ca_element013]
  conduct = 2
  density = 1
  expand = 3
  formula = G4_M3_WAX
  name = G4_M3_WAX
  specific = 4
FEATURE [App::DocumentObjectGroupPython] Mg_element005  label="Mg_element : 1"  # scripted group (container) (typed FeaturePython)
  n = 1
  ref = Mg_element
FEATURE [App::DocumentObjectGroupPython] C_element058  label="C_element : 031"  # scripted group (container) (typed FeaturePython)
  n = 1
  ref = C_element
FEATURE [App::DocumentObjectGroupPython] O_element059  label="O_element : 030"  # scripted group (container) (typed FeaturePython)
  n = 3
  ref = O_element
FEATURE [App::DocumentObjectGroupPython] G4_MAGNESIUM_CARBONATE  # scripted group (container) (typed FeaturePython)
  Dunit = g/cm3
  Dvalue = 2.958
  Group = -> [Mg_element005,C_element058,O_element059]
  conduct = 2
  density = 1
  expand = 3
  formula = G4_MAGNESIUM_CARBONATE
  name = G4_MAGNESIUM_CARBONATE
  specific = 4
FEATURE [App::DocumentObjectGroupPython] Mg_element006  label="Mg_element : 002"  # scripted group (container) (typed FeaturePython)
  n = 1
  ref = Mg_element
FEATURE [App::DocumentObjectGroupPython] F_element013  label="F_element : 005"  # scripted group (container) (typed FeaturePython)
  n = 2
  ref = F_element
FEATURE [App::DocumentObjectGroupPython] G4_MAGNESIUM_FLUORIDE  # scripted group (container) (typed FeaturePython)
  Dunit = g/cm3
  Dvalue = 3
  Group = -> [Mg_element006,F_element013]
  conduct = 2
  density = 1
  expand = 3
  formula = G4_MAGNESIUM_FLUORIDE
  name = G4_MAGNESIUM_FLUORIDE
  specific = 4
FEATURE [App::DocumentObjectGroupPython] Mg_element007  label="Mg_element : 003"  # scripted group (container) (typed FeaturePython)
  n = 1
  ref = Mg_element
FEATURE [App::DocumentObjectGroupPython] O_element060  label="O_element : 031"  # scripted group (container) (typed FeaturePython)
  n = 1
  ref = O_element
FEATURE [App::DocumentObjectGroupPython] G4_MAGNESIUM_OXIDE  # scripted group (container) (typed FeaturePython)
  Dunit = g/cm3
  Dvalue = 3.58
  Group = -> [Mg_element007,O_element060]
  conduct = 2
  density = 1
  expand = 3
  formula = G4_MAGNESIUM_OXIDE
  name = G4_MAGNESIUM_OXIDE
  specific = 4
FEATURE [App::DocumentObjectGroupPython] Mg_element008  label="Mg_element : 004"  # scripted group (container) (typed FeaturePython)
  n = 1
  ref = Mg_element
FEATURE [App::DocumentObjectGroupPython] B_element006  label="B_element : 006"  # scripted group (container) (typed FeaturePython)
  n = 4
  ref = B_element
FEATURE [App::DocumentObjectGroupPython] O_element061  label="O_element : 032"  # scripted group (container) (typed FeaturePython)
  n = 7
  ref = O_element
FEATURE [App::DocumentObjectGroupPython] G4_MAGNESIUM_TETRABORATE  # scripted group (container) (typed FeaturePython)
  Dunit = g/cm3
  Dvalue = 2.53
  Group = -> [Mg_element008,B_element006,O_element061]
  conduct = 2
  density = 1
  expand = 3
  formula = G4_MAGNESIUM_TETRABORATE
  name = G4_MAGNESIUM_TETRABORATE
  specific = 4
FEATURE [App::DocumentObjectGroupPython] Hg_element001  label="Hg_element : 1"  # scripted group (container) (typed FeaturePython)
  n = 1
  ref = Hg_element
FEATURE [App::DocumentObjectGroupPython] I_element004  label="I_element : 2"  # scripted group (container) (typed FeaturePython)
  n = 2
  ref = I_element
FEATURE [App::DocumentObjectGroupPython] G4_MERCURIC_IODIDE  # scripted group (container) (typed FeaturePython)
  Dunit = g/cm3
  Dvalue = 6.36
  Group = -> [Hg_element001,I_element004]
  conduct = 2
  density = 1
  expand = 3
  formula = G4_MERCURIC_IODIDE
  name = G4_MERCURIC_IODIDE
  specific = 4
FEATURE [App::DocumentObjectGroupPython] C_element059  label="C_element : 032"  # scripted group (container) (typed FeaturePython)
  n = 1
  ref = C_element
FEATURE [App::DocumentObjectGroupPython] H_element053  label="H_element : 028"  # scripted group (container) (typed FeaturePython)
  n = 4
  ref = H_element
FEATURE [App::DocumentObjectGroupPython] G4_METHANE  # scripted group (container) (typed FeaturePython)
  Dunit = g/cm3
  Dvalue = 0.000667151
  Group = -> [C_element059,H_element053]
  conduct = 2
  density = 1
  expand = 3
  formula = G4_METHANE
  name = G4_METHANE
  specific = 4
FEATURE [App::DocumentObjectGroupPython] C_element060  label="C_element : 033"  # scripted group (container) (typed FeaturePython)
  n = 1
  ref = C_element
FEATURE [App::DocumentObjectGroupPython] H_element054  label="H_element : 029"  # scripted group (container) (typed FeaturePython)
  n = 4
  ref = H_element
FEATURE [App::DocumentObjectGroupPython] O_element062  label="O_element : 033"  # scripted group (container) (typed FeaturePython)
  n = 1
  ref = O_element
FEATURE [App::DocumentObjectGroupPython] G4_METHANOL  # scripted group (container) (typed FeaturePython)
  Dunit = g/cm3
  Dvalue = 0.7914
  Group = -> [C_element060,H_element054,O_element062]
  conduct = 2
  density = 1
  expand = 3
  formula = G4_METHANOL
  name = G4_METHANOL
  specific = 4
FEATURE [App::DocumentObjectGroupPython] H_element055  label="H_element : 0.134"  # scripted group (container) (typed FeaturePython)
  n = 0.13404
FEATURE [App::DocumentObjectGroupPython] C_element061  label="C_element : 0.778"  # scripted group (container) (typed FeaturePython)
  n = 0.77796
FEATURE [App::DocumentObjectGroupPython] O_element063  label="O_element : 0.035"  # scripted group (container) (typed FeaturePython)
  n = 0.03502
FEATURE [App::DocumentObjectGroupPython] Mg_element009  label="Mg_element : 0.039"  # scripted group (container) (typed FeaturePython)
  n = 0.038594
FEATURE [App::DocumentObjectGroupPython] Ti_element002  label="Ti_element : 0.014"  # scripted group (container) (typed FeaturePython)
  n = 0.014386
FEATURE [App::DocumentObjectGroupPython] G4_MIX_D_WAX  # scripted group (container) (typed FeaturePython)
  Dunit = g/cm3
  Dvalue = 0.99
  Group = -> [H_element055,C_element061,O_element063,Mg_element009,Ti_element002]
  conduct = 2
  density = 1
  expand = 3
  formula = G4_MIX_D_WAX
  name = G4_MIX_D_WAX
  specific = 4
FEATURE [App::DocumentObjectGroupPython] H_element056  label="H_element : 0.135"  # scripted group (container) (typed FeaturePython)
  n = 0.081192
FEATURE [App::DocumentObjectGroupPython] C_element062  label="C_element : 0.583"  # scripted group (container) (typed FeaturePython)
  n = 0.583442
FEATURE [App::DocumentObjectGroupPython] N_element024  label="N_element : 0.018"  # scripted group (container) (typed FeaturePython)
  n = 0.017798
FEATURE [App::DocumentObjectGroupPython] O_element064  label="O_element : 0.186"  # scripted group (container) (typed FeaturePython)
  n = 0.186381
FEATURE [App::DocumentObjectGroupPython] Mg_element010  label="Mg_element : 0.130"  # scripted group (container) (typed FeaturePython)
  n = 0.130287
FEATURE [App::DocumentObjectGroupPython] Cl_element015  label="Cl_element : 0.588"  # scripted group (container) (typed FeaturePython)
  n = 0.0009
FEATURE [App::DocumentObjectGroupPython] G4_MS20_TISSUE  # scripted group (container) (typed FeaturePython)
  Dunit = g/cm3
  Dvalue = 1
  Group = -> [H_element056,C_element062,N_element024,O_element064,Mg_element010,Cl_element015]
  conduct = 2
  density = 1
  expand = 3
  formula = G4_MS20_TISSUE
  name = G4_MS20_TISSUE
  specific = 4
FEATURE [App::DocumentObjectGroupPython] H_element057  label="H_element : 0.136"  # scripted group (container) (typed FeaturePython)
  n = 0.102
FEATURE [App::DocumentObjectGroupPython] C_element063  label="C_element : 0.143"  # scripted group (container) (typed FeaturePython)
  n = 0.143
FEATURE [App::DocumentObjectGroupPython] N_element025  label="N_element : 0.034"  # scripted group (container) (typed FeaturePython)
  n = 0.034
FEATURE [App::DocumentObjectGroupPython] O_element065  label="O_element : 0.710"  # scripted group (container) (typed FeaturePython)
  n = 0.71
FEATURE [App::DocumentObjectGroupPython] Na_element011  label="Na_element : 0.098"  # scripted group (container) (typed FeaturePython)
  n = 0.001
FEATURE [App::DocumentObjectGroupPython] P_element007  label="P_element : 0.002"  # scripted group (container) (typed FeaturePython)
  n = 0.002
FEATURE [App::DocumentObjectGroupPython] S_element017  label="S_element : 0.018"  # scripted group (container) (typed FeaturePython)
  n = 0.003
FEATURE [App::DocumentObjectGroupPython] Cl_element016  label="Cl_element : 0.589"  # scripted group (container) (typed FeaturePython)
  n = 0.001
FEATURE [App::DocumentObjectGroupPython] K_element006  label="K_element : 0.004"  # scripted group (container) (typed FeaturePython)
  n = 0.004
FEATURE [App::DocumentObjectGroupPython] G4_MUSCLE_SKELETAL_ICRP  # scripted group (container) (typed FeaturePython)
  Dunit = g/cm3
  Dvalue = 1.05
  Group = -> [H_element057,C_element063,N_element025,O_element065,Na_element011,P_element007,S_element017,Cl_element016,K_element006]
  conduct = 2
  density = 1
  expand = 3
  formula = G4_MUSCLE_SKELETAL_ICRP
  name = G4_MUSCLE_SKELETAL_ICRP
  specific = 4
FEATURE [App::DocumentObjectGroupPython] H_element058  label="H_element : 0.137"  # scripted group (container) (typed FeaturePython)
  n = 0.102102
FEATURE [App::DocumentObjectGroupPython] C_element064  label="C_element : 0.123"  # scripted group (container) (typed FeaturePython)
  n = 0.123123
FEATURE [App::DocumentObjectGroupPython] N_element026  label="N_element : 0.756"  # scripted group (container) (typed FeaturePython)
  n = 0.035035
FEATURE [App::DocumentObjectGroupPython] O_element066  label="O_element : 0.730"  # scripted group (container) (typed FeaturePython)
  n = 0.72973
FEATURE [App::DocumentObjectGroupPython] Na_element012  label="Na_element : 0.099"  # scripted group (container) (typed FeaturePython)
  n = 0.001001
FEATURE [App::DocumentObjectGroupPython] P_element008  label="P_element : 0.106"  # scripted group (container) (typed FeaturePython)
  n = 0.002002
FEATURE [App::DocumentObjectGroupPython] S_element018  label="S_element : 0.019"  # scripted group (container) (typed FeaturePython)
  n = 0.004004
FEATURE [App::DocumentObjectGroupPython] K_element007  label="K_element : 0.016"  # scripted group (container) (typed FeaturePython)
  n = 0.003003
FEATURE [App::DocumentObjectGroupPython] G4_MUSCLE_STRIATED_ICRU  # scripted group (container) (typed FeaturePython)
  Dunit = g/cm3
  Dvalue = 1.04
  Group = -> [H_element058,C_element064,N_element026,O_element066,Na_element012,P_element008,S_element018,K_element007]
  conduct = 2
  density = 1
  expand = 3
  formula = G4_MUSCLE_STRIATED_ICRU
  name = G4_MUSCLE_STRIATED_ICRU
  specific = 4
FEATURE [App::DocumentObjectGroupPython] H_element059  label="H_element : 0.098"  # scripted group (container) (typed FeaturePython)
  n = 0.0982341
FEATURE [App::DocumentObjectGroupPython] C_element065  label="C_element : 0.156"  # scripted group (container) (typed FeaturePython)
  n = 0.156214
FEATURE [App::DocumentObjectGroupPython] N_element027  label="N_element : 0.757"  # scripted group (container) (typed FeaturePython)
  n = 0.035451
FEATURE [App::DocumentObjectGroupPython] O_element067  label="O_element : 0.880"  # scripted group (container) (typed FeaturePython)
  n = 0.710101
FEATURE [App::DocumentObjectGroupPython] G4_MUSCLE_WITH_SUCROSE  # scripted group (container) (typed FeaturePython)
  Dunit = g/cm3
  Dvalue = 1.11
  Group = -> [H_element059,C_element065,N_element027,O_element067]
  conduct = 2
  density = 1
  expand = 3
  formula = G4_MUSCLE_WITH_SUCROSE
  name = G4_MUSCLE_WITH_SUCROSE
  specific = 4
FEATURE [App::DocumentObjectGroupPython] H_element060  label="H_element : 0.138"  # scripted group (container) (typed FeaturePython)
  n = 0.101969
FEATURE [App::DocumentObjectGroupPython] C_element066  label="C_element : 0.120"  # scripted group (container) (typed FeaturePython)
  n = 0.120058
FEATURE [App::DocumentObjectGroupPython] N_element028  label="N_element : 0.758"  # scripted group (container) (typed FeaturePython)
  n = 0.035451
FEATURE [App::DocumentObjectGroupPython] O_element068  label="O_element : 0.743"  # scripted group (container) (typed FeaturePython)
  n = 0.742522
FEATURE [App::DocumentObjectGroupPython] G4_MUSCLE_WITHOUT_SUCROSE  # scripted group (container) (typed FeaturePython)
  Dunit = g/cm3
  Dvalue = 1.07
  Group = -> [H_element060,C_element066,N_element028,O_element068]
  conduct = 2
  density = 1
  expand = 3
  formula = G4_MUSCLE_WITHOUT_SUCROSE
  name = G4_MUSCLE_WITHOUT_SUCROSE
  specific = 4
FEATURE [App::DocumentObjectGroupPython] C_element067  label="C_element : 10"  # scripted group (container) (typed FeaturePython)
  n = 10
  ref = C_element
FEATURE [App::DocumentObjectGroupPython] H_element061  label="H_element : 030"  # scripted group (container) (typed FeaturePython)
  n = 8
  ref = H_element
FEATURE [App::DocumentObjectGroupPython] G4_NAPHTHALENE  # scripted group (container) (typed FeaturePython)
  Dunit = g/cm3
  Dvalue = 1.145
  Group = -> [C_element067,H_element061]
  conduct = 2
  density = 1
  expand = 3
  formula = G4_NAPHTHALENE
  name = G4_NAPHTHALENE
  specific = 4
FEATURE [App::DocumentObjectGroupPython] C_element068  label="C_element : 034"  # scripted group (container) (typed FeaturePython)
  n = 6
  ref = C_element
FEATURE [App::DocumentObjectGroupPython] H_element062  label="H_element : 031"  # scripted group (container) (typed FeaturePython)
  n = 5
  ref = H_element
FEATURE [App::DocumentObjectGroupPython] N_element029  label="N_element : 012"  # scripted group (container) (typed FeaturePython)
  n = 1
  ref = N_element
FEATURE [App::DocumentObjectGroupPython] O_element069  label="O_element : 034"  # scripted group (container) (typed FeaturePython)
  n = 2
  ref = O_element
FEATURE [App::DocumentObjectGroupPython] G4_NITROBENZENE  # scripted group (container) (typed FeaturePython)
  Dunit = g/cm3
  Dvalue = 1.19867
  Group = -> [C_element068,H_element062,N_element029,O_element069]
  conduct = 2
  density = 1
  expand = 3
  formula = G4_NITROBENZENE
  name = G4_NITROBENZENE
  specific = 4
FEATURE [App::DocumentObjectGroupPython] N_element030  label="N_element : 013"  # scripted group (container) (typed FeaturePython)
  n = 2
  ref = N_element
FEATURE [App::DocumentObjectGroupPython] O_element070  label="O_element : 035"  # scripted group (container) (typed FeaturePython)
  n = 1
  ref = O_element
FEATURE [App::DocumentObjectGroupPython] G4_NITROUS_OXIDE  # scripted group (container) (typed FeaturePython)
  Dunit = g/cm3
  Dvalue = 0.00183094
  Group = -> [N_element030,O_element070]
  conduct = 2
  density = 1
  expand = 3
  formula = G4_NITROUS_OXIDE
  name = G4_NITROUS_OXIDE
  specific = 4
FEATURE [App::DocumentObjectGroupPython] H_element063  label="H_element : 0.104"  # scripted group (container) (typed FeaturePython)
  n = 0.103509
FEATURE [App::DocumentObjectGroupPython] C_element069  label="C_element : 0.648"  # scripted group (container) (typed FeaturePython)
  n = 0.648416
FEATURE [App::DocumentObjectGroupPython] N_element031  label="N_element : 0.100"  # scripted group (container) (typed FeaturePython)
  n = 0.0995361
FEATURE [App::DocumentObjectGroupPython] O_element071  label="O_element : 0.149"  # scripted group (container) (typed FeaturePython)
  n = 0.148539
FEATURE [App::DocumentObjectGroupPython] G4_NYLON_8062  label="G4_NYLON-8062"  # scripted group (container) (typed FeaturePython)
  Dunit = g/cm3
  Dvalue = 1.08
  Group = -> [H_element063,C_element069,N_element031,O_element071]
  conduct = 2
  density = 1
  expand = 3
  formula = G4_NYLON-8062
  name = G4_NYLON-8062
  specific = 4
FEATURE [App::DocumentObjectGroupPython] C_element070  label="C_element : 035"  # scripted group (container) (typed FeaturePython)
  n = 6
  ref = C_element
FEATURE [App::DocumentObjectGroupPython] H_element064  label="H_element : 11"  # scripted group (container) (typed FeaturePython)
  n = 11
  ref = H_element
FEATURE [App::DocumentObjectGroupPython] N_element032  label="N_element : 014"  # scripted group (container) (typed FeaturePython)
  n = 1
  ref = N_element
FEATURE [App::DocumentObjectGroupPython] O_element072  label="O_element : 036"  # scripted group (container) (typed FeaturePython)
  n = 1
  ref = O_element
FEATURE [App::DocumentObjectGroupPython] G4_NYLON_6_6  label="G4_NYLON-6-6"  # scripted group (container) (typed FeaturePython)
  Dunit = g/cm3
  Dvalue = 1.14
  Group = -> [C_element070,H_element064,N_element032,O_element072]
  conduct = 2
  density = 1
  expand = 3
  formula = G4_NYLON-6-6
  name = G4_NYLON-6-6
  specific = 4
FEATURE [App::DocumentObjectGroupPython] H_element065  label="H_element : 0.139"  # scripted group (container) (typed FeaturePython)
  n = 0.107062
FEATURE [App::DocumentObjectGroupPython] C_element071  label="C_element : 0.680"  # scripted group (container) (typed FeaturePython)
  n = 0.680449
FEATURE [App::DocumentObjectGroupPython] N_element033  label="N_element : 0.099"  # scripted group (container) (typed FeaturePython)
  n = 0.099189
FEATURE [App::DocumentObjectGroupPython] O_element073  label="O_element : 0.113"  # scripted group (container) (typed FeaturePython)
  n = 0.1133
FEATURE [App::DocumentObjectGroupPython] G4_NYLON_6_10  label="G4_NYLON-6-10"  # scripted group (container) (typed FeaturePython)
  Dunit = g/cm3
  Dvalue = 1.14
  Group = -> [H_element065,C_element071,N_element033,O_element073]
  conduct = 2
  density = 1
  expand = 3
  formula = G4_NYLON-6-10
  name = G4_NYLON-6-10
  specific = 4
FEATURE [App::DocumentObjectGroupPython] H_element066  label="H_element : 0.140"  # scripted group (container) (typed FeaturePython)
  n = 0.115476
FEATURE [App::DocumentObjectGroupPython] C_element072  label="C_element : 0.721"  # scripted group (container) (typed FeaturePython)
  n = 0.720818
FEATURE [App::DocumentObjectGroupPython] N_element034  label="N_element : 0.076"  # scripted group (container) (typed FeaturePython)
  n = 0.0764169
FEATURE [App::DocumentObjectGroupPython] O_element074  label="O_element : 0.087"  # scripted group (container) (typed FeaturePython)
  n = 0.0872889
FEATURE [App::DocumentObjectGroupPython] G4_NYLON_11_RILSAN  label="G4_NYLON-11_RILSAN"  # scripted group (container) (typed FeaturePython)
  Dunit = g/cm3
  Dvalue = 1.425
  Group = -> [H_element066,C_element072,N_element034,O_element074]
  conduct = 2
  density = 1
  expand = 3
  formula = G4_NYLON-11_RILSAN
  name = G4_NYLON-11_RILSAN
  specific = 4
FEATURE [App::DocumentObjectGroupPython] C_element073  label="C_element : 8"  # scripted group (container) (typed FeaturePython)
  n = 8
  ref = C_element
FEATURE [App::DocumentObjectGroupPython] H_element067  label="H_element : 18"  # scripted group (container) (typed FeaturePython)
  n = 18
  ref = H_element
FEATURE [App::DocumentObjectGroupPython] G4_OCTANE  # scripted group (container) (typed FeaturePython)
  Dunit = g/cm3
  Dvalue = 0.7026
  Group = -> [C_element073,H_element067]
  conduct = 2
  density = 1
  expand = 3
  formula = G4_OCTANE
  name = G4_OCTANE
  specific = 4
FEATURE [App::DocumentObjectGroupPython] C_element074  label="C_element : 25"  # scripted group (container) (typed FeaturePython)
  n = 25
  ref = C_element
FEATURE [App::DocumentObjectGroupPython] H_element068  label="H_element : 52"  # scripted group (container) (typed FeaturePython)
  n = 52
  ref = H_element
FEATURE [App::DocumentObjectGroupPython] G4_PARAFFIN  # scripted group (container) (typed FeaturePython)
  Dunit = g/cm3
  Dvalue = 0.93
  Group = -> [C_element074,H_element068]
  conduct = 2
  density = 1
  expand = 3
  formula = G4_PARAFFIN
  name = G4_PARAFFIN
  specific = 4
FEATURE [App::DocumentObjectGroupPython] C_element075  label="C_element : 036"  # scripted group (container) (typed FeaturePython)
  n = 5
  ref = C_element
FEATURE [App::DocumentObjectGroupPython] H_element069  label="H_element : 032"  # scripted group (container) (typed FeaturePython)
  n = 12
  ref = H_element
FEATURE [App::DocumentObjectGroupPython] G4_N_PENTANE  label="G4_N-PENTANE"  # scripted group (container) (typed FeaturePython)
  Dunit = g/cm3
  Dvalue = 0.6262
  Group = -> [C_element075,H_element069]
  conduct = 2
  density = 1
  expand = 3
  formula = G4_N-PENTANE
  name = G4_N-PENTANE
  specific = 4
FEATURE [App::DocumentObjectGroupPython] H_element070  label="H_element : 0.014"  # scripted group (container) (typed FeaturePython)
  n = 0.0141
FEATURE [App::DocumentObjectGroupPython] C_element076  label="C_element : 0.072"  # scripted group (container) (typed FeaturePython)
  n = 0.072261
FEATURE [App::DocumentObjectGroupPython] N_element035  label="N_element : 0.019"  # scripted group (container) (typed FeaturePython)
  n = 0.01932
FEATURE [App::DocumentObjectGroupPython] O_element075  label="O_element : 0.066"  # scripted group (container) (typed FeaturePython)
  n = 0.066101
FEATURE [App::DocumentObjectGroupPython] S_element019  label="S_element : 0.020"  # scripted group (container) (typed FeaturePython)
  n = 0.00189
FEATURE [App::DocumentObjectGroupPython] Br_element004  label="Br_element : 0.349"  # scripted group (container) (typed FeaturePython)
  n = 0.349103
FEATURE [App::DocumentObjectGroupPython] Ag_element001  label="Ag_element : 0.474"  # scripted group (container) (typed FeaturePython)
  n = 0.474105
FEATURE [App::DocumentObjectGroupPython] I_element005  label="I_element : 0.003"  # scripted group (container) (typed FeaturePython)
  n = 0.00312
FEATURE [App::DocumentObjectGroupPython] G4_PHOTO_EMULSION  # scripted group (container) (typed FeaturePython)
  Dunit = g/cm3
  Dvalue = 3.815
  Group = -> [H_element070,C_element076,N_element035,O_element075,S_element019,Br_element004,Ag_element001,I_element005]
  conduct = 2
  density = 1
  expand = 3
  formula = G4_PHOTO_EMULSION
  name = G4_PHOTO_EMULSION
  specific = 4
FEATURE [App::DocumentObjectGroupPython] C_element077  label="C_element : 9"  # scripted group (container) (typed FeaturePython)
  n = 9
  ref = C_element
FEATURE [App::DocumentObjectGroupPython] H_element071  label="H_element : 033"  # scripted group (container) (typed FeaturePython)
  n = 10
  ref = H_element
FEATURE [App::DocumentObjectGroupPython] G4_PLASTIC_SC_VINYLTOLUENE  # scripted group (container) (typed FeaturePython)
  Dunit = g/cm3
  Dvalue = 1.032
  Group = -> [C_element077,H_element071]
  conduct = 2
  density = 1
  expand = 3
  formula = G4_PLASTIC_SC_VINYLTOLUENE
  name = G4_PLASTIC_SC_VINYLTOLUENE
  specific = 4
FEATURE [App::DocumentObjectGroupPython] Pu_element001  label="Pu_element : 1"  # scripted group (container) (typed FeaturePython)
  n = 1
  ref = Pu_element
FEATURE [App::DocumentObjectGroupPython] O_element076  label="O_element : 037"  # scripted group (container) (typed FeaturePython)
  n = 2
  ref = O_element
FEATURE [App::DocumentObjectGroupPython] G4_PLUTONIUM_DIOXIDE  # scripted group (container) (typed FeaturePython)
  Dunit = g/cm3
  Dvalue = 11.46
  Group = -> [Pu_element001,O_element076]
  conduct = 2
  density = 1
  expand = 3
  formula = G4_PLUTONIUM_DIOXIDE
  name = G4_PLUTONIUM_DIOXIDE
  specific = 4
FEATURE [App::DocumentObjectGroupPython] C_element078  label="C_element : 037"  # scripted group (container) (typed FeaturePython)
  n = 3
  ref = C_element
FEATURE [App::DocumentObjectGroupPython] H_element072  label="H_element : 034"  # scripted group (container) (typed FeaturePython)
  n = 3
  ref = H_element
FEATURE [App::DocumentObjectGroupPython] N_element036  label="N_element : 015"  # scripted group (container) (typed FeaturePython)
  n = 1
  ref = N_element
FEATURE [App::DocumentObjectGroupPython] G4_POLYACRYLONITRILE  # scripted group (container) (typed FeaturePython)
  Dunit = g/cm3
  Dvalue = 1.17
  Group = -> [C_element078,H_element072,N_element036]
  conduct = 2
  density = 1
  expand = 3
  formula = G4_POLYACRYLONITRILE
  name = G4_POLYACRYLONITRILE
  specific = 4
FEATURE [App::DocumentObjectGroupPython] C_element079  label="C_element : 16"  # scripted group (container) (typed FeaturePython)
  n = 16
  ref = C_element
FEATURE [App::DocumentObjectGroupPython] H_element073  label="H_element : 035"  # scripted group (container) (typed FeaturePython)
  n = 14
  ref = H_element
FEATURE [App::DocumentObjectGroupPython] O_element077  label="O_element : 038"  # scripted group (container) (typed FeaturePython)
  n = 3
  ref = O_element
FEATURE [App::DocumentObjectGroupPython] G4_POLYCARBONATE  # scripted group (container) (typed FeaturePython)
  Dunit = g/cm3
  Dvalue = 1.2
  Group = -> [C_element079,H_element073,O_element077]
  conduct = 2
  density = 1
  expand = 3
  formula = G4_POLYCARBONATE
  name = G4_POLYCARBONATE
  specific = 4
FEATURE [App::DocumentObjectGroupPython] C_element080  label="C_element : 038"  # scripted group (container) (typed FeaturePython)
  n = 8
  ref = C_element
FEATURE [App::DocumentObjectGroupPython] H_element074  label="H_element : 036"  # scripted group (container) (typed FeaturePython)
  n = 7
  ref = H_element
FEATURE [App::DocumentObjectGroupPython] Cl_element017  label="Cl_element : 007"  # scripted group (container) (typed FeaturePython)
  n = 1
  ref = Cl_element
FEATURE [App::DocumentObjectGroupPython] G4_POLYCHLOROSTYRENE  # scripted group (container) (typed FeaturePython)
  Dunit = g/cm3
  Dvalue = 1.3
  Group = -> [C_element080,H_element074,Cl_element017]
  conduct = 2
  density = 1
  expand = 3
  formula = G4_POLYCHLOROSTYRENE
  name = G4_POLYCHLOROSTYRENE
  specific = 4
FEATURE [App::DocumentObjectGroupPython] C_element081  label="C_element : 039"  # scripted group (container) (typed FeaturePython)
  n = 1
  ref = C_element
FEATURE [App::DocumentObjectGroupPython] H_element075  label="H_element : 037"  # scripted group (container) (typed FeaturePython)
  n = 2
  ref = H_element
FEATURE [App::DocumentObjectGroupPython] G4_POLYETHYLENE  # scripted group (container) (typed FeaturePython)
  Dunit = g/cm3
  Dvalue = 0.94
  Group = -> [C_element081,H_element075]
  conduct = 2
  density = 1
  expand = 3
  formula = G4_POLYETHYLENE
  name = G4_POLYETHYLENE
  specific = 4
FEATURE [App::DocumentObjectGroupPython] C_element082  label="C_element : 040"  # scripted group (container) (typed FeaturePython)
  n = 10
  ref = C_element
FEATURE [App::DocumentObjectGroupPython] H_element076  label="H_element : 038"  # scripted group (container) (typed FeaturePython)
  n = 8
  ref = H_element
FEATURE [App::DocumentObjectGroupPython] O_element078  label="O_element : 039"  # scripted group (container) (typed FeaturePython)
  n = 4
  ref = O_element
FEATURE [App::DocumentObjectGroupPython] G4_MYLAR  # scripted group (container) (typed FeaturePython)
  Dunit = g/cm3
  Dvalue = 1.4
  Group = -> [C_element082,H_element076,O_element078]
  conduct = 2
  density = 1
  expand = 3
  formula = G4_MYLAR
  name = G4_MYLAR
  specific = 4
FEATURE [App::DocumentObjectGroupPython] C_element083  label="C_element : 041"  # scripted group (container) (typed FeaturePython)
  n = 5
  ref = C_element
FEATURE [App::DocumentObjectGroupPython] H_element077  label="H_element : 039"  # scripted group (container) (typed FeaturePython)
  n = 8
  ref = H_element
FEATURE [App::DocumentObjectGroupPython] O_element079  label="O_element : 040"  # scripted group (container) (typed FeaturePython)
  n = 2
  ref = O_element
FEATURE [App::DocumentObjectGroupPython] G4_PLEXIGLASS  # scripted group (container) (typed FeaturePython)
  Dunit = g/cm3
  Dvalue = 1.19
  Group = -> [C_element083,H_element077,O_element079]
  conduct = 2
  density = 1
  expand = 3
  formula = G4_PLEXIGLASS
  name = G4_PLEXIGLASS
  specific = 4
FEATURE [App::DocumentObjectGroupPython] C_element084  label="C_element : 042"  # scripted group (container) (typed FeaturePython)
  n = 1
  ref = C_element
FEATURE [App::DocumentObjectGroupPython] H_element078  label="H_element : 040"  # scripted group (container) (typed FeaturePython)
  n = 2
  ref = H_element
FEATURE [App::DocumentObjectGroupPython] O_element080  label="O_element : 041"  # scripted group (container) (typed FeaturePython)
  n = 1
  ref = O_element
FEATURE [App::DocumentObjectGroupPython] G4_POLYOXYMETHYLENE  # scripted group (container) (typed FeaturePython)
  Dunit = g/cm3
  Dvalue = 1.425
  Group = -> [C_element084,H_element078,O_element080]
  conduct = 2
  density = 1
  expand = 3
  formula = G4_POLYOXYMETHYLENE
  name = G4_POLYOXYMETHYLENE
  specific = 4
FEATURE [App::DocumentObjectGroupPython] C_element085  label="C_element : 043"  # scripted group (container) (typed FeaturePython)
  n = 2
  ref = C_element
FEATURE [App::DocumentObjectGroupPython] H_element079  label="H_element : 041"  # scripted group (container) (typed FeaturePython)
  n = 4
  ref = H_element
FEATURE [App::DocumentObjectGroupPython] G4_POLYPROPYLENE  # scripted group (container) (typed FeaturePython)
  Dunit = g/cm3
  Dvalue = 0.9
  Group = -> [C_element085,H_element079]
  conduct = 2
  density = 1
  expand = 3
  formula = G4_POLYPROPYLENE
  name = G4_POLYPROPYLENE
  specific = 4
FEATURE [App::DocumentObjectGroupPython] C_element086  label="C_element : 044"  # scripted group (container) (typed FeaturePython)
  n = 8
  ref = C_element
FEATURE [App::DocumentObjectGroupPython] H_element080  label="H_element : 042"  # scripted group (container) (typed FeaturePython)
  n = 8
  ref = H_element
FEATURE [App::DocumentObjectGroupPython] G4_POLYSTYRENE  # scripted group (container) (typed FeaturePython)
  Dunit = g/cm3
  Dvalue = 1.06
  Group = -> [C_element086,H_element080]
  conduct = 2
  density = 1
  expand = 3
  formula = G4_POLYSTYRENE
  name = G4_POLYSTYRENE
  specific = 4
FEATURE [App::DocumentObjectGroupPython] C_element087  label="C_element : 045"  # scripted group (container) (typed FeaturePython)
  n = 2
  ref = C_element
FEATURE [App::DocumentObjectGroupPython] F_element014  label="F_element : 4"  # scripted group (container) (typed FeaturePython)
  n = 4
  ref = F_element
FEATURE [App::DocumentObjectGroupPython] G4_TEFLON  # scripted group (container) (typed FeaturePython)
  Dunit = g/cm3
  Dvalue = 2.2
  Group = -> [C_element087,F_element014]
  conduct = 2
  density = 1
  expand = 3
  formula = G4_TEFLON
  name = G4_TEFLON
  specific = 4
FEATURE [App::DocumentObjectGroupPython] C_element088  label="C_element : 046"  # scripted group (container) (typed FeaturePython)
  n = 2
  ref = C_element
FEATURE [App::DocumentObjectGroupPython] F_element015  label="F_element : 006"  # scripted group (container) (typed FeaturePython)
  n = 3
  ref = F_element
FEATURE [App::DocumentObjectGroupPython] Cl_element018  label="Cl_element : 008"  # scripted group (container) (typed FeaturePython)
  n = 1
  ref = Cl_element
FEATURE [App::DocumentObjectGroupPython] G4_POLYTRIFLUOROCHLOROETHYLENE  # scripted group (container) (typed FeaturePython)
  Dunit = g/cm3
  Dvalue = 2.1
  Group = -> [C_element088,F_element015,Cl_element018]
  conduct = 2
  density = 1
  expand = 3
  formula = G4_POLYTRIFLUOROCHLOROETHYLENE
  name = G4_POLYTRIFLUOROCHLOROETHYLENE
  specific = 4
FEATURE [App::DocumentObjectGroupPython] C_element089  label="C_element : 047"  # scripted group (container) (typed FeaturePython)
  n = 4
  ref = C_element
FEATURE [App::DocumentObjectGroupPython] H_element081  label="H_element : 043"  # scripted group (container) (typed FeaturePython)
  n = 6
  ref = H_element
FEATURE [App::DocumentObjectGroupPython] O_element081  label="O_element : 042"  # scripted group (container) (typed FeaturePython)
  n = 2
  ref = O_element
FEATURE [App::DocumentObjectGroupPython] G4_POLYVINYL_ACETATE  # scripted group (container) (typed FeaturePython)
  Dunit = g/cm3
  Dvalue = 1.19
  Group = -> [C_element089,H_element081,O_element081]
  conduct = 2
  density = 1
  expand = 3
  formula = G4_POLYVINYL_ACETATE
  name = G4_POLYVINYL_ACETATE
  specific = 4
FEATURE [App::DocumentObjectGroupPython] C_element090  label="C_element : 048"  # scripted group (container) (typed FeaturePython)
  n = 2
  ref = C_element
FEATURE [App::DocumentObjectGroupPython] H_element082  label="H_element : 044"  # scripted group (container) (typed FeaturePython)
  n = 4
  ref = H_element
FEATURE [App::DocumentObjectGroupPython] O_element082  label="O_element : 043"  # scripted group (container) (typed FeaturePython)
  n = 1
  ref = O_element
FEATURE [App::DocumentObjectGroupPython] G4_POLYVINYL_ALCOHOL  # scripted group (container) (typed FeaturePython)
  Dunit = g/cm3
  Dvalue = 1.3
  Group = -> [C_element090,H_element082,O_element082]
  conduct = 2
  density = 1
  expand = 3
  formula = G4_POLYVINYL_ALCOHOL
  name = G4_POLYVINYL_ALCOHOL
  specific = 4
FEATURE [App::DocumentObjectGroupPython] C_element091  label="C_element : 049"  # scripted group (container) (typed FeaturePython)
  n = 8
  ref = C_element
FEATURE [App::DocumentObjectGroupPython] H_element083  label="H_element : 045"  # scripted group (container) (typed FeaturePython)
  n = 14
  ref = H_element
FEATURE [App::DocumentObjectGroupPython] O_element083  label="O_element : 044"  # scripted group (container) (typed FeaturePython)
  n = 2
  ref = O_element
FEATURE [App::DocumentObjectGroupPython] G4_POLYVINYL_BUTYRAL  # scripted group (container) (typed FeaturePython)
  Dunit = g/cm3
  Dvalue = 1.12
  Group = -> [C_element091,H_element083,O_element083]
  conduct = 2
  density = 1
  expand = 3
  formula = G4_POLYVINYL_BUTYRAL
  name = G4_POLYVINYL_BUTYRAL
  specific = 4
FEATURE [App::DocumentObjectGroupPython] C_element092  label="C_element : 050"  # scripted group (container) (typed FeaturePython)
  n = 2
  ref = C_element
FEATURE [App::DocumentObjectGroupPython] H_element084  label="H_element : 046"  # scripted group (container) (typed FeaturePython)
  n = 3
  ref = H_element
FEATURE [App::DocumentObjectGroupPython] Cl_element019  label="Cl_element : 009"  # scripted group (container) (typed FeaturePython)
  n = 1
  ref = Cl_element
FEATURE [App::DocumentObjectGroupPython] G4_POLYVINYL_CHLORIDE  # scripted group (container) (typed FeaturePython)
  Dunit = g/cm3
  Dvalue = 1.3
  Group = -> [C_element092,H_element084,Cl_element019]
  conduct = 2
  density = 1
  expand = 3
  formula = G4_POLYVINYL_CHLORIDE
  name = G4_POLYVINYL_CHLORIDE
  specific = 4
FEATURE [App::DocumentObjectGroupPython] C_element093  label="C_element : 051"  # scripted group (container) (typed FeaturePython)
  n = 2
  ref = C_element
FEATURE [App::DocumentObjectGroupPython] H_element085  label="H_element : 047"  # scripted group (container) (typed FeaturePython)
  n = 2
  ref = H_element
FEATURE [App::DocumentObjectGroupPython] Cl_element020  label="Cl_element : 010"  # scripted group (container) (typed FeaturePython)
  n = 2
  ref = Cl_element
FEATURE [App::DocumentObjectGroupPython] G4_POLYVINYLIDENE_CHLORIDE  # scripted group (container) (typed FeaturePython)
  Dunit = g/cm3
  Dvalue = 1.7
  Group = -> [C_element093,H_element085,Cl_element020]
  conduct = 2
  density = 1
  expand = 3
  formula = G4_POLYVINYLIDENE_CHLORIDE
  name = G4_POLYVINYLIDENE_CHLORIDE
  specific = 4
FEATURE [App::DocumentObjectGroupPython] C_element094  label="C_element : 052"  # scripted group (container) (typed FeaturePython)
  n = 2
  ref = C_element
FEATURE [App::DocumentObjectGroupPython] H_element086  label="H_element : 048"  # scripted group (container) (typed FeaturePython)
  n = 2
  ref = H_element
FEATURE [App::DocumentObjectGroupPython] F_element016  label="F_element : 007"  # scripted group (container) (typed FeaturePython)
  n = 2
  ref = F_element
FEATURE [App::DocumentObjectGroupPython] G4_POLYVINYLIDENE_FLUORIDE  # scripted group (container) (typed FeaturePython)
  Dunit = g/cm3
  Dvalue = 1.76
  Group = -> [C_element094,H_element086,F_element016]
  conduct = 2
  density = 1
  expand = 3
  formula = G4_POLYVINYLIDENE_FLUORIDE
  name = G4_POLYVINYLIDENE_FLUORIDE
  specific = 4
FEATURE [App::DocumentObjectGroupPython] C_element095  label="C_element : 053"  # scripted group (container) (typed FeaturePython)
  n = 6
  ref = C_element
FEATURE [App::DocumentObjectGroupPython] H_element087  label="H_element : 9"  # scripted group (container) (typed FeaturePython)
  n = 9
  ref = H_element
FEATURE [App::DocumentObjectGroupPython] N_element037  label="N_element : 016"  # scripted group (container) (typed FeaturePython)
  n = 1
  ref = N_element
FEATURE [App::DocumentObjectGroupPython] O_element084  label="O_element : 045"  # scripted group (container) (typed FeaturePython)
  n = 1
  ref = O_element
FEATURE [App::DocumentObjectGroupPython] G4_POLYVINYL_PYRROLIDONE  # scripted group (container) (typed FeaturePython)
  Dunit = g/cm3
  Dvalue = 1.25
  Group = -> [C_element095,H_element087,N_element037,O_element084]
  conduct = 2
  density = 1
  expand = 3
  formula = G4_POLYVINYL_PYRROLIDONE
  name = G4_POLYVINYL_PYRROLIDONE
  specific = 4
FEATURE [App::DocumentObjectGroupPython] K_element008  label="K_element : 1"  # scripted group (container) (typed FeaturePython)
  n = 1
  ref = K_element
FEATURE [App::DocumentObjectGroupPython] I_element006  label="I_element : 003"  # scripted group (container) (typed FeaturePython)
  n = 1
  ref = I_element
FEATURE [App::DocumentObjectGroupPython] G4_POTASSIUM_IODIDE  # scripted group (container) (typed FeaturePython)
  Dunit = g/cm3
  Dvalue = 3.13
  Group = -> [K_element008,I_element006]
  conduct = 2
  density = 1
  expand = 3
  formula = G4_POTASSIUM_IODIDE
  name = G4_POTASSIUM_IODIDE
  specific = 4
FEATURE [App::DocumentObjectGroupPython] K_element009  label="K_element : 2"  # scripted group (container) (typed FeaturePython)
  n = 2
  ref = K_element
FEATURE [App::DocumentObjectGroupPython] O_element085  label="O_element : 046"  # scripted group (container) (typed FeaturePython)
  n = 1
  ref = O_element
FEATURE [App::DocumentObjectGroupPython] G4_POTASSIUM_OXIDE  # scripted group (container) (typed FeaturePython)
  Dunit = g/cm3
  Dvalue = 2.32
  Group = -> [K_element009,O_element085]
  conduct = 2
  density = 1
  expand = 3
  formula = G4_POTASSIUM_OXIDE
  name = G4_POTASSIUM_OXIDE
  specific = 4
FEATURE [App::DocumentObjectGroupPython] C_element096  label="C_element : 054"  # scripted group (container) (typed FeaturePython)
  n = 3
  ref = C_element
FEATURE [App::DocumentObjectGroupPython] H_element088  label="H_element : 049"  # scripted group (container) (typed FeaturePython)
  n = 8
  ref = H_element
FEATURE [App::DocumentObjectGroupPython] G4_PROPANE  # scripted group (container) (typed FeaturePython)
  Dunit = g/cm3
  Dvalue = 0.00187939
  Group = -> [C_element096,H_element088]
  conduct = 2
  density = 1
  expand = 3
  formula = G4_PROPANE
  name = G4_PROPANE
  specific = 4
FEATURE [App::DocumentObjectGroupPython] C_element097  label="C_element : 055"  # scripted group (container) (typed FeaturePython)
  n = 3
  ref = C_element
FEATURE [App::DocumentObjectGroupPython] H_element089  label="H_element : 050"  # scripted group (container) (typed FeaturePython)
  n = 8
  ref = H_element
FEATURE [App::DocumentObjectGroupPython] G4_lPROPANE  # scripted group (container) (typed FeaturePython)
  Dunit = g/cm3
  Dvalue = 0.43
  Group = -> [C_element097,H_element089]
  conduct = 2
  density = 1
  expand = 3
  formula = G4_lPROPANE
  name = G4_lPROPANE
  specific = 4
FEATURE [App::DocumentObjectGroupPython] C_element098  label="C_element : 056"  # scripted group (container) (typed FeaturePython)
  n = 3
  ref = C_element
FEATURE [App::DocumentObjectGroupPython] H_element090  label="H_element : 051"  # scripted group (container) (typed FeaturePython)
  n = 8
  ref = H_element
FEATURE [App::DocumentObjectGroupPython] O_element086  label="O_element : 047"  # scripted group (container) (typed FeaturePython)
  n = 1
  ref = O_element
FEATURE [App::DocumentObjectGroupPython] G4_N_PROPYL_ALCOHOL  label="G4_N-PROPYL_ALCOHOL"  # scripted group (container) (typed FeaturePython)
  Dunit = g/cm3
  Dvalue = 0.8035
  Group = -> [C_element098,H_element090,O_element086]
  conduct = 2
  density = 1
  expand = 3
  formula = G4_N-PROPYL_ALCOHOL
  name = G4_N-PROPYL_ALCOHOL
  specific = 4
FEATURE [App::DocumentObjectGroupPython] C_element099  label="C_element : 057"  # scripted group (container) (typed FeaturePython)
  n = 5
  ref = C_element
FEATURE [App::DocumentObjectGroupPython] H_element091  label="H_element : 052"  # scripted group (container) (typed FeaturePython)
  n = 5
  ref = H_element
FEATURE [App::DocumentObjectGroupPython] N_element038  label="N_element : 017"  # scripted group (container) (typed FeaturePython)
  n = 1
  ref = N_element
FEATURE [App::DocumentObjectGroupPython] G4_PYRIDINE  # scripted group (container) (typed FeaturePython)
  Dunit = g/cm3
  Dvalue = 0.9819
  Group = -> [C_element099,H_element091,N_element038]
  conduct = 2
  density = 1
  expand = 3
  formula = G4_PYRIDINE
  name = G4_PYRIDINE
  specific = 4
FEATURE [App::DocumentObjectGroupPython] H_element092  label="H_element : 0.144"  # scripted group (container) (typed FeaturePython)
  n = 0.143711
FEATURE [App::DocumentObjectGroupPython] C_element100  label="C_element : 0.856"  # scripted group (container) (typed FeaturePython)
  n = 0.856289
FEATURE [App::DocumentObjectGroupPython] G4_RUBBER_BUTYL  # scripted group (container) (typed FeaturePython)
  Dunit = g/cm3
  Dvalue = 0.92
  Group = -> [H_element092,C_element100]
  conduct = 2
  density = 1
  expand = 3
  formula = G4_RUBBER_BUTYL
  name = G4_RUBBER_BUTYL
  specific = 4
FEATURE [App::DocumentObjectGroupPython] H_element093  label="H_element : 0.118"  # scripted group (container) (typed FeaturePython)
  n = 0.118371
FEATURE [App::DocumentObjectGroupPython] C_element101  label="C_element : 0.882"  # scripted group (container) (typed FeaturePython)
  n = 0.881629
FEATURE [App::DocumentObjectGroupPython] G4_RUBBER_NATURAL  # scripted group (container) (typed FeaturePython)
  Dunit = g/cm3
  Dvalue = 0.92
  Group = -> [H_element093,C_element101]
  conduct = 2
  density = 1
  expand = 3
  formula = G4_RUBBER_NATURAL
  name = G4_RUBBER_NATURAL
  specific = 4
FEATURE [App::DocumentObjectGroupPython] H_element094  label="H_element : 0.145"  # scripted group (container) (typed FeaturePython)
  n = 0.05692
FEATURE [App::DocumentObjectGroupPython] C_element102  label="C_element : 0.543"  # scripted group (container) (typed FeaturePython)
  n = 0.542646
FEATURE [App::DocumentObjectGroupPython] Cl_element021  label="Cl_element : 0.400"  # scripted group (container) (typed FeaturePython)
  n = 0.400434
FEATURE [App::DocumentObjectGroupPython] G4_RUBBER_NEOPRENE  # scripted group (container) (typed FeaturePython)
  Dunit = g/cm3
  Dvalue = 1.23
  Group = -> [H_element094,C_element102,Cl_element021]
  conduct = 2
  density = 1
  expand = 3
  formula = G4_RUBBER_NEOPRENE
  name = G4_RUBBER_NEOPRENE
  specific = 4
FEATURE [App::DocumentObjectGroupPython] Si_element006  label="Si_element : 1"  # scripted group (container) (typed FeaturePython)
  n = 1
  ref = Si_element
FEATURE [App::DocumentObjectGroupPython] O_element087  label="O_element : 048"  # scripted group (container) (typed FeaturePython)
  n = 2
  ref = O_element
FEATURE [App::DocumentObjectGroupPython] G4_SILICON_DIOXIDE  # scripted group (container) (typed FeaturePython)
  Dunit = g/cm3
  Dvalue = 2.32
  Group = -> [Si_element006,O_element087]
  conduct = 2
  density = 1
  expand = 3
  formula = G4_SILICON_DIOXIDE
  name = G4_SILICON_DIOXIDE
  specific = 4
FEATURE [App::DocumentObjectGroupPython] Ag_element002  label="Ag_element : 1"  # scripted group (container) (typed FeaturePython)
  n = 1
  ref = Ag_element
FEATURE [App::DocumentObjectGroupPython] Br_element005  label="Br_element : 003"  # scripted group (container) (typed FeaturePython)
  n = 1
  ref = Br_element
FEATURE [App::DocumentObjectGroupPython] G4_SILVER_BROMIDE  # scripted group (container) (typed FeaturePython)
  Dunit = g/cm3
  Dvalue = 6.473
  Group = -> [Ag_element002,Br_element005]
  conduct = 2
  density = 1
  expand = 3
  formula = G4_SILVER_BROMIDE
  name = G4_SILVER_BROMIDE
  specific = 4
FEATURE [App::DocumentObjectGroupPython] Ag_element003  label="Ag_element : 002"  # scripted group (container) (typed FeaturePython)
  n = 1
  ref = Ag_element
FEATURE [App::DocumentObjectGroupPython] Cl_element022  label="Cl_element : 011"  # scripted group (container) (typed FeaturePython)
  n = 1
  ref = Cl_element
FEATURE [App::DocumentObjectGroupPython] G4_SILVER_CHLORIDE  # scripted group (container) (typed FeaturePython)
  Dunit = g/cm3
  Dvalue = 5.56
  Group = -> [Ag_element003,Cl_element022]
  conduct = 2
  density = 1
  expand = 3
  formula = G4_SILVER_CHLORIDE
  name = G4_SILVER_CHLORIDE
  specific = 4
FEATURE [App::DocumentObjectGroupPython] Br_element006  label="Br_element : 0.423"  # scripted group (container) (typed FeaturePython)
  n = 0.422895
FEATURE [App::DocumentObjectGroupPython] Ag_element004  label="Ag_element : 0.574"  # scripted group (container) (typed FeaturePython)
  n = 0.573748
FEATURE [App::DocumentObjectGroupPython] I_element007  label="I_element : 0.649"  # scripted group (container) (typed FeaturePython)
  n = 0.003357
FEATURE [App::DocumentObjectGroupPython] G4_SILVER_HALIDES  # scripted group (container) (typed FeaturePython)
  Dunit = g/cm3
  Dvalue = 6.47
  Group = -> [Br_element006,Ag_element004,I_element007]
  conduct = 2
  density = 1
  expand = 3
  formula = G4_SILVER_HALIDES
  name = G4_SILVER_HALIDES
  specific = 4
FEATURE [App::DocumentObjectGroupPython] Ag_element005  label="Ag_element : 003"  # scripted group (container) (typed FeaturePython)
  n = 1
  ref = Ag_element
FEATURE [App::DocumentObjectGroupPython] I_element008  label="I_element : 004"  # scripted group (container) (typed FeaturePython)
  n = 1
  ref = I_element
FEATURE [App::DocumentObjectGroupPython] G4_SILVER_IODIDE  # scripted group (container) (typed FeaturePython)
  Dunit = g/cm3
  Dvalue = 6.01
  Group = -> [Ag_element005,I_element008]
  conduct = 2
  density = 1
  expand = 3
  formula = G4_SILVER_IODIDE
  name = G4_SILVER_IODIDE
  specific = 4
FEATURE [App::DocumentObjectGroupPython] H_element095  label="H_element : 0.100"  # scripted group (container) (typed FeaturePython)
  n = 0.1
FEATURE [App::DocumentObjectGroupPython] C_element103  label="C_element : 0.204"  # scripted group (container) (typed FeaturePython)
  n = 0.204
FEATURE [App::DocumentObjectGroupPython] N_element039  label="N_element : 0.759"  # scripted group (container) (typed FeaturePython)
  n = 0.042
FEATURE [App::DocumentObjectGroupPython] O_element088  label="O_element : 0.645"  # scripted group (container) (typed FeaturePython)
  n = 0.645
FEATURE [App::DocumentObjectGroupPython] Na_element013  label="Na_element : 0.100"  # scripted group (container) (typed FeaturePython)
  n = 0.002
FEATURE [App::DocumentObjectGroupPython] P_element009  label="P_element : 0.107"  # scripted group (container) (typed FeaturePython)
  n = 0.001
FEATURE [App::DocumentObjectGroupPython] S_element020  label="S_element : 0.021"  # scripted group (container) (typed FeaturePython)
  n = 0.002
FEATURE [App::DocumentObjectGroupPython] Cl_element023  label="Cl_element : 0.590"  # scripted group (container) (typed FeaturePython)
  n = 0.003
FEATURE [App::DocumentObjectGroupPython] K_element010  label="K_element : 0.001"  # scripted group (container) (typed FeaturePython)
  n = 0.001
FEATURE [App::DocumentObjectGroupPython] G4_SKIN_ICRP  # scripted group (container) (typed FeaturePython)
  Dunit = g/cm3
  Dvalue = 1.09
  Group = -> [H_element095,C_element103,N_element039,O_element088,Na_element013,P_element009,S_element020,Cl_element023,K_element010]
  conduct = 2
  density = 1
  expand = 3
  formula = G4_SKIN_ICRP
  name = G4_SKIN_ICRP
  specific = 4
FEATURE [App::DocumentObjectGroupPython] Na_element014  label="Na_element : 2"  # scripted group (container) (typed FeaturePython)
  n = 2
  ref = Na_element
FEATURE [App::DocumentObjectGroupPython] C_element104  label="C_element : 058"  # scripted group (container) (typed FeaturePython)
  n = 1
  ref = C_element
FEATURE [App::DocumentObjectGroupPython] O_element089  label="O_element : 049"  # scripted group (container) (typed FeaturePython)
  n = 3
  ref = O_element
FEATURE [App::DocumentObjectGroupPython] G4_SODIUM_CARBONATE  # scripted group (container) (typed FeaturePython)
  Dunit = g/cm3
  Dvalue = 2.532
  Group = -> [Na_element014,C_element104,O_element089]
  conduct = 2
  density = 1
  expand = 3
  formula = G4_SODIUM_CARBONATE
  name = G4_SODIUM_CARBONATE
  specific = 4
FEATURE [App::DocumentObjectGroupPython] Na_element015  label="Na_element : 1"  # scripted group (container) (typed FeaturePython)
  n = 1
  ref = Na_element
FEATURE [App::DocumentObjectGroupPython] I_element009  label="I_element : 005"  # scripted group (container) (typed FeaturePython)
  n = 1
  ref = I_element
FEATURE [App::DocumentObjectGroupPython] G4_SODIUM_IODIDE  # scripted group (container) (typed FeaturePython)
  Dunit = g/cm3
  Dvalue = 3.667
  Group = -> [Na_element015,I_element009]
  conduct = 2
  density = 1
  expand = 3
  formula = G4_SODIUM_IODIDE
  name = G4_SODIUM_IODIDE
  specific = 4
FEATURE [App::DocumentObjectGroupPython] Na_element016  label="Na_element : 003"  # scripted group (container) (typed FeaturePython)
  n = 2
  ref = Na_element
FEATURE [App::DocumentObjectGroupPython] O_element090  label="O_element : 050"  # scripted group (container) (typed FeaturePython)
  n = 1
  ref = O_element
FEATURE [App::DocumentObjectGroupPython] G4_SODIUM_MONOXIDE  # scripted group (container) (typed FeaturePython)
  Dunit = g/cm3
  Dvalue = 2.27
  Group = -> [Na_element016,O_element090]
  conduct = 2
  density = 1
  expand = 3
  formula = G4_SODIUM_MONOXIDE
  name = G4_SODIUM_MONOXIDE
  specific = 4
FEATURE [App::DocumentObjectGroupPython] Na_element017  label="Na_element : 004"  # scripted group (container) (typed FeaturePython)
  n = 1
  ref = Na_element
FEATURE [App::DocumentObjectGroupPython] N_element040  label="N_element : 018"  # scripted group (container) (typed FeaturePython)
  n = 1
  ref = N_element
FEATURE [App::DocumentObjectGroupPython] O_element091  label="O_element : 051"  # scripted group (container) (typed FeaturePython)
  n = 3
  ref = O_element
FEATURE [App::DocumentObjectGroupPython] G4_SODIUM_NITRATE  # scripted group (container) (typed FeaturePython)
  Dunit = g/cm3
  Dvalue = 2.261
  Group = -> [Na_element017,N_element040,O_element091]
  conduct = 2
  density = 1
  expand = 3
  formula = G4_SODIUM_NITRATE
  name = G4_SODIUM_NITRATE
  specific = 4
FEATURE [App::DocumentObjectGroupPython] C_element105  label="C_element : 059"  # scripted group (container) (typed FeaturePython)
  n = 14
  ref = C_element
FEATURE [App::DocumentObjectGroupPython] H_element096  label="H_element : 053"  # scripted group (container) (typed FeaturePython)
  n = 12
  ref = H_element
FEATURE [App::DocumentObjectGroupPython] G4_STILBENE  # scripted group (container) (typed FeaturePython)
  Dunit = g/cm3
  Dvalue = 0.9707
  Group = -> [C_element105,H_element096]
  conduct = 2
  density = 1
  expand = 3
  formula = G4_STILBENE
  name = G4_STILBENE
  specific = 4
FEATURE [App::DocumentObjectGroupPython] C_element106  label="C_element : 12"  # scripted group (container) (typed FeaturePython)
  n = 12
  ref = C_element
FEATURE [App::DocumentObjectGroupPython] H_element097  label="H_element : 22"  # scripted group (container) (typed FeaturePython)
  n = 22
  ref = H_element
FEATURE [App::DocumentObjectGroupPython] O_element092  label="O_element : 11"  # scripted group (container) (typed FeaturePython)
  n = 11
  ref = O_element
FEATURE [App::DocumentObjectGroupPython] G4_SUCROSE  # scripted group (container) (typed FeaturePython)
  Dunit = g/cm3
  Dvalue = 1.5805
  Group = -> [C_element106,H_element097,O_element092]
  conduct = 2
  density = 1
  expand = 3
  formula = G4_SUCROSE
  name = G4_SUCROSE
  specific = 4
FEATURE [App::DocumentObjectGroupPython] C_element107  label="C_element : 18"  # scripted group (container) (typed FeaturePython)
  n = 18
  ref = C_element
FEATURE [App::DocumentObjectGroupPython] H_element098  label="H_element : 054"  # scripted group (container) (typed FeaturePython)
  n = 14
  ref = H_element
FEATURE [App::DocumentObjectGroupPython] G4_TERPHENYL  # scripted group (container) (typed FeaturePython)
  Dunit = g/cm3
  Dvalue = 1.24
  Group = -> [C_element107,H_element098]
  conduct = 2
  density = 1
  expand = 3
  formula = G4_TERPHENYL
  name = G4_TERPHENYL
  specific = 4
FEATURE [App::DocumentObjectGroupPython] H_element099  label="H_element : 0.146"  # scripted group (container) (typed FeaturePython)
  n = 0.106
FEATURE [App::DocumentObjectGroupPython] C_element108  label="C_element : 0.883"  # scripted group (container) (typed FeaturePython)
  n = 0.099
FEATURE [App::DocumentObjectGroupPython] N_element041  label="N_element : 0.020"  # scripted group (container) (typed FeaturePython)
  n = 0.02
FEATURE [App::DocumentObjectGroupPython] O_element093  label="O_element : 0.766"  # scripted group (container) (typed FeaturePython)
  n = 0.766
FEATURE [App::DocumentObjectGroupPython] Na_element018  label="Na_element : 0.101"  # scripted group (container) (typed FeaturePython)
  n = 0.002
FEATURE [App::DocumentObjectGroupPython] P_element010  label="P_element : 0.108"  # scripted group (container) (typed FeaturePython)
  n = 0.001
FEATURE [App::DocumentObjectGroupPython] S_element021  label="S_element : 0.022"  # scripted group (container) (typed FeaturePython)
  n = 0.002
FEATURE [App::DocumentObjectGroupPython] Cl_element024  label="Cl_element : 0.002"  # scripted group (container) (typed FeaturePython)
  n = 0.002
FEATURE [App::DocumentObjectGroupPython] K_element011  label="K_element : 0.017"  # scripted group (container) (typed FeaturePython)
  n = 0.002
FEATURE [App::DocumentObjectGroupPython] G4_TESTIS_ICRP  # scripted group (container) (typed FeaturePython)
  Dunit = g/cm3
  Dvalue = 1.04
  Group = -> [H_element099,C_element108,N_element041,O_element093,Na_element018,P_element010,S_element021,Cl_element024,K_element011]
  conduct = 2
  density = 1
  expand = 3
  formula = G4_TESTIS_ICRP
  name = G4_TESTIS_ICRP
  specific = 4
FEATURE [App::DocumentObjectGroupPython] C_element109  label="C_element : 060"  # scripted group (container) (typed FeaturePython)
  n = 2
  ref = C_element
FEATURE [App::DocumentObjectGroupPython] Cl_element025  label="Cl_element : 012"  # scripted group (container) (typed FeaturePython)
  n = 4
  ref = Cl_element
FEATURE [App::DocumentObjectGroupPython] G4_TETRACHLOROETHYLENE  # scripted group (container) (typed FeaturePython)
  Dunit = g/cm3
  Dvalue = 1.625
  Group = -> [C_element109,Cl_element025]
  conduct = 2
  density = 1
  expand = 3
  formula = G4_TETRACHLOROETHYLENE
  name = G4_TETRACHLOROETHYLENE
  specific = 4
FEATURE [App::DocumentObjectGroupPython] Tl_element001  label="Tl_element : 1"  # scripted group (container) (typed FeaturePython)
  n = 1
  ref = Tl_element
FEATURE [App::DocumentObjectGroupPython] Cl_element026  label="Cl_element : 013"  # scripted group (container) (typed FeaturePython)
  n = 1
  ref = Cl_element
FEATURE [App::DocumentObjectGroupPython] G4_THALLIUM_CHLORIDE  # scripted group (container) (typed FeaturePython)
  Dunit = g/cm3
  Dvalue = 7.004
  Group = -> [Tl_element001,Cl_element026]
  conduct = 2
  density = 1
  expand = 3
  formula = G4_THALLIUM_CHLORIDE
  name = G4_THALLIUM_CHLORIDE
  specific = 4
FEATURE [App::DocumentObjectGroupPython] H_element100  label="H_element : 0.147"  # scripted group (container) (typed FeaturePython)
  n = 0.105
FEATURE [App::DocumentObjectGroupPython] C_element110  label="C_element : 0.256"  # scripted group (container) (typed FeaturePython)
  n = 0.256
FEATURE [App::DocumentObjectGroupPython] N_element042  label="N_element : 0.760"  # scripted group (container) (typed FeaturePython)
  n = 0.027
FEATURE [App::DocumentObjectGroupPython] O_element094  label="O_element : 0.602"  # scripted group (container) (typed FeaturePython)
  n = 0.602
FEATURE [App::DocumentObjectGroupPython] Na_element019  label="Na_element : 0.102"  # scripted group (container) (typed FeaturePython)
  n = 0.001
FEATURE [App::DocumentObjectGroupPython] P_element011  label="P_element : 0.109"  # scripted group (container) (typed FeaturePython)
  n = 0.002
FEATURE [App::DocumentObjectGroupPython] S_element022  label="S_element : 0.023"  # scripted group (container) (typed FeaturePython)
  n = 0.003
FEATURE [App::DocumentObjectGroupPython] Cl_element027  label="Cl_element : 0.591"  # scripted group (container) (typed FeaturePython)
  n = 0.002
FEATURE [App::DocumentObjectGroupPython] K_element012  label="K_element : 0.018"  # scripted group (container) (typed FeaturePython)
  n = 0.002
FEATURE [App::DocumentObjectGroupPython] G4_TISSUE_SOFT_ICRP  # scripted group (container) (typed FeaturePython)
  Dunit = g/cm3
  Dvalue = 1.03
  Group = -> [H_element100,C_element110,N_element042,O_element094,Na_element019,P_element011,S_element022,Cl_element027,K_element012]
  conduct = 2
  density = 1
  expand = 3
  formula = G4_TISSUE_SOFT_ICRP
  name = G4_TISSUE_SOFT_ICRP
  specific = 4
FEATURE [App::DocumentObjectGroupPython] H_element101  label="H_element : 0.148"  # scripted group (container) (typed FeaturePython)
  n = 0.101
FEATURE [App::DocumentObjectGroupPython] C_element111  label="C_element : 0.111"  # scripted group (container) (typed FeaturePython)
  n = 0.111
FEATURE [App::DocumentObjectGroupPython] N_element043  label="N_element : 0.026"  # scripted group (container) (typed FeaturePython)
  n = 0.026
FEATURE [App::DocumentObjectGroupPython] O_element095  label="O_element : 0.762"  # scripted group (container) (typed FeaturePython)
  n = 0.762
FEATURE [App::DocumentObjectGroupPython] G4_TISSUE_SOFT_ICRU_4  label="G4_TISSUE_SOFT_ICRU-4"  # scripted group (container) (typed FeaturePython)
  Dunit = g/cm3
  Dvalue = 1
  Group = -> [H_element101,C_element111,N_element043,O_element095]
  conduct = 2
  density = 1
  expand = 3
  formula = G4_TISSUE_SOFT_ICRU-4
  name = G4_TISSUE_SOFT_ICRU-4
  specific = 4
FEATURE [App::DocumentObjectGroupPython] H_element102  label="H_element : 0.149"  # scripted group (container) (typed FeaturePython)
  n = 0.101869
FEATURE [App::DocumentObjectGroupPython] C_element112  label="C_element : 0.456"  # scripted group (container) (typed FeaturePython)
  n = 0.456179
FEATURE [App::DocumentObjectGroupPython] N_element044  label="N_element : 0.761"  # scripted group (container) (typed FeaturePython)
  n = 0.035172
FEATURE [App::DocumentObjectGroupPython] O_element096  label="O_element : 0.407"  # scripted group (container) (typed FeaturePython)
  n = 0.40678
FEATURE [App::DocumentObjectGroupPython] G4_TISSUE_METHANE  label="G4_TISSUE-METHANE"  # scripted group (container) (typed FeaturePython)
  Dunit = g/cm3
  Dvalue = 0.00106409
  Group = -> [H_element102,C_element112,N_element044,O_element096]
  conduct = 2
  density = 1
  expand = 3
  formula = G4_TISSUE-METHANE
  name = G4_TISSUE-METHANE
  specific = 4
FEATURE [App::DocumentObjectGroupPython] H_element103  label="H_element : 0.103"  # scripted group (container) (typed FeaturePython)
  n = 0.102672
FEATURE [App::DocumentObjectGroupPython] C_element113  label="C_element : 0.569"  # scripted group (container) (typed FeaturePython)
  n = 0.56894
FEATURE [App::DocumentObjectGroupPython] N_element045  label="N_element : 0.762"  # scripted group (container) (typed FeaturePython)
  n = 0.035022
FEATURE [App::DocumentObjectGroupPython] O_element097  label="O_element : 0.293"  # scripted group (container) (typed FeaturePython)
  n = 0.293366
FEATURE [App::DocumentObjectGroupPython] G4_TISSUE_PROPANE  label="G4_TISSUE-PROPANE"  # scripted group (container) (typed FeaturePython)
  Dunit = g/cm3
  Dvalue = 0.00182628
  Group = -> [H_element103,C_element113,N_element045,O_element097]
  conduct = 2
  density = 1
  expand = 3
  formula = G4_TISSUE-PROPANE
  name = G4_TISSUE-PROPANE
  specific = 4
FEATURE [App::DocumentObjectGroupPython] Ti_element003  label="Ti_element : 1"  # scripted group (container) (typed FeaturePython)
  n = 1
  ref = Ti_element
FEATURE [App::DocumentObjectGroupPython] O_element098  label="O_element : 052"  # scripted group (container) (typed FeaturePython)
  n = 2
  ref = O_element
FEATURE [App::DocumentObjectGroupPython] G4_TITANIUM_DIOXIDE  # scripted group (container) (typed FeaturePython)
  Dunit = g/cm3
  Dvalue = 4.26
  Group = -> [Ti_element003,O_element098]
  conduct = 2
  density = 1
  expand = 3
  formula = G4_TITANIUM_DIOXIDE
  name = G4_TITANIUM_DIOXIDE
  specific = 4
FEATURE [App::DocumentObjectGroupPython] C_element114  label="C_element : 061"  # scripted group (container) (typed FeaturePython)
  n = 7
  ref = C_element
FEATURE [App::DocumentObjectGroupPython] H_element104  label="H_element : 055"  # scripted group (container) (typed FeaturePython)
  n = 8
  ref = H_element
FEATURE [App::DocumentObjectGroupPython] G4_TOLUENE  # scripted group (container) (typed FeaturePython)
  Dunit = g/cm3
  Dvalue = 0.8669
  Group = -> [C_element114,H_element104]
  conduct = 2
  density = 1
  expand = 3
  formula = G4_TOLUENE
  name = G4_TOLUENE
  specific = 4
FEATURE [App::DocumentObjectGroupPython] C_element115  label="C_element : 062"  # scripted group (container) (typed FeaturePython)
  n = 2
  ref = C_element
FEATURE [App::DocumentObjectGroupPython] H_element105  label="H_element : 056"  # scripted group (container) (typed FeaturePython)
  n = 1
  ref = H_element
FEATURE [App::DocumentObjectGroupPython] Cl_element028  label="Cl_element : 014"  # scripted group (container) (typed FeaturePython)
  n = 3
  ref = Cl_element
FEATURE [App::DocumentObjectGroupPython] G4_TRICHLOROETHYLENE  # scripted group (container) (typed FeaturePython)
  Dunit = g/cm3
  Dvalue = 1.46
  Group = -> [C_element115,H_element105,Cl_element028]
  conduct = 2
  density = 1
  expand = 3
  formula = G4_TRICHLOROETHYLENE
  name = G4_TRICHLOROETHYLENE
  specific = 4
FEATURE [App::DocumentObjectGroupPython] C_element116  label="C_element : 063"  # scripted group (container) (typed FeaturePython)
  n = 6
  ref = C_element
FEATURE [App::DocumentObjectGroupPython] H_element106  label="H_element : 15"  # scripted group (container) (typed FeaturePython)
  n = 15
  ref = H_element
FEATURE [App::DocumentObjectGroupPython] O_element099  label="O_element : 053"  # scripted group (container) (typed FeaturePython)
  n = 4
  ref = O_element
FEATURE [App::DocumentObjectGroupPython] P_element012  label="P_element : 1"  # scripted group (container) (typed FeaturePython)
  n = 1
  ref = P_element
FEATURE [App::DocumentObjectGroupPython] G4_TRIETHYL_PHOSPHATE  # scripted group (container) (typed FeaturePython)
  Dunit = g/cm3
  Dvalue = 1.07
  Group = -> [C_element116,H_element106,O_element099,P_element012]
  conduct = 2
  density = 1
  expand = 3
  formula = G4_TRIETHYL_PHOSPHATE
  name = G4_TRIETHYL_PHOSPHATE
  specific = 4
FEATURE [App::DocumentObjectGroupPython] W_element003  label="W_element : 003"  # scripted group (container) (typed FeaturePython)
  n = 1
  ref = W_element
FEATURE [App::DocumentObjectGroupPython] F_element017  label="F_element : 6"  # scripted group (container) (typed FeaturePython)
  n = 6
  ref = F_element
FEATURE [App::DocumentObjectGroupPython] G4_TUNGSTEN_HEXAFLUORIDE  # scripted group (container) (typed FeaturePython)
  Dunit = g/cm3
  Dvalue = 2.4
  Group = -> [W_element003,F_element017]
  conduct = 2
  density = 1
  expand = 3
  formula = G4_TUNGSTEN_HEXAFLUORIDE
  name = G4_TUNGSTEN_HEXAFLUORIDE
  specific = 4
FEATURE [App::DocumentObjectGroupPython] U_element001  label="U_element : 1"  # scripted group (container) (typed FeaturePython)
  n = 1
  ref = U_element
FEATURE [App::DocumentObjectGroupPython] C_element117  label="C_element : 064"  # scripted group (container) (typed FeaturePython)
  n = 2
  ref = C_element
FEATURE [App::DocumentObjectGroupPython] G4_URANIUM_DICARBIDE  # scripted group (container) (typed FeaturePython)
  Dunit = g/cm3
  Dvalue = 11.28
  Group = -> [U_element001,C_element117]
  conduct = 2
  density = 1
  expand = 3
  formula = G4_URANIUM_DICARBIDE
  name = G4_URANIUM_DICARBIDE
  specific = 4
FEATURE [App::DocumentObjectGroupPython] U_element002  label="U_element : 002"  # scripted group (container) (typed FeaturePython)
  n = 1
  ref = U_element
FEATURE [App::DocumentObjectGroupPython] C_element118  label="C_element : 065"  # scripted group (container) (typed FeaturePython)
  n = 1
  ref = C_element
FEATURE [App::DocumentObjectGroupPython] G4_URANIUM_MONOCARBIDE  # scripted group (container) (typed FeaturePython)
  Dunit = g/cm3
  Dvalue = 13.63
  Group = -> [U_element002,C_element118]
  conduct = 2
  density = 1
  expand = 3
  formula = G4_URANIUM_MONOCARBIDE
  name = G4_URANIUM_MONOCARBIDE
  specific = 4
FEATURE [App::DocumentObjectGroupPython] U_element003  label="U_element : 003"  # scripted group (container) (typed FeaturePython)
  n = 1
  ref = U_element
FEATURE [App::DocumentObjectGroupPython] O_element100  label="O_element : 054"  # scripted group (container) (typed FeaturePython)
  n = 2
  ref = O_element
FEATURE [App::DocumentObjectGroupPython] G4_URANIUM_OXIDE  # scripted group (container) (typed FeaturePython)
  Dunit = g/cm3
  Dvalue = 10.96
  Group = -> [U_element003,O_element100]
  conduct = 2
  density = 1
  expand = 3
  formula = G4_URANIUM_OXIDE
  name = G4_URANIUM_OXIDE
  specific = 4
FEATURE [App::DocumentObjectGroupPython] C_element119  label="C_element : 066"  # scripted group (container) (typed FeaturePython)
  n = 1
  ref = C_element
FEATURE [App::DocumentObjectGroupPython] H_element107  label="H_element : 057"  # scripted group (container) (typed FeaturePython)
  n = 4
  ref = H_element
FEATURE [App::DocumentObjectGroupPython] N_element046  label="N_element : 019"  # scripted group (container) (typed FeaturePython)
  n = 2
  ref = N_element
FEATURE [App::DocumentObjectGroupPython] O_element101  label="O_element : 055"  # scripted group (container) (typed FeaturePython)
  n = 1
  ref = O_element
FEATURE [App::DocumentObjectGroupPython] G4_UREA  # scripted group (container) (typed FeaturePython)
  Dunit = g/cm3
  Dvalue = 1.323
  Group = -> [C_element119,H_element107,N_element046,O_element101]
  conduct = 2
  density = 1
  expand = 3
  formula = G4_UREA
  name = G4_UREA
  specific = 4
FEATURE [App::DocumentObjectGroupPython] C_element120  label="C_element : 067"  # scripted group (container) (typed FeaturePython)
  n = 5
  ref = C_element
FEATURE [App::DocumentObjectGroupPython] H_element108  label="H_element : 058"  # scripted group (container) (typed FeaturePython)
  n = 11
  ref = H_element
FEATURE [App::DocumentObjectGroupPython] N_element047  label="N_element : 020"  # scripted group (container) (typed FeaturePython)
  n = 1
  ref = N_element
FEATURE [App::DocumentObjectGroupPython] O_element102  label="O_element : 056"  # scripted group (container) (typed FeaturePython)
  n = 2
  ref = O_element
FEATURE [App::DocumentObjectGroupPython] G4_VALINE  # scripted group (container) (typed FeaturePython)
  Dunit = g/cm3
  Dvalue = 1.23
  Group = -> [C_element120,H_element108,N_element047,O_element102]
  conduct = 2
  density = 1
  expand = 3
  formula = G4_VALINE
  name = G4_VALINE
  specific = 4
FEATURE [App::DocumentObjectGroupPython] H_element109  label="H_element : 0.009"  # scripted group (container) (typed FeaturePython)
  n = 0.009417
FEATURE [App::DocumentObjectGroupPython] C_element121  label="C_element : 0.281"  # scripted group (container) (typed FeaturePython)
  n = 0.280555
FEATURE [App::DocumentObjectGroupPython] F_element018  label="F_element : 0.710"  # scripted group (container) (typed FeaturePython)
  n = 0.710028
FEATURE [App::DocumentObjectGroupPython] G4_VITON  # scripted group (container) (typed FeaturePython)
  Dunit = g/cm3
  Dvalue = 1.8
  Group = -> [H_element109,C_element121,F_element018]
  conduct = 2
  density = 1
  expand = 3
  formula = G4_VITON
  name = G4_VITON
  specific = 4
FEATURE [App::DocumentObjectGroupPython] H_element110  label="H_element : 059"  # scripted group (container) (typed FeaturePython)
  n = 2
  ref = H_element
FEATURE [App::DocumentObjectGroupPython] O_element103  label="O_element : 057"  # scripted group (container) (typed FeaturePython)
  n = 1
  ref = O_element
FEATURE [App::DocumentObjectGroupPython] G4_WATER  # scripted group (container) (typed FeaturePython)
  Dunit = g/cm3
  Dvalue = 1
  Group = -> [H_element110,O_element103]
  conduct = 2
  density = 1
  expand = 3
  formula = G4_WATER
  name = G4_WATER
  specific = 4
FEATURE [App::DocumentObjectGroupPython] H_element111  label="H_element : 060"  # scripted group (container) (typed FeaturePython)
  n = 2
  ref = H_element
FEATURE [App::DocumentObjectGroupPython] O_element104  label="O_element : 058"  # scripted group (container) (typed FeaturePython)
  n = 1
  ref = O_element
FEATURE [App::DocumentObjectGroupPython] G4_WATER_VAPOR  # scripted group (container) (typed FeaturePython)
  Dunit = g/cm3
  Dvalue = 0.000756182
  Group = -> [H_element111,O_element104]
  conduct = 2
  density = 1
  expand = 3
  formula = G4_WATER_VAPOR
  name = G4_WATER_VAPOR
  specific = 4
FEATURE [App::DocumentObjectGroupPython] C_element122  label="C_element : 068"  # scripted group (container) (typed FeaturePython)
  n = 8
  ref = C_element
FEATURE [App::DocumentObjectGroupPython] H_element112  label="H_element : 061"  # scripted group (container) (typed FeaturePython)
  n = 10
  ref = H_element
FEATURE [App::DocumentObjectGroupPython] G4_XYLENE  # scripted group (container) (typed FeaturePython)
  Dunit = g/cm3
  Dvalue = 0.87
  Group = -> [C_element122,H_element112]
  conduct = 2
  density = 1
  expand = 3
  formula = G4_XYLENE
  name = G4_XYLENE
  specific = 4
FEATURE [App::DocumentObjectGroupPython] C_element123  label="C_element : 069"  # scripted group (container) (typed FeaturePython)
  n = 1
  ref = C_element
FEATURE [App::DocumentObjectGroupPython] G4_GRAPHITE  # scripted group (container) (typed FeaturePython)
  Dunit = g/cm3
  Dvalue = 2.21
  Group = -> [C_element123]
  conduct = 2
  density = 1
  expand = 3
  formula = G4_GRAPHITE
  name = G4_GRAPHITE
  specific = 4
FEATURE [App::DocumentObjectGroupPython] NIST  # scripted group (container) (typed FeaturePython)
  Group = -> [G4_A_150_TISSUE,G4_ACETONE,G4_ACETYLENE,G4_ADENINE,G4_ADIPOSE_TISSUE_ICRP,G4_AIR,G4_ALANINE,G4_ALUMINUM_OXIDE,G4_AMBER,G4_AMMONIA,G4_ANILINE,G4_ANTHRACENE,G4_B_100_BONE,G4_BAKELITE,G4_BARIUM_FLUORIDE,G4_BARIUM_SULFATE,G4_BENZENE,G4_BERYLLIUM_OXIDE,G4_BGO,G4_BLOOD_ICRP,G4_BONE_COMPACT_ICRU,G4_BONE_CORTICAL_ICRP,G4_BORON_CARBIDE,G4_BORON_OXIDE,G4_BRAIN_ICRP,G4_BUTANE,G4_N_BUTYL_ALCOHOL,G4_C_552,+152 more]
FEATURE [App::DocumentObjectGroupPython] H_element113  label="H_element : 062"  # scripted group (container) (typed FeaturePython)
  n = 1
  ref = H_element
FEATURE [App::DocumentObjectGroupPython] G4_H  # scripted group (container) (typed FeaturePython)
  Dunit = g/cm3
  Dvalue = 8.3748e-05
  Group = -> [H_element113]
  conduct = 2
  density = 1
  expand = 3
  formula = H
  name = G4_H
  specific = 4
FEATURE [App::DocumentObjectGroupPython] He_element001  label="He_element : 1"  # scripted group (container) (typed FeaturePython)
  n = 1
  ref = He_element
FEATURE [App::DocumentObjectGroupPython] G4_He  # scripted group (container) (typed FeaturePython)
  Dunit = g/cm3
  Dvalue = 0.000166322
  Group = -> [He_element001]
  conduct = 2
  density = 1
  expand = 3
  formula = He
  name = G4_He
  specific = 4
FEATURE [App::DocumentObjectGroupPython] Li_element008  label="Li_element : 008"  # scripted group (container) (typed FeaturePython)
  n = 1
  ref = Li_element
FEATURE [App::DocumentObjectGroupPython] G4_Li  # scripted group (container) (typed FeaturePython)
  Dunit = g/cm3
  Dvalue = 0.534
  Group = -> [Li_element008]
  conduct = 2
  density = 1
  expand = 3
  formula = Li
  name = G4_Li
  specific = 4
FEATURE [App::DocumentObjectGroupPython] Be_element002  label="Be_element : 002"  # scripted group (container) (typed FeaturePython)
  n = 1
  ref = Be_element
FEATURE [App::DocumentObjectGroupPython] G4_Be  # scripted group (container) (typed FeaturePython)
  Dunit = g/cm3
  Dvalue = 1.848
  Group = -> [Be_element002]
  conduct = 2
  density = 1
  expand = 3
  formula = Be
  name = G4_Be
  specific = 4
FEATURE [App::DocumentObjectGroupPython] B_element007  label="B_element : 007"  # scripted group (container) (typed FeaturePython)
  n = 1
  ref = B_element
FEATURE [App::DocumentObjectGroupPython] G4_B  # scripted group (container) (typed FeaturePython)
  Dunit = g/cm3
  Dvalue = 2.37
  Group = -> [B_element007]
  conduct = 2
  density = 1
  expand = 3
  formula = B
  name = G4_B
  specific = 4
FEATURE [App::DocumentObjectGroupPython] C_element124  label="C_element : 070"  # scripted group (container) (typed FeaturePython)
  n = 1
  ref = C_element
FEATURE [App::DocumentObjectGroupPython] G4_C  # scripted group (container) (typed FeaturePython)
  Dunit = g/cm3
  Dvalue = 2
  Group = -> [C_element124]
  conduct = 2
  density = 1
  expand = 3
  formula = C
  name = G4_C
  specific = 4
FEATURE [App::DocumentObjectGroupPython] N_element048  label="N_element : 021"  # scripted group (container) (typed FeaturePython)
  n = 1
  ref = N_element
FEATURE [App::DocumentObjectGroupPython] G4_N  # scripted group (container) (typed FeaturePython)
  Dunit = g/cm3
  Dvalue = 0.0011652
  Group = -> [N_element048]
  conduct = 2
  density = 1
  expand = 3
  formula = N
  name = G4_N
  specific = 4
FEATURE [App::DocumentObjectGroupPython] O_element105  label="O_element : 059"  # scripted group (container) (typed FeaturePython)
  n = 1
  ref = O_element
FEATURE [App::DocumentObjectGroupPython] G4_O  # scripted group (container) (typed FeaturePython)
  Dunit = g/cm3
  Dvalue = 0.00133151
  Group = -> [O_element105]
  conduct = 2
  density = 1
  expand = 3
  formula = O
  name = G4_O
  specific = 4
FEATURE [App::DocumentObjectGroupPython] F_element019  label="F_element : 008"  # scripted group (container) (typed FeaturePython)
  n = 1
  ref = F_element
FEATURE [App::DocumentObjectGroupPython] G4_F  # scripted group (container) (typed FeaturePython)
  Dunit = g/cm3
  Dvalue = 0.00158029
  Group = -> [F_element019]
  conduct = 2
  density = 1
  expand = 3
  formula = F
  name = G4_F
  specific = 4
FEATURE [App::DocumentObjectGroupPython] Ne_element001  label="Ne_element : 1"  # scripted group (container) (typed FeaturePython)
  n = 1
  ref = Ne_element
FEATURE [App::DocumentObjectGroupPython] G4_Ne  # scripted group (container) (typed FeaturePython)
  Dunit = g/cm3
  Dvalue = 0.000838505
  Group = -> [Ne_element001]
  conduct = 2
  density = 1
  expand = 3
  formula = Ne
  name = G4_Ne
  specific = 4
FEATURE [App::DocumentObjectGroupPython] Na_element020  label="Na_element : 005"  # scripted group (container) (typed FeaturePython)
  n = 1
  ref = Na_element
FEATURE [App::DocumentObjectGroupPython] G4_Na  # scripted group (container) (typed FeaturePython)
  Dunit = g/cm3
  Dvalue = 0.971
  Group = -> [Na_element020]
  conduct = 2
  density = 1
  expand = 3
  formula = Na
  name = G4_Na
  specific = 4
FEATURE [App::DocumentObjectGroupPython] Mg_element011  label="Mg_element : 005"  # scripted group (container) (typed FeaturePython)
  n = 1
  ref = Mg_element
FEATURE [App::DocumentObjectGroupPython] G4_Mg  # scripted group (container) (typed FeaturePython)
  Dunit = g/cm3
  Dvalue = 1.74
  Group = -> [Mg_element011]
  conduct = 2
  density = 1
  expand = 3
  formula = Mg
  name = G4_Mg
  specific = 4
FEATURE [App::DocumentObjectGroupPython] Al_element004  label="Al_element : 1"  # scripted group (container) (typed FeaturePython)
  n = 1
  ref = Al_element
FEATURE [App::DocumentObjectGroupPython] G4_Al  # scripted group (container) (typed FeaturePython)
  Dunit = g/cm3
  Dvalue = 2.699
  Group = -> [Al_element004]
  conduct = 2
  density = 1
  expand = 3
  formula = Al
  name = G4_Al
  specific = 4
FEATURE [App::DocumentObjectGroupPython] Si_element007  label="Si_element : 002"  # scripted group (container) (typed FeaturePython)
  n = 1
  ref = Si_element
FEATURE [App::DocumentObjectGroupPython] G4_Si  # scripted group (container) (typed FeaturePython)
  Dunit = g/cm3
  Dvalue = 2.33
  Group = -> [Si_element007]
  conduct = 2
  density = 1
  expand = 3
  formula = Si
  name = G4_Si
  specific = 4
FEATURE [App::DocumentObjectGroupPython] P_element013  label="P_element : 002"  # scripted group (container) (typed FeaturePython)
  n = 1
  ref = P_element
FEATURE [App::DocumentObjectGroupPython] G4_P  # scripted group (container) (typed FeaturePython)
  Dunit = g/cm3
  Dvalue = 2.2
  Group = -> [P_element013]
  conduct = 2
  density = 1
  expand = 3
  formula = P
  name = G4_P
  specific = 4
FEATURE [App::DocumentObjectGroupPython] S_element023  label="S_element : 007"  # scripted group (container) (typed FeaturePython)
  n = 1
  ref = S_element
FEATURE [App::DocumentObjectGroupPython] G4_S  # scripted group (container) (typed FeaturePython)
  Dunit = g/cm3
  Dvalue = 2
  Group = -> [S_element023]
  conduct = 2
  density = 1
  expand = 3
  formula = S
  name = G4_S
  specific = 4
FEATURE [App::DocumentObjectGroupPython] Cl_element029  label="Cl_element : 015"  # scripted group (container) (typed FeaturePython)
  n = 1
  ref = Cl_element
FEATURE [App::DocumentObjectGroupPython] G4_Cl  # scripted group (container) (typed FeaturePython)
  Dunit = g/cm3
  Dvalue = 0.00299473
  Group = -> [Cl_element029]
  conduct = 2
  density = 1
  expand = 3
  formula = Cl
  name = G4_Cl
  specific = 4
FEATURE [App::DocumentObjectGroupPython] Ar_element002  label="Ar_element : 1"  # scripted group (container) (typed FeaturePython)
  n = 1
  ref = Ar_element
FEATURE [App::DocumentObjectGroupPython] G4_Ar  # scripted group (container) (typed FeaturePython)
  Dunit = g/cm3
  Dvalue = 0.00166201
  Group = -> [Ar_element002]
  conduct = 2
  density = 1
  expand = 3
  formula = Ar
  name = G4_Ar
  specific = 4
FEATURE [App::DocumentObjectGroupPython] K_element013  label="K_element : 003"  # scripted group (container) (typed FeaturePython)
  n = 1
  ref = K_element
FEATURE [App::DocumentObjectGroupPython] G4_K  # scripted group (container) (typed FeaturePython)
  Dunit = g/cm3
  Dvalue = 0.862
  Group = -> [K_element013]
  conduct = 2
  density = 1
  expand = 3
  formula = K
  name = G4_K
  specific = 4
FEATURE [App::DocumentObjectGroupPython] Ca_element014  label="Ca_element : 007"  # scripted group (container) (typed FeaturePython)
  n = 1
  ref = Ca_element
FEATURE [App::DocumentObjectGroupPython] G4_Ca  # scripted group (container) (typed FeaturePython)
  Dunit = g/cm3
  Dvalue = 1.55
  Group = -> [Ca_element014]
  conduct = 2
  density = 1
  expand = 3
  formula = Ca
  name = G4_Ca
  specific = 4
FEATURE [App::DocumentObjectGroupPython] Sc_element001  label="Sc_element : 1"  # scripted group (container) (typed FeaturePython)
  n = 1
  ref = Sc_element
FEATURE [App::DocumentObjectGroupPython] G4_Sc  # scripted group (container) (typed FeaturePython)
  Dunit = g/cm3
  Dvalue = 2.989
  Group = -> [Sc_element001]
  conduct = 2
  density = 1
  expand = 3
  formula = Sc
  name = G4_Sc
  specific = 4
FEATURE [App::DocumentObjectGroupPython] Ti_element004  label="Ti_element : 002"  # scripted group (container) (typed FeaturePython)
  n = 1
  ref = Ti_element
FEATURE [App::DocumentObjectGroupPython] G4_Ti  # scripted group (container) (typed FeaturePython)
  Dunit = g/cm3
  Dvalue = 4.54
  Group = -> [Ti_element004]
  conduct = 2
  density = 1
  expand = 3
  formula = Ti
  name = G4_Ti
  specific = 4
FEATURE [App::DocumentObjectGroupPython] V_element001  label="V_element : 1"  # scripted group (container) (typed FeaturePython)
  n = 1
  ref = V_element
FEATURE [App::DocumentObjectGroupPython] G4_V  # scripted group (container) (typed FeaturePython)
  Dunit = g/cm3
  Dvalue = 6.11
  Group = -> [V_element001]
  conduct = 2
  density = 1
  expand = 3
  formula = V
  name = G4_V
  specific = 4
FEATURE [App::DocumentObjectGroupPython] Cr_element001  label="Cr_element : 1"  # scripted group (container) (typed FeaturePython)
  n = 1
  ref = Cr_element
FEATURE [App::DocumentObjectGroupPython] G4_Cr  # scripted group (container) (typed FeaturePython)
  Dunit = g/cm3
  Dvalue = 7.18
  Group = -> [Cr_element001]
  conduct = 2
  density = 1
  expand = 3
  formula = Cr
  name = G4_Cr
  specific = 4
FEATURE [App::DocumentObjectGroupPython] Mn_element001  label="Mn_element : 1"  # scripted group (container) (typed FeaturePython)
  n = 1
  ref = Mn_element
FEATURE [App::DocumentObjectGroupPython] G4_Mn  # scripted group (container) (typed FeaturePython)
  Dunit = g/cm3
  Dvalue = 7.44
  Group = -> [Mn_element001]
  conduct = 2
  density = 1
  expand = 3
  formula = Mn
  name = G4_Mn
  specific = 4
FEATURE [App::DocumentObjectGroupPython] Fe_element007  label="Fe_element : 004"  # scripted group (container) (typed FeaturePython)
  n = 1
  ref = Fe_element
FEATURE [App::DocumentObjectGroupPython] G4_Fe  # scripted group (container) (typed FeaturePython)
  Dunit = g/cm3
  Dvalue = 7.874
  Group = -> [Fe_element007]
  conduct = 2
  density = 1
  expand = 3
  formula = Fe
  name = G4_Fe
  specific = 4
FEATURE [App::DocumentObjectGroupPython] Co_element001  label="Co_element : 1"  # scripted group (container) (typed FeaturePython)
  n = 1
  ref = Co_element
FEATURE [App::DocumentObjectGroupPython] G4_Co  # scripted group (container) (typed FeaturePython)
  Dunit = g/cm3
  Dvalue = 8.9
  Group = -> [Co_element001]
  conduct = 2
  density = 1
  expand = 3
  formula = Co
  name = G4_Co
  specific = 4
FEATURE [App::DocumentObjectGroupPython] Ni_element001  label="Ni_element : 1"  # scripted group (container) (typed FeaturePython)
  n = 1
  ref = Ni_element
FEATURE [App::DocumentObjectGroupPython] G4_Ni  # scripted group (container) (typed FeaturePython)
  Dunit = g/cm3
  Dvalue = 8.902
  Group = -> [Ni_element001]
  conduct = 2
  density = 1
  expand = 3
  formula = Ni
  name = G4_Ni
  specific = 4
FEATURE [App::DocumentObjectGroupPython] Cu_element001  label="Cu_element : 1"  # scripted group (container) (typed FeaturePython)
  n = 1
  ref = Cu_element
FEATURE [App::DocumentObjectGroupPython] G4_Cu  # scripted group (container) (typed FeaturePython)
  Dunit = g/cm3
  Dvalue = 8.96
  Group = -> [Cu_element001]
  conduct = 2
  density = 1
  expand = 3
  formula = Cu
  name = G4_Cu
  specific = 4
FEATURE [App::DocumentObjectGroupPython] Zn_element001  label="Zn_element : 1"  # scripted group (container) (typed FeaturePython)
  n = 1
  ref = Zn_element
FEATURE [App::DocumentObjectGroupPython] G4_Zn  # scripted group (container) (typed FeaturePython)
  Dunit = g/cm3
  Dvalue = 7.133
  Group = -> [Zn_element001]
  conduct = 2
  density = 1
  expand = 3
  formula = Zn
  name = G4_Zn
  specific = 4
FEATURE [App::DocumentObjectGroupPython] Ga_element002  label="Ga_element : 002"  # scripted group (container) (typed FeaturePython)
  n = 1
  ref = Ga_element
FEATURE [App::DocumentObjectGroupPython] G4_Ga  # scripted group (container) (typed FeaturePython)
  Dunit = g/cm3
  Dvalue = 5.904
  Group = -> [Ga_element002]
  conduct = 2
  density = 1
  expand = 3
  formula = Ga
  name = G4_Ga
  specific = 4
FEATURE [App::DocumentObjectGroupPython] Ge_element002  label="Ge_element : 1"  # scripted group (container) (typed FeaturePython)
  n = 1
  ref = Ge_element
FEATURE [App::DocumentObjectGroupPython] G4_Ge  # scripted group (container) (typed FeaturePython)
  Dunit = g/cm3
  Dvalue = 5.323
  Group = -> [Ge_element002]
  conduct = 2
  density = 1
  expand = 3
  formula = Ge
  name = G4_Ge
  specific = 4
FEATURE [App::DocumentObjectGroupPython] As_element003  label="As_element : 002"  # scripted group (container) (typed FeaturePython)
  n = 1
  ref = As_element
FEATURE [App::DocumentObjectGroupPython] G4_As  # scripted group (container) (typed FeaturePython)
  Dunit = g/cm3
  Dvalue = 5.73
  Group = -> [As_element003]
  conduct = 2
  density = 1
  expand = 3
  formula = As
  name = G4_As
  specific = 4
FEATURE [App::DocumentObjectGroupPython] Se_element001  label="Se_element : 1"  # scripted group (container) (typed FeaturePython)
  n = 1
  ref = Se_element
FEATURE [App::DocumentObjectGroupPython] G4_Se  # scripted group (container) (typed FeaturePython)
  Dunit = g/cm3
  Dvalue = 4.5
  Group = -> [Se_element001]
  conduct = 2
  density = 1
  expand = 3
  formula = Se
  name = G4_Se
  specific = 4
FEATURE [App::DocumentObjectGroupPython] Br_element007  label="Br_element : 004"  # scripted group (container) (typed FeaturePython)
  n = 1
  ref = Br_element
FEATURE [App::DocumentObjectGroupPython] G4_Br  # scripted group (container) (typed FeaturePython)
  Dunit = g/cm3
  Dvalue = 0.0070721
  Group = -> [Br_element007]
  conduct = 2
  density = 1
  expand = 3
  formula = Br
  name = G4_Br
  specific = 4
FEATURE [App::DocumentObjectGroupPython] Kr_element001  label="Kr_element : 1"  # scripted group (container) (typed FeaturePython)
  n = 1
  ref = Kr_element
FEATURE [App::DocumentObjectGroupPython] G4_Kr  # scripted group (container) (typed FeaturePython)
  Dunit = g/cm3
  Dvalue = 0.00347832
  Group = -> [Kr_element001]
  conduct = 2
  density = 1
  expand = 3
  formula = Kr
  name = G4_Kr
  specific = 4
FEATURE [App::DocumentObjectGroupPython] Rb_element001  label="Rb_element : 1"  # scripted group (container) (typed FeaturePython)
  n = 1
  ref = Rb_element
FEATURE [App::DocumentObjectGroupPython] G4_Rb  # scripted group (container) (typed FeaturePython)
  Dunit = g/cm3
  Dvalue = 1.532
  Group = -> [Rb_element001]
  conduct = 2
  density = 1
  expand = 3
  formula = Rb
  name = G4_Rb
  specific = 4
FEATURE [App::DocumentObjectGroupPython] Sr_element001  label="Sr_element : 1"  # scripted group (container) (typed FeaturePython)
  n = 1
  ref = Sr_element
FEATURE [App::DocumentObjectGroupPython] G4_Sr  # scripted group (container) (typed FeaturePython)
  Dunit = g/cm3
  Dvalue = 2.54
  Group = -> [Sr_element001]
  conduct = 2
  density = 1
  expand = 3
  formula = Sr
  name = G4_Sr
  specific = 4
FEATURE [App::DocumentObjectGroupPython] Y_element001  label="Y_element : 1"  # scripted group (container) (typed FeaturePython)
  n = 1
  ref = Y_element
FEATURE [App::DocumentObjectGroupPython] G4_Y  # scripted group (container) (typed FeaturePython)
  Dunit = g/cm3
  Dvalue = 4.469
  Group = -> [Y_element001]
  conduct = 2
  density = 1
  expand = 3
  formula = Y
  name = G4_Y
  specific = 4
FEATURE [App::DocumentObjectGroupPython] Zr_element001  label="Zr_element : 1"  # scripted group (container) (typed FeaturePython)
  n = 1
  ref = Zr_element
FEATURE [App::DocumentObjectGroupPython] G4_Zr  # scripted group (container) (typed FeaturePython)
  Dunit = g/cm3
  Dvalue = 6.506
  Group = -> [Zr_element001]
  conduct = 2
  density = 1
  expand = 3
  formula = Zr
  name = G4_Zr
  specific = 4
FEATURE [App::DocumentObjectGroupPython] Nb_element001  label="Nb_element : 1"  # scripted group (container) (typed FeaturePython)
  n = 1
  ref = Nb_element
FEATURE [App::DocumentObjectGroupPython] G4_Nb  # scripted group (container) (typed FeaturePython)
  Dunit = g/cm3
  Dvalue = 8.57
  Group = -> [Nb_element001]
  conduct = 2
  density = 1
  expand = 3
  formula = Nb
  name = G4_Nb
  specific = 4
FEATURE [App::DocumentObjectGroupPython] Mo_element001  label="Mo_element : 1"  # scripted group (container) (typed FeaturePython)
  n = 1
  ref = Mo_element
FEATURE [App::DocumentObjectGroupPython] G4_Mo  # scripted group (container) (typed FeaturePython)
  Dunit = g/cm3
  Dvalue = 10.22
  Group = -> [Mo_element001]
  conduct = 2
  density = 1
  expand = 3
  formula = Mo
  name = G4_Mo
  specific = 4
FEATURE [App::DocumentObjectGroupPython] Tc_element001  label="Tc_element : 1"  # scripted group (container) (typed FeaturePython)
  n = 1
  ref = Tc_element
FEATURE [App::DocumentObjectGroupPython] G4_Tc  # scripted group (container) (typed FeaturePython)
  Dunit = g/cm3
  Dvalue = 11.5
  Group = -> [Tc_element001]
  conduct = 2
  density = 1
  expand = 3
  formula = Tc
  name = G4_Tc
  specific = 4
FEATURE [App::DocumentObjectGroupPython] Ru_element001  label="Ru_element : 1"  # scripted group (container) (typed FeaturePython)
  n = 1
  ref = Ru_element
FEATURE [App::DocumentObjectGroupPython] G4_Ru  # scripted group (container) (typed FeaturePython)
  Dunit = g/cm3
  Dvalue = 12.41
  Group = -> [Ru_element001]
  conduct = 2
  density = 1
  expand = 3
  formula = Ru
  name = G4_Ru
  specific = 4
FEATURE [App::DocumentObjectGroupPython] Rh_element001  label="Rh_element : 1"  # scripted group (container) (typed FeaturePython)
  n = 1
  ref = Rh_element
FEATURE [App::DocumentObjectGroupPython] G4_Rh  # scripted group (container) (typed FeaturePython)
  Dunit = g/cm3
  Dvalue = 12.41
  Group = -> [Rh_element001]
  conduct = 2
  density = 1
  expand = 3
  formula = Rh
  name = G4_Rh
  specific = 4
FEATURE [App::DocumentObjectGroupPython] Pd_element001  label="Pd_element : 1"  # scripted group (container) (typed FeaturePython)
  n = 1
  ref = Pd_element
FEATURE [App::DocumentObjectGroupPython] G4_Pd  # scripted group (container) (typed FeaturePython)
  Dunit = g/cm3
  Dvalue = 12.02
  Group = -> [Pd_element001]
  conduct = 2
  density = 1
  expand = 3
  formula = Pd
  name = G4_Pd
  specific = 4
FEATURE [App::DocumentObjectGroupPython] Ag_element006  label="Ag_element : 004"  # scripted group (container) (typed FeaturePython)
  n = 1
  ref = Ag_element
FEATURE [App::DocumentObjectGroupPython] G4_Ag  # scripted group (container) (typed FeaturePython)
  Dunit = g/cm3
  Dvalue = 10.5
  Group = -> [Ag_element006]
  conduct = 2
  density = 1
  expand = 3
  formula = Ag
  name = G4_Ag
  specific = 4
FEATURE [App::DocumentObjectGroupPython] Cd_element003  label="Cd_element : 003"  # scripted group (container) (typed FeaturePython)
  n = 1
  ref = Cd_element
FEATURE [App::DocumentObjectGroupPython] G4_Cd  # scripted group (container) (typed FeaturePython)
  Dunit = g/cm3
  Dvalue = 8.65
  Group = -> [Cd_element003]
  conduct = 2
  density = 1
  expand = 3
  formula = Cd
  name = G4_Cd
  specific = 4
FEATURE [App::DocumentObjectGroupPython] In_element001  label="In_element : 1"  # scripted group (container) (typed FeaturePython)
  n = 1
  ref = In_element
FEATURE [App::DocumentObjectGroupPython] G4_In  # scripted group (container) (typed FeaturePython)
  Dunit = g/cm3
  Dvalue = 7.31
  Group = -> [In_element001]
  conduct = 2
  density = 1
  expand = 3
  formula = In
  name = G4_In
  specific = 4
FEATURE [App::DocumentObjectGroupPython] Sn_element001  label="Sn_element : 1"  # scripted group (container) (typed FeaturePython)
  n = 1
  ref = Sn_element
FEATURE [App::DocumentObjectGroupPython] G4_Sn  # scripted group (container) (typed FeaturePython)
  Dunit = g/cm3
  Dvalue = 7.31
  Group = -> [Sn_element001]
  conduct = 2
  density = 1
  expand = 3
  formula = Sn
  name = G4_Sn
  specific = 4
FEATURE [App::DocumentObjectGroupPython] Sb_element001  label="Sb_element : 1"  # scripted group (container) (typed FeaturePython)
  n = 1
  ref = Sb_element
FEATURE [App::DocumentObjectGroupPython] G4_Sb  # scripted group (container) (typed FeaturePython)
  Dunit = g/cm3
  Dvalue = 6.691
  Group = -> [Sb_element001]
  conduct = 2
  density = 1
  expand = 3
  formula = Sb
  name = G4_Sb
  specific = 4
FEATURE [App::DocumentObjectGroupPython] Te_element002  label="Te_element : 002"  # scripted group (container) (typed FeaturePython)
  n = 1
  ref = Te_element
FEATURE [App::DocumentObjectGroupPython] G4_Te  # scripted group (container) (typed FeaturePython)
  Dunit = g/cm3
  Dvalue = 6.24
  Group = -> [Te_element002]
  conduct = 2
  density = 1
  expand = 3
  formula = Te
  name = G4_Te
  specific = 4
FEATURE [App::DocumentObjectGroupPython] I_element010  label="I_element : 006"  # scripted group (container) (typed FeaturePython)
  n = 1
  ref = I_element
FEATURE [App::DocumentObjectGroupPython] G4_I  # scripted group (container) (typed FeaturePython)
  Dunit = g/cm3
  Dvalue = 4.93
  Group = -> [I_element010]
  conduct = 2
  density = 1
  expand = 3
  formula = I
  name = G4_I
  specific = 4
FEATURE [App::DocumentObjectGroupPython] Xe_element001  label="Xe_element : 1"  # scripted group (container) (typed FeaturePython)
  n = 1
  ref = Xe_element
FEATURE [App::DocumentObjectGroupPython] G4_Xe  # scripted group (container) (typed FeaturePython)
  Dunit = g/cm3
  Dvalue = 0.00548536
  Group = -> [Xe_element001]
  conduct = 2
  density = 1
  expand = 3
  formula = Xe
  name = G4_Xe
  specific = 4
FEATURE [App::DocumentObjectGroupPython] Cs_element003  label="Cs_element : 003"  # scripted group (container) (typed FeaturePython)
  n = 1
  ref = Cs_element
FEATURE [App::DocumentObjectGroupPython] G4_Cs  # scripted group (container) (typed FeaturePython)
  Dunit = g/cm3
  Dvalue = 1.873
  Group = -> [Cs_element003]
  conduct = 2
  density = 1
  expand = 3
  formula = Cs
  name = G4_Cs
  specific = 4
FEATURE [App::DocumentObjectGroupPython] Ba_element003  label="Ba_element : 003"  # scripted group (container) (typed FeaturePython)
  n = 1
  ref = Ba_element
FEATURE [App::DocumentObjectGroupPython] G4_Ba  # scripted group (container) (typed FeaturePython)
  Dunit = g/cm3
  Dvalue = 3.5
  Group = -> [Ba_element003]
  conduct = 2
  density = 1
  expand = 3
  formula = Ba
  name = G4_Ba
  specific = 4
FEATURE [App::DocumentObjectGroupPython] La_element003  label="La_element : 003"  # scripted group (container) (typed FeaturePython)
  n = 1
  ref = La_element
FEATURE [App::DocumentObjectGroupPython] G4_La  # scripted group (container) (typed FeaturePython)
  Dunit = g/cm3
  Dvalue = 6.154
  Group = -> [La_element003]
  conduct = 2
  density = 1
  expand = 3
  formula = La
  name = G4_La
  specific = 4
FEATURE [App::DocumentObjectGroupPython] Ce_element002  label="Ce_element : 1"  # scripted group (container) (typed FeaturePython)
  n = 1
  ref = Ce_element
FEATURE [App::DocumentObjectGroupPython] G4_Ce  # scripted group (container) (typed FeaturePython)
  Dunit = g/cm3
  Dvalue = 6.657
  Group = -> [Ce_element002]
  conduct = 2
  density = 1
  expand = 3
  formula = Ce
  name = G4_Ce
  specific = 4
FEATURE [App::DocumentObjectGroupPython] Pr_element001  label="Pr_element : 1"  # scripted group (container) (typed FeaturePython)
  n = 1
  ref = Pr_element
FEATURE [App::DocumentObjectGroupPython] G4_Pr  # scripted group (container) (typed FeaturePython)
  Dunit = g/cm3
  Dvalue = 6.71
  Group = -> [Pr_element001]
  conduct = 2
  density = 1
  expand = 3
  formula = Pr
  name = G4_Pr
  specific = 4
FEATURE [App::DocumentObjectGroupPython] Nd_element001  label="Nd_element : 1"  # scripted group (container) (typed FeaturePython)
  n = 1
  ref = Nd_element
FEATURE [App::DocumentObjectGroupPython] G4_Nd  # scripted group (container) (typed FeaturePython)
  Dunit = g/cm3
  Dvalue = 6.9
  Group = -> [Nd_element001]
  conduct = 2
  density = 1
  expand = 3
  formula = Nd
  name = G4_Nd
  specific = 4
FEATURE [App::DocumentObjectGroupPython] Pm_element001  label="Pm_element : 1"  # scripted group (container) (typed FeaturePython)
  n = 1
  ref = Pm_element
FEATURE [App::DocumentObjectGroupPython] G4_Pm  # scripted group (container) (typed FeaturePython)
  Dunit = g/cm3
  Dvalue = 7.22
  Group = -> [Pm_element001]
  conduct = 2
  density = 1
  expand = 3
  formula = Pm
  name = G4_Pm
  specific = 4
FEATURE [App::DocumentObjectGroupPython] Sm_element001  label="Sm_element : 1"  # scripted group (container) (typed FeaturePython)
  n = 1
  ref = Sm_element
FEATURE [App::DocumentObjectGroupPython] G4_Sm  # scripted group (container) (typed FeaturePython)
  Dunit = g/cm3
  Dvalue = 7.46
  Group = -> [Sm_element001]
  conduct = 2
  density = 1
  expand = 3
  formula = Sm
  name = G4_Sm
  specific = 4
FEATURE [App::DocumentObjectGroupPython] Eu_element001  label="Eu_element : 1"  # scripted group (container) (typed FeaturePython)
  n = 1
  ref = Eu_element
FEATURE [App::DocumentObjectGroupPython] G4_Eu  # scripted group (container) (typed FeaturePython)
  Dunit = g/cm3
  Dvalue = 5.243
  Group = -> [Eu_element001]
  conduct = 2
  density = 1
  expand = 3
  formula = Eu
  name = G4_Eu
  specific = 4
FEATURE [App::DocumentObjectGroupPython] Gd_element002  label="Gd_element : 1"  # scripted group (container) (typed FeaturePython)
  n = 1
  ref = Gd_element
FEATURE [App::DocumentObjectGroupPython] G4_Gd  # scripted group (container) (typed FeaturePython)
  Dunit = g/cm3
  Dvalue = 7.9004
  Group = -> [Gd_element002]
  conduct = 2
  density = 1
  expand = 3
  formula = Gd
  name = G4_Gd
  specific = 4
FEATURE [App::DocumentObjectGroupPython] Tb_element001  label="Tb_element : 1"  # scripted group (container) (typed FeaturePython)
  n = 1
  ref = Tb_element
FEATURE [App::DocumentObjectGroupPython] G4_Tb  # scripted group (container) (typed FeaturePython)
  Dunit = g/cm3
  Dvalue = 8.229
  Group = -> [Tb_element001]
  conduct = 2
  density = 1
  expand = 3
  formula = Tb
  name = G4_Tb
  specific = 4
FEATURE [App::DocumentObjectGroupPython] Dy_element001  label="Dy_element : 1"  # scripted group (container) (typed FeaturePython)
  n = 1
  ref = Dy_element
FEATURE [App::DocumentObjectGroupPython] G4_Dy  # scripted group (container) (typed FeaturePython)
  Dunit = g/cm3
  Dvalue = 8.55
  Group = -> [Dy_element001]
  conduct = 2
  density = 1
  expand = 3
  formula = Dy
  name = G4_Dy
  specific = 4
FEATURE [App::DocumentObjectGroupPython] Ho_element001  label="Ho_element : 1"  # scripted group (container) (typed FeaturePython)
  n = 1
  ref = Ho_element
FEATURE [App::DocumentObjectGroupPython] G4_Ho  # scripted group (container) (typed FeaturePython)
  Dunit = g/cm3
  Dvalue = 8.795
  Group = -> [Ho_element001]
  conduct = 2
  density = 1
  expand = 3
  formula = Ho
  name = G4_Ho
  specific = 4
FEATURE [App::DocumentObjectGroupPython] Er_element001  label="Er_element : 1"  # scripted group (container) (typed FeaturePython)
  n = 1
  ref = Er_element
FEATURE [App::DocumentObjectGroupPython] G4_Er  # scripted group (container) (typed FeaturePython)
  Dunit = g/cm3
  Dvalue = 9.066
  Group = -> [Er_element001]
  conduct = 2
  density = 1
  expand = 3
  formula = Er
  name = G4_Er
  specific = 4
FEATURE [App::DocumentObjectGroupPython] Tm_element001  label="Tm_element : 1"  # scripted group (container) (typed FeaturePython)
  n = 1
  ref = Tm_element
FEATURE [App::DocumentObjectGroupPython] G4_Tm  # scripted group (container) (typed FeaturePython)
  Dunit = g/cm3
  Dvalue = 9.321
  Group = -> [Tm_element001]
  conduct = 2
  density = 1
  expand = 3
  formula = Tm
  name = G4_Tm
  specific = 4
FEATURE [App::DocumentObjectGroupPython] Yb_element001  label="Yb_element : 1"  # scripted group (container) (typed FeaturePython)
  n = 1
  ref = Yb_element
FEATURE [App::DocumentObjectGroupPython] G4_Yb  # scripted group (container) (typed FeaturePython)
  Dunit = g/cm3
  Dvalue = 6.73
  Group = -> [Yb_element001]
  conduct = 2
  density = 1
  expand = 3
  formula = Yb
  name = G4_Yb
  specific = 4
FEATURE [App::DocumentObjectGroupPython] Lu_element001  label="Lu_element : 1"  # scripted group (container) (typed FeaturePython)
  n = 1
  ref = Lu_element
FEATURE [App::DocumentObjectGroupPython] G4_Lu  # scripted group (container) (typed FeaturePython)
  Dunit = g/cm3
  Dvalue = 9.84
  Group = -> [Lu_element001]
  conduct = 2
  density = 1
  expand = 3
  formula = Lu
  name = G4_Lu
  specific = 4
FEATURE [App::DocumentObjectGroupPython] Hf_element001  label="Hf_element : 1"  # scripted group (container) (typed FeaturePython)
  n = 1
  ref = Hf_element
FEATURE [App::DocumentObjectGroupPython] G4_Hf  # scripted group (container) (typed FeaturePython)
  Dunit = g/cm3
  Dvalue = 13.31
  Group = -> [Hf_element001]
  conduct = 2
  density = 1
  expand = 3
  formula = Hf
  name = G4_Hf
  specific = 4
FEATURE [App::DocumentObjectGroupPython] Ta_element001  label="Ta_element : 1"  # scripted group (container) (typed FeaturePython)
  n = 1
  ref = Ta_element
FEATURE [App::DocumentObjectGroupPython] G4_Ta  # scripted group (container) (typed FeaturePython)
  Dunit = g/cm3
  Dvalue = 16.654
  Group = -> [Ta_element001]
  conduct = 2
  density = 1
  expand = 3
  formula = Ta
  name = G4_Ta
  specific = 4
FEATURE [App::DocumentObjectGroupPython] W_element004  label="W_element : 004"  # scripted group (container) (typed FeaturePython)
  n = 1
  ref = W_element
FEATURE [App::DocumentObjectGroupPython] G4_W  # scripted group (container) (typed FeaturePython)
  Dunit = g/cm3
  Dvalue = 19.3
  Group = -> [W_element004]
  conduct = 2
  density = 1
  expand = 3
  formula = W
  name = G4_W
  specific = 4
FEATURE [App::DocumentObjectGroupPython] Re_element001  label="Re_element : 1"  # scripted group (container) (typed FeaturePython)
  n = 1
  ref = Re_element
FEATURE [App::DocumentObjectGroupPython] G4_Re  # scripted group (container) (typed FeaturePython)
  Dunit = g/cm3
  Dvalue = 21.02
  Group = -> [Re_element001]
  conduct = 2
  density = 1
  expand = 3
  formula = Re
  name = G4_Re
  specific = 4
FEATURE [App::DocumentObjectGroupPython] Os_element001  label="Os_element : 1"  # scripted group (container) (typed FeaturePython)
  n = 1
  ref = Os_element
FEATURE [App::DocumentObjectGroupPython] G4_Os  # scripted group (container) (typed FeaturePython)
  Dunit = g/cm3
  Dvalue = 22.57
  Group = -> [Os_element001]
  conduct = 2
  density = 1
  expand = 3
  formula = Os
  name = G4_Os
  specific = 4
FEATURE [App::DocumentObjectGroupPython] Ir_element001  label="Ir_element : 1"  # scripted group (container) (typed FeaturePython)
  n = 1
  ref = Ir_element
FEATURE [App::DocumentObjectGroupPython] G4_Ir  # scripted group (container) (typed FeaturePython)
  Dunit = g/cm3
  Dvalue = 22.42
  Group = -> [Ir_element001]
  conduct = 2
  density = 1
  expand = 3
  formula = Ir
  name = G4_Ir
  specific = 4
FEATURE [App::DocumentObjectGroupPython] Pt_element001  label="Pt_element : 1"  # scripted group (container) (typed FeaturePython)
  n = 1
  ref = Pt_element
FEATURE [App::DocumentObjectGroupPython] G4_Pt  # scripted group (container) (typed FeaturePython)
  Dunit = g/cm3
  Dvalue = 21.45
  Group = -> [Pt_element001]
  conduct = 2
  density = 1
  expand = 3
  formula = Pt
  name = G4_Pt
  specific = 4
FEATURE [App::DocumentObjectGroupPython] Au_element001  label="Au_element : 1"  # scripted group (container) (typed FeaturePython)
  n = 1
  ref = Au_element
FEATURE [App::DocumentObjectGroupPython] G4_Au  # scripted group (container) (typed FeaturePython)
  Dunit = g/cm3
  Dvalue = 19.32
  Group = -> [Au_element001]
  conduct = 2
  density = 1
  expand = 3
  formula = Au
  name = G4_Au
  specific = 4
FEATURE [App::DocumentObjectGroupPython] Hg_element002  label="Hg_element : 002"  # scripted group (container) (typed FeaturePython)
  n = 1
  ref = Hg_element
FEATURE [App::DocumentObjectGroupPython] G4_Hg  # scripted group (container) (typed FeaturePython)
  Dunit = g/cm3
  Dvalue = 13.546
  Group = -> [Hg_element002]
  conduct = 2
  density = 1
  expand = 3
  formula = Hg
  name = G4_Hg
  specific = 4
FEATURE [App::DocumentObjectGroupPython] Tl_element002  label="Tl_element : 002"  # scripted group (container) (typed FeaturePython)
  n = 1
  ref = Tl_element
FEATURE [App::DocumentObjectGroupPython] G4_Tl  # scripted group (container) (typed FeaturePython)
  Dunit = g/cm3
  Dvalue = 11.72
  Group = -> [Tl_element002]
  conduct = 2
  density = 1
  expand = 3
  formula = Tl
  name = G4_Tl
  specific = 4
FEATURE [App::DocumentObjectGroupPython] Pb_element003  label="Pb_element : 1"  # scripted group (container) (typed FeaturePython)
  n = 1
  ref = Pb_element
FEATURE [App::DocumentObjectGroupPython] G4_Pb  # scripted group (container) (typed FeaturePython)
  Dunit = g/cm3
  Dvalue = 11.35
  Group = -> [Pb_element003]
  conduct = 2
  density = 1
  expand = 3
  formula = Pb
  name = G4_Pb
  specific = 4
FEATURE [App::DocumentObjectGroupPython] Bi_element002  label="Bi_element : 1"  # scripted group (container) (typed FeaturePython)
  n = 1
  ref = Bi_element
FEATURE [App::DocumentObjectGroupPython] G4_Bi  # scripted group (container) (typed FeaturePython)
  Dunit = g/cm3
  Dvalue = 9.747
  Group = -> [Bi_element002]
  conduct = 2
  density = 1
  expand = 3
  formula = Bi
  name = G4_Bi
  specific = 4
FEATURE [App::DocumentObjectGroupPython] Po_element001  label="Po_element : 1"  # scripted group (container) (typed FeaturePython)
  n = 1
  ref = Po_element
FEATURE [App::DocumentObjectGroupPython] G4_Po  # scripted group (container) (typed FeaturePython)
  Dunit = g/cm3
  Dvalue = 9.32
  Group = -> [Po_element001]
  conduct = 2
  density = 1
  expand = 3
  formula = Po
  name = G4_Po
  specific = 4
FEATURE [App::DocumentObjectGroupPython] At_element001  label="At_element : 1"  # scripted group (container) (typed FeaturePython)
  n = 1
  ref = At_element
FEATURE [App::DocumentObjectGroupPython] G4_At  # scripted group (container) (typed FeaturePython)
  Dunit = g/cm3
  Dvalue = 9.32
  Group = -> [At_element001]
  conduct = 2
  density = 1
  expand = 3
  formula = At
  name = G4_At
  specific = 4
FEATURE [App::DocumentObjectGroupPython] Rn_element001  label="Rn_element : 1"  # scripted group (container) (typed FeaturePython)
  n = 1
  ref = Rn_element
FEATURE [App::DocumentObjectGroupPython] G4_Rn  # scripted group (container) (typed FeaturePython)
  Dunit = g/cm3
  Dvalue = 0.00900662
  Group = -> [Rn_element001]
  conduct = 2
  density = 1
  expand = 3
  formula = Rn
  name = G4_Rn
  specific = 4
FEATURE [App::DocumentObjectGroupPython] Fr_element001  label="Fr_element : 1"  # scripted group (container) (typed FeaturePython)
  n = 1
  ref = Fr_element
FEATURE [App::DocumentObjectGroupPython] G4_Fr  # scripted group (container) (typed FeaturePython)
  Dunit = g/cm3
  Dvalue = 1
  Group = -> [Fr_element001]
  conduct = 2
  density = 1
  expand = 3
  formula = Fr
  name = G4_Fr
  specific = 4
FEATURE [App::DocumentObjectGroupPython] Ra_element001  label="Ra_element : 1"  # scripted group (container) (typed FeaturePython)
  n = 1
  ref = Ra_element
FEATURE [App::DocumentObjectGroupPython] G4_Ra  # scripted group (container) (typed FeaturePython)
  Dunit = g/cm3
  Dvalue = 5
  Group = -> [Ra_element001]
  conduct = 2
  density = 1
  expand = 3
  formula = Ra
  name = G4_Ra
  specific = 4
FEATURE [App::DocumentObjectGroupPython] Ac_element001  label="Ac_element : 1"  # scripted group (container) (typed FeaturePython)
  n = 1
  ref = Ac_element
FEATURE [App::DocumentObjectGroupPython] G4_Ac  # scripted group (container) (typed FeaturePython)
  Dunit = g/cm3
  Dvalue = 10.07
  Group = -> [Ac_element001]
  conduct = 2
  density = 1
  expand = 3
  formula = Ac
  name = G4_Ac
  specific = 4
FEATURE [App::DocumentObjectGroupPython] Th_element001  label="Th_element : 1"  # scripted group (container) (typed FeaturePython)
  n = 1
  ref = Th_element
FEATURE [App::DocumentObjectGroupPython] G4_Th  # scripted group (container) (typed FeaturePython)
  Dunit = g/cm3
  Dvalue = 11.72
  Group = -> [Th_element001]
  conduct = 2
  density = 1
  expand = 3
  formula = Th
  name = G4_Th
  specific = 4
FEATURE [App::DocumentObjectGroupPython] Pa_element001  label="Pa_element : 1"  # scripted group (container) (typed FeaturePython)
  n = 1
  ref = Pa_element
FEATURE [App::DocumentObjectGroupPython] G4_Pa  # scripted group (container) (typed FeaturePython)
  Dunit = g/cm3
  Dvalue = 15.37
  Group = -> [Pa_element001]
  conduct = 2
  density = 1
  expand = 3
  formula = Pa
  name = G4_Pa
  specific = 4
FEATURE [App::DocumentObjectGroupPython] U_element004  label="U_element : 004"  # scripted group (container) (typed FeaturePython)
  n = 1
  ref = U_element
FEATURE [App::DocumentObjectGroupPython] G4_U  # scripted group (container) (typed FeaturePython)
  Dunit = g/cm3
  Dvalue = 18.95
  Group = -> [U_element004]
  conduct = 2
  density = 1
  expand = 3
  formula = U
  name = G4_U
  specific = 4
FEATURE [App::DocumentObjectGroupPython] Np_element001  label="Np_element : 1"  # scripted group (container) (typed FeaturePython)
  n = 1
  ref = Np_element
FEATURE [App::DocumentObjectGroupPython] G4_Np  # scripted group (container) (typed FeaturePython)
  Dunit = g/cm3
  Dvalue = 20.25
  Group = -> [Np_element001]
  conduct = 2
  density = 1
  expand = 3
  formula = Np
  name = G4_Np
  specific = 4
FEATURE [App::DocumentObjectGroupPython] Pu_element002  label="Pu_element : 002"  # scripted group (container) (typed FeaturePython)
  n = 1
  ref = Pu_element
FEATURE [App::DocumentObjectGroupPython] G4_Pu  # scripted group (container) (typed FeaturePython)
  Dunit = g/cm3
  Dvalue = 19.84
  Group = -> [Pu_element002]
  conduct = 2
  density = 1
  expand = 3
  formula = Pu
  name = G4_Pu
  specific = 4
FEATURE [App::DocumentObjectGroupPython] Am_element001  label="Am_element : 1"  # scripted group (container) (typed FeaturePython)
  n = 1
  ref = Am_element
FEATURE [App::DocumentObjectGroupPython] G4_Am  # scripted group (container) (typed FeaturePython)
  Dunit = g/cm3
  Dvalue = 13.67
  Group = -> [Am_element001]
  conduct = 2
  density = 1
  expand = 3
  formula = Am
  name = G4_Am
  specific = 4
FEATURE [App::DocumentObjectGroupPython] Cm_element001  label="Cm_element : 1"  # scripted group (container) (typed FeaturePython)
  n = 1
  ref = Cm_element
FEATURE [App::DocumentObjectGroupPython] G4_Cm  # scripted group (container) (typed FeaturePython)
  Dunit = g/cm3
  Dvalue = 13.51
  Group = -> [Cm_element001]
  conduct = 2
  density = 1
  expand = 3
  formula = Cm
  name = G4_Cm
  specific = 4
FEATURE [App::DocumentObjectGroupPython] Bk_element001  label="Bk_element : 1"  # scripted group (container) (typed FeaturePython)
  n = 1
  ref = Bk_element
FEATURE [App::DocumentObjectGroupPython] G4_Bk  # scripted group (container) (typed FeaturePython)
  Dunit = g/cm3
  Dvalue = 14
  Group = -> [Bk_element001]
  conduct = 2
  density = 1
  expand = 3
  formula = Bk
  name = G4_Bk
  specific = 4
FEATURE [App::DocumentObjectGroupPython] Cf_element001  label="Cf_element : 1"  # scripted group (container) (typed FeaturePython)
  n = 1
  ref = Cf_element
FEATURE [App::DocumentObjectGroupPython] G4_Cf  # scripted group (container) (typed FeaturePython)
  Dunit = g/cm3
  Dvalue = 10
  Group = -> [Cf_element001]
  conduct = 2
  density = 1
  expand = 3
  formula = Cf
  name = G4_Cf
  specific = 4
FEATURE [App::DocumentObjectGroupPython] Element  # scripted group (container) (typed FeaturePython)
  Group = -> [G4_H,G4_He,G4_Li,G4_Be,G4_B,G4_C,G4_N,G4_O,G4_F,G4_Ne,G4_Na,G4_Mg,G4_Al,G4_Si,G4_P,G4_S,G4_Cl,G4_Ar,G4_K,G4_Ca,G4_Sc,G4_Ti,G4_V,G4_Cr,G4_Mn,G4_Fe,G4_Co,G4_Ni,G4_Cu,G4_Zn,G4_Ga,G4_Ge,G4_As,G4_Se,G4_Br,G4_Kr,G4_Rb,G4_Sr,G4_Y,G4_Zr,G4_Nb,G4_Mo,G4_Tc,G4_Ru,G4_Rh,G4_Pd,G4_Ag,G4_Cd,G4_In,G4_Sn,G4_Sb,G4_Te,G4_I,G4_Xe,G4_Cs,G4_Ba,G4_La,G4_Ce,G4_Pr,G4_Nd,G4_Pm,G4_Sm,G4_Eu,G4_Gd,G4_Tb,G4_Dy,G4_Ho,G4_Er,+30 more]
FEATURE [App::DocumentObjectGroupPython] H_element114  label="H_element : 063"  # scripted group (container) (typed FeaturePython)
  n = 2
  ref = H_element
FEATURE [App::DocumentObjectGroupPython] G4_lH2  # scripted group (container) (typed FeaturePython)
  Dunit = g/cm3
  Dvalue = 0.0708
  Group = -> [H_element114]
  conduct = 2
  density = 1
  expand = 3
  formula = G4_lH2
  name = G4_lH2
  specific = 4
FEATURE [App::DocumentObjectGroupPython] N_element049  label="N_element : 022"  # scripted group (container) (typed FeaturePython)
  n = 2
  ref = N_element
FEATURE [App::DocumentObjectGroupPython] G4_lN2  # scripted group (container) (typed FeaturePython)
  Dunit = g/cm3
  Dvalue = 0.807
  Group = -> [N_element049]
  conduct = 2
  density = 1
  expand = 3
  formula = G4_lN2
  name = G4_lN2
  specific = 4
FEATURE [App::DocumentObjectGroupPython] O_element106  label="O_element : 060"  # scripted group (container) (typed FeaturePython)
  n = 2
  ref = O_element
FEATURE [App::DocumentObjectGroupPython] G4_lO2  # scripted group (container) (typed FeaturePython)
  Dunit = g/cm3
  Dvalue = 1.141
  Group = -> [O_element106]
  conduct = 2
  density = 1
  expand = 3
  formula = G4_lO2
  name = G4_lO2
  specific = 4
FEATURE [App::DocumentObjectGroupPython] Ar_element003  label="Ar_element : 002"  # scripted group (container) (typed FeaturePython)
  n = 1
  ref = Ar_element
FEATURE [App::DocumentObjectGroupPython] G4_lAr  # scripted group (container) (typed FeaturePython)
  Dunit = g/cm3
  Dvalue = 1.396
  Group = -> [Ar_element003]
  conduct = 2
  density = 1
  expand = 3
  formula = G4_lAr
  name = G4_lAr
  specific = 4
FEATURE [App::DocumentObjectGroupPython] Br_element008  label="Br_element : 005"  # scripted group (container) (typed FeaturePython)
  n = 1
  ref = Br_element
FEATURE [App::DocumentObjectGroupPython] G4_lBr  # scripted group (container) (typed FeaturePython)
  Dunit = g/cm3
  Dvalue = 3.1028
  Group = -> [Br_element008]
  conduct = 2
  density = 1
  expand = 3
  formula = G4_lBr
  name = G4_lBr
  specific = 4
FEATURE [App::DocumentObjectGroupPython] Kr_element002  label="Kr_element : 002"  # scripted group (container) (typed FeaturePython)
  n = 1
  ref = Kr_element
FEATURE [App::DocumentObjectGroupPython] G4_lKr  # scripted group (container) (typed FeaturePython)
  Dunit = g/cm3
  Dvalue = 2.418
  Group = -> [Kr_element002]
  conduct = 2
  density = 1
  expand = 3
  formula = G4_lKr
  name = G4_lKr
  specific = 4
FEATURE [App::DocumentObjectGroupPython] Xe_element002  label="Xe_element : 002"  # scripted group (container) (typed FeaturePython)
  n = 1
  ref = Xe_element
FEATURE [App::DocumentObjectGroupPython] G4_lXe  # scripted group (container) (typed FeaturePython)
  Dunit = g/cm3
  Dvalue = 2.953
  Group = -> [Xe_element002]
  conduct = 2
  density = 1
  expand = 3
  formula = G4_lXe
  name = G4_lXe
  specific = 4
FEATURE [App::DocumentObjectGroupPython] O_element107  label="O_element : 061"  # scripted group (container) (typed FeaturePython)
  n = 4
  ref = O_element
FEATURE [App::DocumentObjectGroupPython] Pb_element004  label="Pb_element : 002"  # scripted group (container) (typed FeaturePython)
  n = 1
  ref = Pb_element
FEATURE [App::DocumentObjectGroupPython] W_element005  label="W_element : 005"  # scripted group (container) (typed FeaturePython)
  n = 1
  ref = W_element
FEATURE [App::DocumentObjectGroupPython] G4_PbWO4  # scripted group (container) (typed FeaturePython)
  Dunit = g/cm3
  Dvalue = 8.28
  Group = -> [O_element107,Pb_element004,W_element005]
  conduct = 2
  density = 1
  expand = 3
  formula = G4_PbWO4
  name = G4_PbWO4
  specific = 4
FEATURE [App::DocumentObjectGroupPython] H_element115  label="H_element : 064"  # scripted group (container) (typed FeaturePython)
  n = 1
  ref = H_element
FEATURE [App::DocumentObjectGroupPython] G4_Galactic  # scripted group (container) (typed FeaturePython)
  Dunit = g/cm3
  Dvalue = 0
  Group = -> [H_element115]
  conduct = 2
  density = 1
  expand = 3
  formula = G4_Galactic
  name = G4_Galactic
  specific = 4
FEATURE [App::DocumentObjectGroupPython] C_element125  label="C_element : 071"  # scripted group (container) (typed FeaturePython)
  n = 1
  ref = C_element
FEATURE [App::DocumentObjectGroupPython] G4_GRAPHITE_POROUS  # scripted group (container) (typed FeaturePython)
  Dunit = g/cm3
  Dvalue = 1.7
  Group = -> [C_element125]
  conduct = 2
  density = 1
  expand = 3
  formula = G4_GRAPHITE_POROUS
  name = G4_GRAPHITE_POROUS
  specific = 4
FEATURE [App::DocumentObjectGroupPython] H_element116  label="H_element : 0.150"  # scripted group (container) (typed FeaturePython)
  n = 0.080538
FEATURE [App::DocumentObjectGroupPython] C_element126  label="C_element : 0.600"  # scripted group (container) (typed FeaturePython)
  n = 0.599848
FEATURE [App::DocumentObjectGroupPython] O_element108  label="O_element : 0.320"  # scripted group (container) (typed FeaturePython)
  n = 0.319614
FEATURE [App::DocumentObjectGroupPython] G4_LUCITE  # scripted group (container) (typed FeaturePython)
  Dunit = g/cm3
  Dvalue = 1.19
  Group = -> [H_element116,C_element126,O_element108]
  conduct = 2
  density = 1
  expand = 3
  formula = G4_LUCITE
  name = G4_LUCITE
  specific = 4
FEATURE [App::DocumentObjectGroupPython] Cu_element002  label="Cu_element : 62"  # scripted group (container) (typed FeaturePython)
  n = 62
  ref = Cu_element
FEATURE [App::DocumentObjectGroupPython] Zn_element002  label="Zn_element : 35"  # scripted group (container) (typed FeaturePython)
  n = 35
  ref = Zn_element
FEATURE [App::DocumentObjectGroupPython] Pb_element005  label="Pb_element : 3"  # scripted group (container) (typed FeaturePython)
  n = 3
  ref = Pb_element
FEATURE [App::DocumentObjectGroupPython] G4_BRASS  # scripted group (container) (typed FeaturePython)
  Dunit = g/cm3
  Dvalue = 8.52
  Group = -> [Cu_element002,Zn_element002,Pb_element005]
  conduct = 2
  density = 1
  expand = 3
  formula = G4_BRASS
  name = G4_BRASS
  specific = 4
FEATURE [App::DocumentObjectGroupPython] Cu_element003  label="Cu_element : 89"  # scripted group (container) (typed FeaturePython)
  n = 89
  ref = Cu_element
FEATURE [App::DocumentObjectGroupPython] Zn_element003  label="Zn_element : 9"  # scripted group (container) (typed FeaturePython)
  n = 9
  ref = Zn_element
FEATURE [App::DocumentObjectGroupPython] Pb_element006  label="Pb_element : 2"  # scripted group (container) (typed FeaturePython)
  n = 2
  ref = Pb_element
FEATURE [App::DocumentObjectGroupPython] G4_BRONZE  # scripted group (container) (typed FeaturePython)
  Dunit = g/cm3
  Dvalue = 8.82
  Group = -> [Cu_element003,Zn_element003,Pb_element006]
  conduct = 2
  density = 1
  expand = 3
  formula = G4_BRONZE
  name = G4_BRONZE
  specific = 4
FEATURE [App::DocumentObjectGroupPython] Fe_element008  label="Fe_element : 74"  # scripted group (container) (typed FeaturePython)
  n = 74
  ref = Fe_element
FEATURE [App::DocumentObjectGroupPython] Cr_element002  label="Cr_element : 18"  # scripted group (container) (typed FeaturePython)
  n = 18
  ref = Cr_element
FEATURE [App::DocumentObjectGroupPython] Ni_element002  label="Ni_element : 8"  # scripted group (container) (typed FeaturePython)
  n = 8
  ref = Ni_element
FEATURE [App::DocumentObjectGroupPython] G4_STAINLESS_STEEL  label="G4_STAINLESS-STEEL"  # scripted group (container) (typed FeaturePython)
  Dunit = g/cm3
  Dvalue = 8
  Group = -> [Fe_element008,Cr_element002,Ni_element002]
  conduct = 2
  density = 1
  expand = 3
  formula = G4_STAINLESS-STEEL
  name = G4_STAINLESS-STEEL
  specific = 4
FEATURE [App::DocumentObjectGroupPython] H_element117  label="H_element : 065"  # scripted group (container) (typed FeaturePython)
  n = 18
  ref = H_element
FEATURE [App::DocumentObjectGroupPython] C_element127  label="C_element : 072"  # scripted group (container) (typed FeaturePython)
  n = 12
  ref = C_element
FEATURE [App::DocumentObjectGroupPython] O_element109  label="O_element : 062"  # scripted group (container) (typed FeaturePython)
  n = 7
  ref = O_element
FEATURE [App::DocumentObjectGroupPython] G4_CR39  # scripted group (container) (typed FeaturePython)
  Dunit = g/cm3
  Dvalue = 1.32
  Group = -> [H_element117,C_element127,O_element109]
  conduct = 2
  density = 1
  expand = 3
  formula = G4_CR39
  name = G4_CR39
  specific = 4
FEATURE [App::DocumentObjectGroupPython] H_element118  label="H_element : 38"  # scripted group (container) (typed FeaturePython)
  n = 38
  ref = H_element
FEATURE [App::DocumentObjectGroupPython] C_element128  label="C_element : 073"  # scripted group (container) (typed FeaturePython)
  n = 18
  ref = C_element
FEATURE [App::DocumentObjectGroupPython] O_element110  label="O_element : 063"  # scripted group (container) (typed FeaturePython)
  n = 1
  ref = O_element
FEATURE [App::DocumentObjectGroupPython] G4_OCTADECANOL  # scripted group (container) (typed FeaturePython)
  Dunit = g/cm3
  Dvalue = 0.812
  Group = -> [H_element118,C_element128,O_element110]
  conduct = 2
  density = 1
  expand = 3
  formula = G4_OCTADECANOL
  name = G4_OCTADECANOL
  specific = 4
FEATURE [App::DocumentObjectGroupPython] HEP  # scripted group (container) (typed FeaturePython)
  Group = -> [G4_lH2,G4_lN2,G4_lO2,G4_lAr,G4_lBr,G4_lKr,G4_lXe,G4_PbWO4,G4_Galactic,G4_GRAPHITE_POROUS,G4_LUCITE,G4_BRASS,G4_BRONZE,G4_STAINLESS_STEEL,G4_CR39,G4_OCTADECANOL]
FEATURE [App::DocumentObjectGroupPython] C_element129  label="C_element : 074"  # scripted group (container) (typed FeaturePython)
  n = 14
  ref = C_element
FEATURE [App::DocumentObjectGroupPython] H_element119  label="H_element : 066"  # scripted group (container) (typed FeaturePython)
  n = 10
  ref = H_element
FEATURE [App::DocumentObjectGroupPython] O_element111  label="O_element : 064"  # scripted group (container) (typed FeaturePython)
  n = 2
  ref = O_element
FEATURE [App::DocumentObjectGroupPython] N_element050  label="N_element : 023"  # scripted group (container) (typed FeaturePython)
  n = 2
  ref = N_element
FEATURE [App::DocumentObjectGroupPython] G4_KEVLAR  # scripted group (container) (typed FeaturePython)
  Dunit = g/cm3
  Dvalue = 1.44
  Group = -> [C_element129,H_element119,O_element111,N_element050]
  conduct = 2
  density = 1
  expand = 3
  formula = G4_KEVLAR
  name = G4_KEVLAR
  specific = 4
FEATURE [App::DocumentObjectGroupPython] C_element130  label="C_element : 075"  # scripted group (container) (typed FeaturePython)
  n = 10
  ref = C_element
FEATURE [App::DocumentObjectGroupPython] H_element120  label="H_element : 067"  # scripted group (container) (typed FeaturePython)
  n = 8
  ref = H_element
FEATURE [App::DocumentObjectGroupPython] O_element112  label="O_element : 065"  # scripted group (container) (typed FeaturePython)
  n = 4
  ref = O_element
FEATURE [App::DocumentObjectGroupPython] G4_DACRON  # scripted group (container) (typed FeaturePython)
  Dunit = g/cm3
  Dvalue = 1.4
  Group = -> [C_element130,H_element120,O_element112]
  conduct = 2
  density = 1
  expand = 3
  formula = G4_DACRON
  name = G4_DACRON
  specific = 4
FEATURE [App::DocumentObjectGroupPython] C_element131  label="C_element : 076"  # scripted group (container) (typed FeaturePython)
  n = 4
  ref = C_element
FEATURE [App::DocumentObjectGroupPython] H_element121  label="H_element : 068"  # scripted group (container) (typed FeaturePython)
  n = 5
  ref = H_element
FEATURE [App::DocumentObjectGroupPython] Cl_element030  label="Cl_element : 016"  # scripted group (container) (typed FeaturePython)
  n = 1
  ref = Cl_element
FEATURE [App::DocumentObjectGroupPython] G4_NEOPRENE  # scripted group (container) (typed FeaturePython)
  Dunit = g/cm3
  Dvalue = 1.23
  Group = -> [C_element131,H_element121,Cl_element030]
  conduct = 2
  density = 1
  expand = 3
  formula = G4_NEOPRENE
  name = G4_NEOPRENE
  specific = 4
FEATURE [App::DocumentObjectGroupPython] Space  # scripted group (container) (typed FeaturePython)
  Group = -> [G4_KEVLAR,G4_DACRON,G4_NEOPRENE]
FEATURE [App::DocumentObjectGroupPython] H_element122  label="H_element : 069"  # scripted group (container) (typed FeaturePython)
  n = 5
  ref = H_element
FEATURE [App::DocumentObjectGroupPython] C_element132  label="C_element : 077"  # scripted group (container) (typed FeaturePython)
  n = 4
  ref = C_element
FEATURE [App::DocumentObjectGroupPython] N_element051  label="N_element : 3"  # scripted group (container) (typed FeaturePython)
  n = 3
  ref = N_element
FEATURE [App::DocumentObjectGroupPython] O_element113  label="O_element : 066"  # scripted group (container) (typed FeaturePython)
  n = 1
  ref = O_element
FEATURE [App::DocumentObjectGroupPython] G4_CYTOSINE  # scripted group (container) (typed FeaturePython)
  Dunit = g/cm3
  Dvalue = 1.55
  Group = -> [H_element122,C_element132,N_element051,O_element113]
  conduct = 2
  density = 1
  expand = 3
  formula = G4_CYTOSINE
  name = G4_CYTOSINE
  specific = 4
FEATURE [App::DocumentObjectGroupPython] H_element123  label="H_element : 070"  # scripted group (container) (typed FeaturePython)
  n = 6
  ref = H_element
FEATURE [App::DocumentObjectGroupPython] C_element133  label="C_element : 078"  # scripted group (container) (typed FeaturePython)
  n = 5
  ref = C_element
FEATURE [App::DocumentObjectGroupPython] N_element052  label="N_element : 024"  # scripted group (container) (typed FeaturePython)
  n = 2
  ref = N_element
FEATURE [App::DocumentObjectGroupPython] O_element114  label="O_element : 067"  # scripted group (container) (typed FeaturePython)
  n = 2
  ref = O_element
FEATURE [App::DocumentObjectGroupPython] G4_THYMINE  # scripted group (container) (typed FeaturePython)
  Dunit = g/cm3
  Dvalue = 1.23
  Group = -> [H_element123,C_element133,N_element052,O_element114]
  conduct = 2
  density = 1
  expand = 3
  formula = G4_THYMINE
  name = G4_THYMINE
  specific = 4
FEATURE [App::DocumentObjectGroupPython] H_element124  label="H_element : 071"  # scripted group (container) (typed FeaturePython)
  n = 4
  ref = H_element
FEATURE [App::DocumentObjectGroupPython] C_element134  label="C_element : 079"  # scripted group (container) (typed FeaturePython)
  n = 4
  ref = C_element
FEATURE [App::DocumentObjectGroupPython] N_element053  label="N_element : 025"  # scripted group (container) (typed FeaturePython)
  n = 2
  ref = N_element
FEATURE [App::DocumentObjectGroupPython] O_element115  label="O_element : 068"  # scripted group (container) (typed FeaturePython)
  n = 2
  ref = O_element
FEATURE [App::DocumentObjectGroupPython] G4_URACIL  # scripted group (container) (typed FeaturePython)
  Dunit = g/cm3
  Dvalue = 1.32
  Group = -> [H_element124,C_element134,N_element053,O_element115]
  conduct = 2
  density = 1
  expand = 3
  formula = G4_URACIL
  name = G4_URACIL
  specific = 4
FEATURE [App::DocumentObjectGroupPython] H_element125  label="H_element : 072"  # scripted group (container) (typed FeaturePython)
  n = 4
  ref = H_element
FEATURE [App::DocumentObjectGroupPython] C_element135  label="C_element : 080"  # scripted group (container) (typed FeaturePython)
  n = 5
  ref = C_element
FEATURE [App::DocumentObjectGroupPython] N_element054  label="N_element : 026"  # scripted group (container) (typed FeaturePython)
  n = 5
  ref = N_element
FEATURE [App::DocumentObjectGroupPython] G4_DNA_ADENINE  # scripted group (container) (typed FeaturePython)
  Dunit = g/cm3
  Dvalue = 1
  Group = -> [H_element125,C_element135,N_element054]
  conduct = 2
  density = 1
  expand = 3
  formula = G4_DNA_ADENINE
  name = G4_DNA_ADENINE
  specific = 4
FEATURE [App::DocumentObjectGroupPython] H_element126  label="H_element : 073"  # scripted group (container) (typed FeaturePython)
  n = 4
  ref = H_element
FEATURE [App::DocumentObjectGroupPython] C_element136  label="C_element : 081"  # scripted group (container) (typed FeaturePython)
  n = 5
  ref = C_element
FEATURE [App::DocumentObjectGroupPython] N_element055  label="N_element : 027"  # scripted group (container) (typed FeaturePython)
  n = 5
  ref = N_element
FEATURE [App::DocumentObjectGroupPython] O_element116  label="O_element : 069"  # scripted group (container) (typed FeaturePython)
  n = 1
  ref = O_element
FEATURE [App::DocumentObjectGroupPython] G4_DNA_GUANINE  # scripted group (container) (typed FeaturePython)
  Dunit = g/cm3
  Dvalue = 1
  Group = -> [H_element126,C_element136,N_element055,O_element116]
  conduct = 2
  density = 1
  expand = 3
  formula = G4_DNA_GUANINE
  name = G4_DNA_GUANINE
  specific = 4
FEATURE [App::DocumentObjectGroupPython] H_element127  label="H_element : 074"  # scripted group (container) (typed FeaturePython)
  n = 4
  ref = H_element
FEATURE [App::DocumentObjectGroupPython] C_element137  label="C_element : 082"  # scripted group (container) (typed FeaturePython)
  n = 4
  ref = C_element
FEATURE [App::DocumentObjectGroupPython] N_element056  label="N_element : 028"  # scripted group (container) (typed FeaturePython)
  n = 3
  ref = N_element
FEATURE [App::DocumentObjectGroupPython] O_element117  label="O_element : 070"  # scripted group (container) (typed FeaturePython)
  n = 1
  ref = O_element
FEATURE [App::DocumentObjectGroupPython] G4_DNA_CYTOSINE  # scripted group (container) (typed FeaturePython)
  Dunit = g/cm3
  Dvalue = 1
  Group = -> [H_element127,C_element137,N_element056,O_element117]
  conduct = 2
  density = 1
  expand = 3
  formula = G4_DNA_CYTOSINE
  name = G4_DNA_CYTOSINE
  specific = 4
FEATURE [App::DocumentObjectGroupPython] H_element128  label="H_element : 075"  # scripted group (container) (typed FeaturePython)
  n = 5
  ref = H_element
FEATURE [App::DocumentObjectGroupPython] C_element138  label="C_element : 083"  # scripted group (container) (typed FeaturePython)
  n = 5
  ref = C_element
FEATURE [App::DocumentObjectGroupPython] N_element057  label="N_element : 029"  # scripted group (container) (typed FeaturePython)
  n = 2
  ref = N_element
FEATURE [App::DocumentObjectGroupPython] O_element118  label="O_element : 071"  # scripted group (container) (typed FeaturePython)
  n = 2
  ref = O_element
FEATURE [App::DocumentObjectGroupPython] G4_DNA_THYMINE  # scripted group (container) (typed FeaturePython)
  Dunit = g/cm3
  Dvalue = 1
  Group = -> [H_element128,C_element138,N_element057,O_element118]
  conduct = 2
  density = 1
  expand = 3
  formula = G4_DNA_THYMINE
  name = G4_DNA_THYMINE
  specific = 4
FEATURE [App::DocumentObjectGroupPython] H_element129  label="H_element : 076"  # scripted group (container) (typed FeaturePython)
  n = 3
  ref = H_element
FEATURE [App::DocumentObjectGroupPython] C_element139  label="C_element : 084"  # scripted group (container) (typed FeaturePython)
  n = 4
  ref = C_element
FEATURE [App::DocumentObjectGroupPython] N_element058  label="N_element : 030"  # scripted group (container) (typed FeaturePython)
  n = 2
  ref = N_element
FEATURE [App::DocumentObjectGroupPython] O_element119  label="O_element : 072"  # scripted group (container) (typed FeaturePython)
  n = 2
  ref = O_element
FEATURE [App::DocumentObjectGroupPython] G4_DNA_URACIL  # scripted group (container) (typed FeaturePython)
  Dunit = g/cm3
  Dvalue = 1
  Group = -> [H_element129,C_element139,N_element058,O_element119]
  conduct = 2
  density = 1
  expand = 3
  formula = G4_DNA_URACIL
  name = G4_DNA_URACIL
  specific = 4
FEATURE [App::DocumentObjectGroupPython] H_element130  label="H_element : 077"  # scripted group (container) (typed FeaturePython)
  n = 10
  ref = H_element
FEATURE [App::DocumentObjectGroupPython] C_element140  label="C_element : 085"  # scripted group (container) (typed FeaturePython)
  n = 10
  ref = C_element
FEATURE [App::DocumentObjectGroupPython] N_element059  label="N_element : 031"  # scripted group (container) (typed FeaturePython)
  n = 5
  ref = N_element
FEATURE [App::DocumentObjectGroupPython] O_element120  label="O_element : 073"  # scripted group (container) (typed FeaturePython)
  n = 4
  ref = O_element
FEATURE [App::DocumentObjectGroupPython] G4_DNA_ADENOSINE  # scripted group (container) (typed FeaturePython)
  Dunit = g/cm3
  Dvalue = 1
  Group = -> [H_element130,C_element140,N_element059,O_element120]
  conduct = 2
  density = 1
  expand = 3
  formula = G4_DNA_ADENOSINE
  name = G4_DNA_ADENOSINE
  specific = 4
FEATURE [App::DocumentObjectGroupPython] H_element131  label="H_element : 078"  # scripted group (container) (typed FeaturePython)
  n = 10
  ref = H_element
FEATURE [App::DocumentObjectGroupPython] C_element141  label="C_element : 086"  # scripted group (container) (typed FeaturePython)
  n = 10
  ref = C_element
FEATURE [App::DocumentObjectGroupPython] N_element060  label="N_element : 032"  # scripted group (container) (typed FeaturePython)
  n = 5
  ref = N_element
FEATURE [App::DocumentObjectGroupPython] O_element121  label="O_element : 074"  # scripted group (container) (typed FeaturePython)
  n = 5
  ref = O_element
FEATURE [App::DocumentObjectGroupPython] G4_DNA_GUANOSINE  # scripted group (container) (typed FeaturePython)
  Dunit = g/cm3
  Dvalue = 1
  Group = -> [H_element131,C_element141,N_element060,O_element121]
  conduct = 2
  density = 1
  expand = 3
  formula = G4_DNA_GUANOSINE
  name = G4_DNA_GUANOSINE
  specific = 4
FEATURE [App::DocumentObjectGroupPython] H_element132  label="H_element : 079"  # scripted group (container) (typed FeaturePython)
  n = 10
  ref = H_element
FEATURE [App::DocumentObjectGroupPython] C_element142  label="C_element : 087"  # scripted group (container) (typed FeaturePython)
  n = 9
  ref = C_element
FEATURE [App::DocumentObjectGroupPython] N_element061  label="N_element : 033"  # scripted group (container) (typed FeaturePython)
  n = 3
  ref = N_element
FEATURE [App::DocumentObjectGroupPython] O_element122  label="O_element : 075"  # scripted group (container) (typed FeaturePython)
  n = 5
  ref = O_element
FEATURE [App::DocumentObjectGroupPython] G4_DNA_CYTIDINE  # scripted group (container) (typed FeaturePython)
  Dunit = g/cm3
  Dvalue = 1
  Group = -> [H_element132,C_element142,N_element061,O_element122]
  conduct = 2
  density = 1
  expand = 3
  formula = G4_DNA_CYTIDINE
  name = G4_DNA_CYTIDINE
  specific = 4
FEATURE [App::DocumentObjectGroupPython] H_element133  label="H_element : 080"  # scripted group (container) (typed FeaturePython)
  n = 9
  ref = H_element
FEATURE [App::DocumentObjectGroupPython] C_element143  label="C_element : 088"  # scripted group (container) (typed FeaturePython)
  n = 9
  ref = C_element
FEATURE [App::DocumentObjectGroupPython] N_element062  label="N_element : 034"  # scripted group (container) (typed FeaturePython)
  n = 2
  ref = N_element
FEATURE [App::DocumentObjectGroupPython] O_element123  label="O_element : 076"  # scripted group (container) (typed FeaturePython)
  n = 6
  ref = O_element
FEATURE [App::DocumentObjectGroupPython] G4_DNA_URIDINE  # scripted group (container) (typed FeaturePython)
  Dunit = g/cm3
  Dvalue = 1
  Group = -> [H_element133,C_element143,N_element062,O_element123]
  conduct = 2
  density = 1
  expand = 3
  formula = G4_DNA_URIDINE
  name = G4_DNA_URIDINE
  specific = 4
FEATURE [App::DocumentObjectGroupPython] H_element134  label="H_element : 081"  # scripted group (container) (typed FeaturePython)
  n = 11
  ref = H_element
FEATURE [App::DocumentObjectGroupPython] C_element144  label="C_element : 089"  # scripted group (container) (typed FeaturePython)
  n = 10
  ref = C_element
FEATURE [App::DocumentObjectGroupPython] N_element063  label="N_element : 035"  # scripted group (container) (typed FeaturePython)
  n = 2
  ref = N_element
FEATURE [App::DocumentObjectGroupPython] O_element124  label="O_element : 077"  # scripted group (container) (typed FeaturePython)
  n = 6
  ref = O_element
FEATURE [App::DocumentObjectGroupPython] G4_DNA_METHYLURIDINE  # scripted group (container) (typed FeaturePython)
  Dunit = g/cm3
  Dvalue = 1
  Group = -> [H_element134,C_element144,N_element063,O_element124]
  conduct = 2
  density = 1
  expand = 3
  formula = G4_DNA_METHYLURIDINE
  name = G4_DNA_METHYLURIDINE
  specific = 4
FEATURE [App::DocumentObjectGroupPython] P_element014  label="P_element : 003"  # scripted group (container) (typed FeaturePython)
  n = 1
  ref = P_element
FEATURE [App::DocumentObjectGroupPython] O_element125  label="O_element : 078"  # scripted group (container) (typed FeaturePython)
  n = 3
  ref = O_element
FEATURE [App::DocumentObjectGroupPython] G4_DNA_MONOPHOSPHATE  # scripted group (container) (typed FeaturePython)
  Dunit = g/cm3
  Dvalue = 1
  Group = -> [P_element014,O_element125]
  conduct = 2
  density = 1
  expand = 3
  formula = G4_DNA_MONOPHOSPHATE
  name = G4_DNA_MONOPHOSPHATE
  specific = 4
FEATURE [App::DocumentObjectGroupPython] H_element135  label="H_element : 082"  # scripted group (container) (typed FeaturePython)
  n = 10
  ref = H_element
FEATURE [App::DocumentObjectGroupPython] C_element145  label="C_element : 090"  # scripted group (container) (typed FeaturePython)
  n = 10
  ref = C_element
FEATURE [App::DocumentObjectGroupPython] N_element064  label="N_element : 036"  # scripted group (container) (typed FeaturePython)
  n = 5
  ref = N_element
FEATURE [App::DocumentObjectGroupPython] O_element126  label="O_element : 079"  # scripted group (container) (typed FeaturePython)
  n = 7
  ref = O_element
FEATURE [App::DocumentObjectGroupPython] P_element015  label="P_element : 004"  # scripted group (container) (typed FeaturePython)
  n = 1
  ref = P_element
FEATURE [App::DocumentObjectGroupPython] G4_DNA_A  # scripted group (container) (typed FeaturePython)
  Dunit = g/cm3
  Dvalue = 1
  Group = -> [H_element135,C_element145,N_element064,O_element126,P_element015]
  conduct = 2
  density = 1
  expand = 3
  formula = G4_DNA_A
  name = G4_DNA_A
  specific = 4
FEATURE [App::DocumentObjectGroupPython] H_element136  label="H_element : 083"  # scripted group (container) (typed FeaturePython)
  n = 10
  ref = H_element
FEATURE [App::DocumentObjectGroupPython] C_element146  label="C_element : 091"  # scripted group (container) (typed FeaturePython)
  n = 10
  ref = C_element
FEATURE [App::DocumentObjectGroupPython] N_element065  label="N_element : 037"  # scripted group (container) (typed FeaturePython)
  n = 5
  ref = N_element
FEATURE [App::DocumentObjectGroupPython] O_element127  label="O_element : 8"  # scripted group (container) (typed FeaturePython)
  n = 8
  ref = O_element
FEATURE [App::DocumentObjectGroupPython] P_element016  label="P_element : 005"  # scripted group (container) (typed FeaturePython)
  n = 1
  ref = P_element
FEATURE [App::DocumentObjectGroupPython] G4_DNA_G  # scripted group (container) (typed FeaturePython)
  Dunit = g/cm3
  Dvalue = 1
  Group = -> [H_element136,C_element146,N_element065,O_element127,P_element016]
  conduct = 2
  density = 1
  expand = 3
  formula = G4_DNA_G
  name = G4_DNA_G
  specific = 4
FEATURE [App::DocumentObjectGroupPython] H_element137  label="H_element : 084"  # scripted group (container) (typed FeaturePython)
  n = 10
  ref = H_element
FEATURE [App::DocumentObjectGroupPython] C_element147  label="C_element : 092"  # scripted group (container) (typed FeaturePython)
  n = 9
  ref = C_element
FEATURE [App::DocumentObjectGroupPython] N_element066  label="N_element : 038"  # scripted group (container) (typed FeaturePython)
  n = 3
  ref = N_element
FEATURE [App::DocumentObjectGroupPython] O_element128  label="O_element : 080"  # scripted group (container) (typed FeaturePython)
  n = 8
  ref = O_element
FEATURE [App::DocumentObjectGroupPython] P_element017  label="P_element : 006"  # scripted group (container) (typed FeaturePython)
  n = 1
  ref = P_element
FEATURE [App::DocumentObjectGroupPython] G4_DNA_C  # scripted group (container) (typed FeaturePython)
  Dunit = g/cm3
  Dvalue = 1
  Group = -> [H_element137,C_element147,N_element066,O_element128,P_element017]
  conduct = 2
  density = 1
  expand = 3
  formula = G4_DNA_C
  name = G4_DNA_C
  specific = 4
FEATURE [App::DocumentObjectGroupPython] H_element138  label="H_element : 085"  # scripted group (container) (typed FeaturePython)
  n = 9
  ref = H_element
FEATURE [App::DocumentObjectGroupPython] C_element148  label="C_element : 093"  # scripted group (container) (typed FeaturePython)
  n = 9
  ref = C_element
FEATURE [App::DocumentObjectGroupPython] N_element067  label="N_element : 039"  # scripted group (container) (typed FeaturePython)
  n = 2
  ref = N_element
FEATURE [App::DocumentObjectGroupPython] O_element129  label="O_element : 9"  # scripted group (container) (typed FeaturePython)
  n = 9
  ref = O_element
FEATURE [App::DocumentObjectGroupPython] P_element018  label="P_element : 007"  # scripted group (container) (typed FeaturePython)
  n = 1
  ref = P_element
FEATURE [App::DocumentObjectGroupPython] G4_DNA_U  # scripted group (container) (typed FeaturePython)
  Dunit = g/cm3
  Dvalue = 1
  Group = -> [H_element138,C_element148,N_element067,O_element129,P_element018]
  conduct = 2
  density = 1
  expand = 3
  formula = G4_DNA_U
  name = G4_DNA_U
  specific = 4
FEATURE [App::DocumentObjectGroupPython] H_element139  label="H_element : 086"  # scripted group (container) (typed FeaturePython)
  n = 11
  ref = H_element
FEATURE [App::DocumentObjectGroupPython] C_element149  label="C_element : 094"  # scripted group (container) (typed FeaturePython)
  n = 10
  ref = C_element
FEATURE [App::DocumentObjectGroupPython] N_element068  label="N_element : 040"  # scripted group (container) (typed FeaturePython)
  n = 2
  ref = N_element
FEATURE [App::DocumentObjectGroupPython] O_element130  label="O_element : 081"  # scripted group (container) (typed FeaturePython)
  n = 9
  ref = O_element
FEATURE [App::DocumentObjectGroupPython] P_element019  label="P_element : 008"  # scripted group (container) (typed FeaturePython)
  n = 1
  ref = P_element
FEATURE [App::DocumentObjectGroupPython] G4_DNA_MU  # scripted group (container) (typed FeaturePython)
  Dunit = g/cm3
  Dvalue = 1
  Group = -> [H_element139,C_element149,N_element068,O_element130,P_element019]
  conduct = 2
  density = 1
  expand = 3
  formula = G4_DNA_MU
  name = G4_DNA_MU
  specific = 4
FEATURE [App::DocumentObjectGroupPython] BioChemical  # scripted group (container) (typed FeaturePython)
  Group = -> [G4_CYTOSINE,G4_THYMINE,G4_URACIL,G4_DNA_ADENINE,G4_DNA_GUANINE,G4_DNA_CYTOSINE,G4_DNA_THYMINE,G4_DNA_URACIL,G4_DNA_ADENOSINE,G4_DNA_GUANOSINE,G4_DNA_CYTIDINE,G4_DNA_URIDINE,G4_DNA_METHYLURIDINE,G4_DNA_MONOPHOSPHATE,G4_DNA_A,G4_DNA_G,G4_DNA_C,G4_DNA_U,G4_DNA_MU]
FEATURE [App::DocumentObjectGroupPython] G4Materials  # scripted group (container) (typed FeaturePython)
  Group = -> [NIST,Element,HEP,Space,BioChemical]
  version = 1
FEATURE [App::DocumentObjectGroupPython] Geant4  # scripted group (container) (typed FeaturePython)
  Group = -> [G4Isotopes,G4Elements,G4Materials]
FEATURE [App::DocumentObjectGroupPython] Materials  # scripted group (container) (typed FeaturePython)
  Group = -> [Geant4]
FEATURE [Part::FeaturePython] GDMLBox_WorldBox  # WARN: FeaturePython — macro-defined, semantics opaque (R4)
  lunit = 2
  material = 5
  x = 200.2
  y = 130
  z = 130
FEATURE [Part::FeaturePython] GDMLBox_Box  # WARN: FeaturePython — macro-defined, semantics opaque (R4)
  Placement = pos=(30,0,0) rot=(0,0,1;0rad)
  lunit = 2
  material = 0
  x = 10
  y = 10
  z = 10
FEATURE [Part::FeaturePython] GDMLTorus  # WARN: FeaturePython — macro-defined, semantics opaque (R4)
  Placement = pos=(30,0,0) rot=(0,1,0;1.5708rad)
  aunit = deg
  deltaphi = 360
  lunit = 2
  material = 0
  rmax = 2
  rmin = 0
  rtor = 8
  startphi = 0
FEATURE [Part::MultiFuse] Fusion
  Shapes = -> [GDMLBox_Box,GDMLTorus]
FEATURE [Part::FeaturePython] Array  # Draft array (typed FeaturePython)
  AlwaysSyncPlacement = false
  Angle = 180
  ArrayType = 1
  Axis = (0,0,1)
  Base = -> Fusion
  Center = (0,0,0)
  Count = 5
  ExpandArray = false
  Fuse = false
  IntervalAxis = (0,0,0)
  IntervalX = (50,0,0)
  IntervalY = (0,50,0)
  IntervalZ = (0,0,50)
  NumberCircles = 3
  NumberPolar = 5
  NumberX = 2
  NumberY = 2
  NumberZ = 1
  Placement = pos=(0,0,0) rot=(0,0,1;0.785398rad)
  PlacementList = 5 placements: [(0,0,0),(0,0,0),(0,0,0),(0,0,0),(0,0,0)]
  RadialDistance = 50
  ScaleList = (5) [(1,1,1),(1,1,1),(1,1,1),(1,1,1),(1,1,1)]
  Symmetry = 1
  TangentialDistance = 25
FEATURE [App::Part] Part001
  Group = -> [Array]
  Origin = -> Origin004
FEATURE [App::Part] worldVOL
  Group = -> [GDMLBox_WorldBox,Part001]
  Origin = -> Origin
